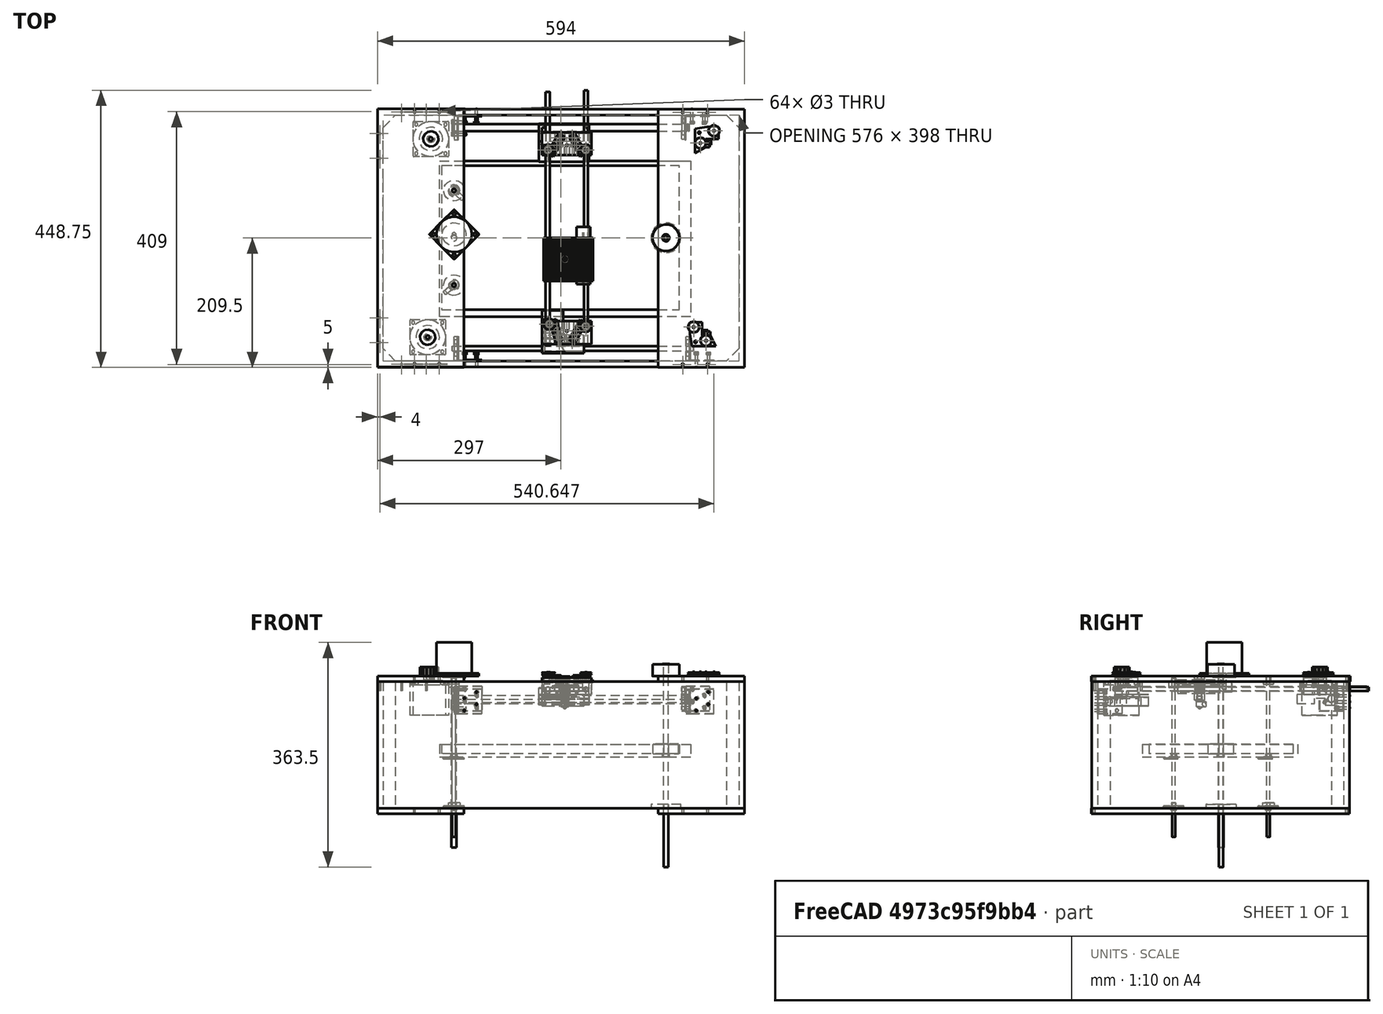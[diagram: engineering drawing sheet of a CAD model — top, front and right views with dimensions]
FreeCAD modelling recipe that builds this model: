
FCSTD DOCUMENT  (FreeCAD 0.18R16110 (Git))
Label: assembly
License: All rights reserved
LicenseURL: http://en.wikipedia.org/wiki/All_rights_reserved
objects: App::FeaturePython×310, Part::FeaturePython×82, Part::Part2DObjectPython×29, App::DocumentObjectGroup×14
note: 111 computed .brp shape members not serialized (recipe doc carries the construction recipe); baked Part::Feature solids carry a one-line shape summary decoded from their .brp

FEATURE [Part::FeaturePython] b_Case_001_  label="Case_001"  # a2plus imported part (geometry in sourceFile) (typed FeaturePython)
  a2p_Version = V0.1
  fixedPosition = true
  sourceFile = ./../Case.FCStd
  subassemblyImport = false
  timeLastImport = 1.56043e+09
  updateColors = true
FEATURE [Part::FeaturePython] b_cylinder1_11_5_001_  label="cylinder1_11.5_001"  # a2plus imported part (geometry in sourceFile) (typed FeaturePython)
  Placement = pos=(-175.853,179,-27.4993) rot=(-0.410574,0.814161,-0.410574;1.77496rad)
  a2p_Version = V0.1
  fixedPosition = false
  sourceFile = ./../Cylinders/cylinder1_11.5_383.FCStd
  subassemblyImport = false
  timeLastImport = 1.56017e+09
  updateColors = true
FEATURE [Part::FeaturePython] b_cylinder2_7_5_001_  label="cylinder2_7.5_001"  # a2plus imported part (geometry in sourceFile) (typed FeaturePython)
  Placement = pos=(-175.853,-179,-31.8006) rot=(0.025254,0.999362,0.025254;1.57143rad)
  a2p_Version = V0.1
  fixedPosition = false
  sourceFile = ./../Cylinders/cylinder2_7.5_390.FCStd
  subassemblyImport = false
  timeLastImport = 1.56017e+09
  updateColors = true
FEATURE [Part::FeaturePython] b_carrier1_11_5_001_  label="carrier1_11.5_001"  # a2plus imported part (geometry in sourceFile) (typed FeaturePython)
  Placement = pos=(45.4279,185.2,-9.99932) rot=(0.57735,-0.57735,-0.57735;2.0944rad)
  a2p_Version = V0.1
  fixedPosition = false
  sourceFile = ./../Carrieges/carrier1_11.5.FCStd
  subassemblyImport = false
  timeLastImport = 1.56017e+09
  updateColors = true
FEATURE [Part::FeaturePython] b_carrier2_7_5_benq_001_  label="carrier2_7.5_benq_001"  # a2plus imported part (geometry in sourceFile) (typed FeaturePython)
  Placement = pos=(-30.5723,-179,-39.1006) rot=(0.009098,0.224299,-0.974478;1e-06rad)
  a2p_Version = V0.1
  fixedPosition = false
  sourceFile = ./../Carrieges/carrier2_7.5_benq.FCStd
  subassemblyImport = false
  timeLastImport = 1.56017e+09
  updateColors = true
FEATURE [Part::FeaturePython] b_carrier4_6_7_lexm_001_  label="carrier4_6.7_lexm_001"  # a2plus imported part (geometry in sourceFile) (typed FeaturePython)
  Placement = pos=(45.1778,-74.8098,-1.75061) rot=(0,0.707107,0.707107;3.14159rad)
  a2p_Version = V0.1
  fixedPosition = false
  sourceFile = ./../Carrieges/carrier4_6.7_lexm.FCStd
  subassemblyImport = false
  timeLastImport = 1.56044e+09
  updateColors = true
FEATURE [Part::FeaturePython] b_cylinder4_6_7_001_  label="cylinder4_6.7_001"  # a2plus imported part (geometry in sourceFile) (typed FeaturePython)
  Placement = pos=(40.1778,-172.746,-11.7506) rot=(-0.290521,0.676608,0.676608;2.57612rad)
  a2p_Version = V0.1
  fixedPosition = false
  sourceFile = ./../Cylinders/cylinder4_6.7_415.FCStd
  subassemblyImport = false
  timeLastImport = 1.56017e+09
  updateColors = true
FEATURE [Part::FeaturePython] b_cylinder3_6_5_001_  label="cylinder3_6.5_001"  # a2plus imported part (geometry in sourceFile) (typed FeaturePython)
  Placement = pos=(-21.322,236.29,-11.7506) rot=(0.994647,-0.073069,0.073069;1.57616rad)
  a2p_Version = V0.1
  fixedPosition = false
  sourceFile = ./../Cylinders/cylinder3_6.5_410.FCStd
  subassemblyImport = false
  timeLastImport = 1.56017e+09
  updateColors = true
FEATURE [Part::FeaturePython] b_carrier3_001_  label="carrier3_001"  # a2plus imported part (geometry in sourceFile) (typed FeaturePython)
  Placement = pos=(5.67784,-1.81521,-4.2506) rot=(0,-0.707107,0.707107;3.14159rad)
  a2p_Version = V0.1
  fixedPosition = false
  sourceFile = ./../Carrieges/carrier3_6.5.FCStd
  subassemblyImport = false
  timeLastImport = 1.56044e+09
  updateColors = true
FEATURE [App::FeaturePython] axisCoincident_006  label="axisCoincident_006__carrier3_001"  # a2plus constraint (typed FeaturePython)
  Object1 = b_cylinder3_6_5_001_
  Object2 = b_carrier3_001_
  ParentTreeObject = -> b_cylinder3_6_5_001_
  SubElement1 = Face1
  SubElement2 = Face9
  Type = axial
  directionConstraint = 1
  lockRotation = false
FEATURE [App::FeaturePython] axisCoincident_006_mirror  label="axisCoincident_006__cylinder3_6.5_001"  # a2plus constraint (typed FeaturePython)
  Object1 = b_cylinder3_6_5_001_
  Object2 = b_carrier3_001_
  ParentTreeObject = -> b_carrier3_001_
  SubElement1 = Face1
  SubElement2 = Face9
  Type = axial
  directionConstraint = 1
  lockRotation = false
FEATURE [App::DocumentObjectGroup] Group001  label="Cylinders"
  Group = -> [b_cylinder1_11_5_001_,b_cylinder2_7_5_001_,b_cylinder4_6_7_001_,b_cylinder3_6_5_001_]
FEATURE [Part::FeaturePython] b_PlywoodPlate_001_  label="PlywoodPlate_001"  # a2plus imported part (geometry in sourceFile) (typed FeaturePython)
  Placement = pos=(-157,-208.5,9) rot=(0,1,0;3.14159rad)
  a2p_Version = V0.1
  fixedPosition = false
  sourceFile = ./../PlywoodPlates/PlywoodPlate.FCStd
  subassemblyImport = false
  timeLastImport = 1.56051e+09
  updateColors = true
FEATURE [App::FeaturePython] planeCoincident_010  label="planeCoincident_010__Case_001"  # a2plus constraint (typed FeaturePython)
  Object1 = b_PlywoodPlate_001_
  Object2 = b_Case_001_
  ParentTreeObject = -> b_PlywoodPlate_001_
  SubElement1 = Face5
  SubElement2 = Face4
  Type = plane
  directionConstraint = 1
  offset = 0
FEATURE [App::FeaturePython] planeCoincident_010_mirror  label="planeCoincident_010__PlywoodPlate_001"  # a2plus constraint (typed FeaturePython)
  Object1 = b_PlywoodPlate_001_
  Object2 = b_Case_001_
  ParentTreeObject = -> b_Case_001_
  SubElement1 = Face5
  SubElement2 = Face4
  Type = plane
  directionConstraint = 1
  offset = 0
FEATURE [App::FeaturePython] planeCoincident_011  label="planeCoincident_011__Case_001"  # a2plus constraint (typed FeaturePython)
  Object1 = b_PlywoodPlate_001_
  Object2 = b_Case_001_
  ParentTreeObject = -> b_PlywoodPlate_001_
  SubElement1 = Face3
  SubElement2 = Face2
  Type = plane
  directionConstraint = 1
  offset = 0
FEATURE [App::FeaturePython] planeCoincident_011_mirror  label="planeCoincident_011__PlywoodPlate_001"  # a2plus constraint (typed FeaturePython)
  Object1 = b_PlywoodPlate_001_
  Object2 = b_Case_001_
  ParentTreeObject = -> b_Case_001_
  SubElement1 = Face3
  SubElement2 = Face2
  Type = plane
  directionConstraint = 1
  offset = 0
FEATURE [App::FeaturePython] planeCoincident_014  label="planeCoincident_014__Case_001"  # a2plus constraint (typed FeaturePython)
  Object1 = b_PlywoodPlate_001_
  Object2 = b_Case_001_
  ParentTreeObject = -> b_PlywoodPlate_001_
  SubElement1 = Face1
  SubElement2 = Face1
  Type = plane
  directionConstraint = 1
  offset = 0
FEATURE [App::FeaturePython] planeCoincident_014_mirror  label="planeCoincident_014__PlywoodPlate_001"  # a2plus constraint (typed FeaturePython)
  Object1 = b_PlywoodPlate_001_
  Object2 = b_Case_001_
  ParentTreeObject = -> b_Case_001_
  SubElement1 = Face1
  SubElement2 = Face1
  Type = plane
  directionConstraint = 1
  offset = 0
FEATURE [Part::FeaturePython] b_PlywoodPlate_001_001  label="PlywoodPlate_002"  # a2plus imported part (geometry in sourceFile) (typed FeaturePython)
  Placement = pos=(157,-209.5,-6.83367e-05) rot=(0,0,1;0rad)
  a2p_Version = V0.1
  fixedPosition = false
  sourceFile = ./../PlywoodPlates/PlywoodPlate.FCStd
  subassemblyImport = false
  timeLastImport = 1.56051e+09
  updateColors = true
FEATURE [App::FeaturePython] planeCoincident_016  label="planeCoincident_016__Case_001"  # a2plus constraint (typed FeaturePython)
  Object1 = b_PlywoodPlate_001_001
  Object2 = b_Case_001_
  ParentTreeObject = -> b_PlywoodPlate_001_001
  SubElement1 = Face4
  SubElement2 = Face4
  Type = plane
  directionConstraint = 0
  offset = 0
FEATURE [App::FeaturePython] planeCoincident_016_mirror  label="planeCoincident_016__PlywoodPlate_002"  # a2plus constraint (typed FeaturePython)
  Object1 = b_PlywoodPlate_001_001
  Object2 = b_Case_001_
  ParentTreeObject = -> b_Case_001_
  SubElement1 = Face4
  SubElement2 = Face4
  Type = plane
  directionConstraint = 0
  offset = 0
FEATURE [App::FeaturePython] planeCoincident_017  label="planeCoincident_017__Case_001"  # a2plus constraint (typed FeaturePython)
  Object1 = b_PlywoodPlate_001_001
  Object2 = b_Case_001_
  ParentTreeObject = -> b_PlywoodPlate_001_001
  SubElement1 = Face6
  SubElement2 = Face6
  Type = plane
  directionConstraint = 1
  offset = 0
FEATURE [App::FeaturePython] planeCoincident_017_mirror  label="planeCoincident_017__PlywoodPlate_002"  # a2plus constraint (typed FeaturePython)
  Object1 = b_PlywoodPlate_001_001
  Object2 = b_Case_001_
  ParentTreeObject = -> b_Case_001_
  SubElement1 = Face6
  SubElement2 = Face6
  Type = plane
  directionConstraint = 1
  offset = 0
FEATURE [App::FeaturePython] planeCoincident_018  label="planeCoincident_018__Case_001"  # a2plus constraint (typed FeaturePython)
  Object1 = b_PlywoodPlate_001_001
  Object2 = b_Case_001_
  ParentTreeObject = -> b_PlywoodPlate_001_001
  SubElement1 = Face3
  SubElement2 = Face3
  Type = plane
  directionConstraint = 1
  offset = 0
FEATURE [App::FeaturePython] planeCoincident_018_mirror  label="planeCoincident_018__PlywoodPlate_002"  # a2plus constraint (typed FeaturePython)
  Object1 = b_PlywoodPlate_001_001
  Object2 = b_Case_001_
  ParentTreeObject = -> b_Case_001_
  SubElement1 = Face3
  SubElement2 = Face3
  Type = plane
  directionConstraint = 1
  offset = 0
FEATURE [Part::FeaturePython] b_nema23_xy_assembl_001_  label="nema23_xy_assembl_001"  # a2plus imported part (geometry in sourceFile) (typed FeaturePython)
  Placement = pos=(-215.734,-160.4,-4.6) rot=(-1,0,0;1.5708rad)
  a2p_Version = V0.1
  fixedPosition = false
  sourceFile = ./nema23_xy_assembl.FCStd
  subassemblyImport = true
  timeLastImport = 1.56017e+09
  updateColors = true
FEATURE [App::FeaturePython] planeCoincident_033  label="planeCoincident_033__PlywoodPlate_001"  # a2plus constraint (typed FeaturePython)
  Object1 = b_nema23_xy_assembl_001_
  Object2 = b_PlywoodPlate_001_
  ParentTreeObject = -> b_nema23_xy_assembl_001_
  SubElement1 = Face6
  SubElement2 = Face5
  Type = plane
  directionConstraint = 0
  offset = 0
FEATURE [App::FeaturePython] planeCoincident_033_mirror  label="planeCoincident_033__nema23_xy_assembl_001"  # a2plus constraint (typed FeaturePython)
  Object1 = b_nema23_xy_assembl_001_
  Object2 = b_PlywoodPlate_001_
  ParentTreeObject = -> b_PlywoodPlate_001_
  SubElement1 = Face6
  SubElement2 = Face5
  Type = plane
  directionConstraint = 0
  offset = 0
FEATURE [Part::FeaturePython] b_nema23_xy_assembl_001_001  label="nema23_xy_assembl_002"  # a2plus imported part (geometry in sourceFile) (typed FeaturePython)
  Placement = pos=(-210.6,160.4,-4.6) rot=(-1,0,0;1.5708rad)
  a2p_Version = V0.1
  fixedPosition = false
  sourceFile = ./nema23_xy_assembl.FCStd
  subassemblyImport = true
  timeLastImport = 1.56017e+09
  updateColors = true
FEATURE [App::FeaturePython] planeCoincident_035  label="planeCoincident_035__PlywoodPlate_001"  # a2plus constraint (typed FeaturePython)
  Object1 = b_nema23_xy_assembl_001_001
  Object2 = b_PlywoodPlate_001_
  ParentTreeObject = -> b_nema23_xy_assembl_001_001
  SubElement1 = Face6
  SubElement2 = Face5
  Type = plane
  directionConstraint = 0
  offset = 0
FEATURE [App::FeaturePython] planeCoincident_035_mirror  label="planeCoincident_035__nema23_xy_assembl_002"  # a2plus constraint (typed FeaturePython)
  Object1 = b_nema23_xy_assembl_001_001
  Object2 = b_PlywoodPlate_001_
  ParentTreeObject = -> b_PlywoodPlate_001_
  SubElement1 = Face6
  SubElement2 = Face5
  Type = plane
  directionConstraint = 0
  offset = 0
FEATURE [App::FeaturePython] axisParallel_010  label="axisParallel_010__Case_001"  # a2plus constraint (typed FeaturePython)
  Object1 = b_nema23_xy_assembl_001_001
  Object2 = b_Case_001_
  ParentTreeObject = -> b_nema23_xy_assembl_001_001
  SubElement1 = Edge3
  SubElement2 = Edge34
  Type = axisParallel
  directionConstraint = 0
FEATURE [App::FeaturePython] axisParallel_010_mirror  label="axisParallel_010__nema23_xy_assembl_002"  # a2plus constraint (typed FeaturePython)
  Object1 = b_nema23_xy_assembl_001_001
  Object2 = b_Case_001_
  ParentTreeObject = -> b_Case_001_
  SubElement1 = Edge3
  SubElement2 = Edge34
  Type = axisParallel
  directionConstraint = 0
FEATURE [App::FeaturePython] axisParallel_011  label="axisParallel_011__Case_001"  # a2plus constraint (typed FeaturePython)
  Object1 = b_nema23_xy_assembl_001_001
  Object2 = b_Case_001_
  ParentTreeObject = -> b_nema23_xy_assembl_001_001
  SubElement1 = Edge29
  SubElement2 = Edge36
  Type = axisParallel
  directionConstraint = 0
FEATURE [App::FeaturePython] axisParallel_011_mirror  label="axisParallel_011__nema23_xy_assembl_002"  # a2plus constraint (typed FeaturePython)
  Object1 = b_nema23_xy_assembl_001_001
  Object2 = b_Case_001_
  ParentTreeObject = -> b_Case_001_
  SubElement1 = Edge29
  SubElement2 = Edge36
  Type = axisParallel
  directionConstraint = 0
FEATURE [App::FeaturePython] axisParallel_012  label="axisParallel_012__Case_001"  # a2plus constraint (typed FeaturePython)
  Object1 = b_nema23_xy_assembl_001_
  Object2 = b_Case_001_
  ParentTreeObject = -> b_nema23_xy_assembl_001_
  SubElement1 = Edge43
  SubElement2 = Edge30
  Type = axisParallel
  directionConstraint = 0
FEATURE [App::FeaturePython] axisParallel_012_mirror  label="axisParallel_012__nema23_xy_assembl_001"  # a2plus constraint (typed FeaturePython)
  Object1 = b_nema23_xy_assembl_001_
  Object2 = b_Case_001_
  ParentTreeObject = -> b_Case_001_
  SubElement1 = Edge43
  SubElement2 = Edge30
  Type = axisParallel
  directionConstraint = 0
FEATURE [App::FeaturePython] axisParallel_013  label="axisParallel_013__Case_001"  # a2plus constraint (typed FeaturePython)
  Object1 = b_nema23_xy_assembl_001_
  Object2 = b_Case_001_
  ParentTreeObject = -> b_nema23_xy_assembl_001_
  SubElement1 = Edge12
  SubElement2 = Edge36
  Type = axisParallel
  directionConstraint = 0
FEATURE [App::FeaturePython] axisParallel_013_mirror  label="axisParallel_013__nema23_xy_assembl_001"  # a2plus constraint (typed FeaturePython)
  Object1 = b_nema23_xy_assembl_001_
  Object2 = b_Case_001_
  ParentTreeObject = -> b_Case_001_
  SubElement1 = Edge12
  SubElement2 = Edge36
  Type = axisParallel
  directionConstraint = 0
FEATURE [App::DocumentObjectGroup] Group004  label="red_cables"
FEATURE [App::DocumentObjectGroup] Group005  label="blue_cables"
FEATURE [Part::FeaturePython] b_UPS_radiator_001_  label="UPS_radiator_001"  # a2plus imported part (geometry in sourceFile) (typed FeaturePython)
  Placement = pos=(9.42777,-134.5,-20.5006) rot=(0.017832,0.328389,-0.944374;1e-06rad)
  a2p_Version = V0.1
  fixedPosition = true
  sourceFile = ./../Carrieges/UPS_radiator.FCStd
  subassemblyImport = false
  timeLastImport = 1.56051e+09
  updateColors = true
FEATURE [Part::FeaturePython] b_UPS_radiator_001_001  label="UPS_radiator_002"  # a2plus imported part (geometry in sourceFile) (typed FeaturePython)
  Placement = pos=(9.42797,134.2,-20.5001) rot=(-1e-06,0,1;3.14159rad)
  a2p_Version = V0.1
  fixedPosition = false
  sourceFile = ./../Carrieges/UPS_radiator.FCStd
  subassemblyImport = false
  timeLastImport = 1.56051e+09
  updateColors = true
FEATURE [App::DocumentObjectGroup] Group006  label="UPS_radiator"
  Group = -> [b_UPS_radiator_001_,b_UPS_radiator_001_001]
FEATURE [Part::FeaturePython] b_corner_steel_8_001_  label="corner_steel_8_001"  # a2plus imported part (geometry in sourceFile) (typed FeaturePython)
  Placement = pos=(207.547,-199,-51.8006) rot=(-1,0,0;1.5708rad)
  a2p_Version = V0.1
  fixedPosition = false
  sourceFile = .\..\fasteners\corner_steel_8.FCStd
  subassemblyImport = false
  timeLastImport = 1.56017e+09
  updateColors = true
FEATURE [Part::FeaturePython] b_corner_steel_8_001_001  label="corner_steel_8_002"  # a2plus imported part (geometry in sourceFile) (typed FeaturePython)
  Placement = pos=(-167.853,-199,-51.8006) rot=(-1,0,0;1.5708rad)
  a2p_Version = V0.1
  fixedPosition = false
  sourceFile = .\..\fasteners\corner_steel_8.FCStd
  subassemblyImport = false
  timeLastImport = 1.56017e+09
  updateColors = true
FEATURE [Part::FeaturePython] b_corner_steel_12_001_  label="corner_steel_12_001"  # a2plus imported part (geometry in sourceFile) (typed FeaturePython)
  Placement = pos=(-167.853,199,-7.49931) rot=(1,0,0;1.5708rad)
  a2p_Version = V0.1
  fixedPosition = true
  sourceFile = .\..\fasteners\corner_steel_12.FCStd
  subassemblyImport = false
  timeLastImport = 1.56017e+09
  updateColors = true
FEATURE [Part::FeaturePython] b_corner_steel_12_001_001  label="corner_steel_12_002"  # a2plus imported part (geometry in sourceFile) (typed FeaturePython)
  Placement = pos=(200.547,199,-7.49932) rot=(1,0,0;1.5708rad)
  a2p_Version = V0.1
  fixedPosition = false
  sourceFile = .\..\fasteners\corner_steel_12.FCStd
  subassemblyImport = false
  timeLastImport = 1.56017e+09
  updateColors = true
FEATURE [App::DocumentObjectGroup] Group  label="MetalCorners"
  Group = -> [b_corner_steel_8_001_,b_corner_steel_8_001_001,b_corner_steel_12_001_,b_corner_steel_12_001_001]
FEATURE [App::FeaturePython] axisCoincident_002  label="axisCoincident_002__cylinder1_11.5_001"  # a2plus constraint (typed FeaturePython)
  Object1 = b_carrier1_11_5_001_
  Object2 = b_cylinder1_11_5_001_
  ParentTreeObject = -> b_carrier1_11_5_001_
  SubElement1 = Face16
  SubElement2 = Face1
  Type = axial
  directionConstraint = 1
  lockRotation = false
FEATURE [App::FeaturePython] axisCoincident_002_mirror  label="axisCoincident_002__carrier1_11.5_001"  # a2plus constraint (typed FeaturePython)
  Object1 = b_carrier1_11_5_001_
  Object2 = b_cylinder1_11_5_001_
  ParentTreeObject = -> b_cylinder1_11_5_001_
  SubElement1 = Face16
  SubElement2 = Face1
  Type = axial
  directionConstraint = 1
  lockRotation = false
FEATURE [App::FeaturePython] circularEdge_002  label="circularEdge_002__cylinder2_7.5_001"  # a2plus constraint (typed FeaturePython)
  Object1 = b_corner_steel_8_001_
  Object2 = b_cylinder2_7_5_001_
  ParentTreeObject = -> b_corner_steel_8_001_
  SubElement1 = Edge30
  SubElement2 = Edge1
  Type = circularEdge
  directionConstraint = 0
  lockRotation = false
  offset = -5
FEATURE [App::FeaturePython] circularEdge_002_mirror  label="circularEdge_002__corner_steel_8_001"  # a2plus constraint (typed FeaturePython)
  Object1 = b_corner_steel_8_001_
  Object2 = b_cylinder2_7_5_001_
  ParentTreeObject = -> b_cylinder2_7_5_001_
  SubElement1 = Edge30
  SubElement2 = Edge1
  Type = circularEdge
  directionConstraint = 0
  lockRotation = false
  offset = -5
FEATURE [App::FeaturePython] planeCoincident_003  label="planeCoincident_003__Case_001"  # a2plus constraint (typed FeaturePython)
  Object1 = b_corner_steel_8_001_
  Object2 = b_Case_001_
  ParentTreeObject = -> b_corner_steel_8_001_
  SubElement1 = Face2
  SubElement2 = Face11
  Type = plane
  directionConstraint = 1
  offset = 0
FEATURE [App::FeaturePython] planeCoincident_003_mirror  label="planeCoincident_003__corner_steel_8_001"  # a2plus constraint (typed FeaturePython)
  Object1 = b_corner_steel_8_001_
  Object2 = b_Case_001_
  ParentTreeObject = -> b_Case_001_
  SubElement1 = Face2
  SubElement2 = Face11
  Type = plane
  directionConstraint = 1
  offset = 0
FEATURE [App::FeaturePython] axisCoincident_008  label="axisCoincident_008__cylinder2_7.5_001"  # a2plus constraint (typed FeaturePython)
  Object1 = b_carrier2_7_5_benq_001_
  Object2 = b_cylinder2_7_5_001_
  ParentTreeObject = -> b_carrier2_7_5_benq_001_
  SubElement1 = Face33
  SubElement2 = Face1
  Type = axial
  directionConstraint = 0
  lockRotation = false
FEATURE [App::FeaturePython] axisCoincident_008_mirror  label="axisCoincident_008__carrier2_7.5_benq_001"  # a2plus constraint (typed FeaturePython)
  Object1 = b_carrier2_7_5_benq_001_
  Object2 = b_cylinder2_7_5_001_
  ParentTreeObject = -> b_cylinder2_7_5_001_
  SubElement1 = Face33
  SubElement2 = Face1
  Type = axial
  directionConstraint = 0
  lockRotation = false
FEATURE [App::FeaturePython] circularEdge_004  label="circularEdge_004__cylinder1_11.5_001"  # a2plus constraint (typed FeaturePython)
  Object1 = b_corner_steel_12_001_001
  Object2 = b_cylinder1_11_5_001_
  ParentTreeObject = -> b_corner_steel_12_001_001
  SubElement1 = Edge30
  SubElement2 = Edge11
  Type = circularEdge
  directionConstraint = 0
  lockRotation = false
  offset = -5
FEATURE [App::FeaturePython] circularEdge_004_mirror  label="circularEdge_004__corner_steel_12_002"  # a2plus constraint (typed FeaturePython)
  Object1 = b_corner_steel_12_001_001
  Object2 = b_cylinder1_11_5_001_
  ParentTreeObject = -> b_cylinder1_11_5_001_
  SubElement1 = Edge30
  SubElement2 = Edge11
  Type = circularEdge
  directionConstraint = 0
  lockRotation = false
  offset = -5
FEATURE [App::FeaturePython] planeCoincident_002  label="planeCoincident_002__Case_001"  # a2plus constraint (typed FeaturePython)
  Object1 = b_corner_steel_12_001_001
  Object2 = b_Case_001_
  ParentTreeObject = -> b_corner_steel_12_001_001
  SubElement1 = Face2
  SubElement2 = Face16
  Type = plane
  directionConstraint = 1
  offset = 0
FEATURE [App::FeaturePython] planeCoincident_002_mirror  label="planeCoincident_002__corner_steel_12_002"  # a2plus constraint (typed FeaturePython)
  Object1 = b_corner_steel_12_001_001
  Object2 = b_Case_001_
  ParentTreeObject = -> b_Case_001_
  SubElement1 = Face2
  SubElement2 = Face16
  Type = plane
  directionConstraint = 1
  offset = 0
FEATURE [Part::FeaturePython] b_rollerAssembly1_001_  label="rollerAssembly1_001"  # a2plus imported part (geometry in sourceFile) (typed FeaturePython)
  Placement = pos=(26.464,140.406,6.5) rot=(0,0,1;2.09441rad)
  a2p_Version = V0.1
  fixedPosition = false
  sourceFile = .\..\rollers\rollerAssembly1.FCStd
  subassemblyImport = true
  timeLastImport = 1.56017e+09
  updateColors = true
FEATURE [Part::FeaturePython] b_rollerAssembly1_001_001  label="rollerAssembly1_002"  # a2plus imported part (geometry in sourceFile) (typed FeaturePython)
  Placement = pos=(-5.03789,-140.771,6.4994) rot=(0,0,-1;1.309rad)
  a2p_Version = V0.1
  fixedPosition = false
  sourceFile = .\..\rollers\rollerAssembly1.FCStd
  subassemblyImport = true
  timeLastImport = 1.56017e+09
  updateColors = true
FEATURE [Part::FeaturePython] b_rollerAssembly2_001_  label="rollerAssembly2_001"  # a2plus imported part (geometry in sourceFile) (typed FeaturePython)
  Placement = pos=(26.4637,-140.706,6.49959) rot=(0,0,1;4.18879rad)
  a2p_Version = V0.1
  fixedPosition = false
  sourceFile = .\..\rollers\rollerAssembly2.FCStd
  subassemblyImport = true
  timeLastImport = 1.56017e+09
  updateColors = true
FEATURE [Part::FeaturePython] b_rollerAssembly2_001_001  label="rollerAssembly2_002"  # a2plus imported part (geometry in sourceFile) (typed FeaturePython)
  Placement = pos=(-7.60776,140.406,6.49981) rot=(-2e-06,-2e-06,1;1.04722rad)
  a2p_Version = V0.1
  fixedPosition = false
  sourceFile = .\..\rollers\rollerAssembly2.FCStd
  subassemblyImport = true
  timeLastImport = 1.56017e+09
  updateColors = true
FEATURE [Part::FeaturePython] b_rollerDoubleAssembly_001_  label="rollerDoubleAssembly_001"  # a2plus imported part (geometry in sourceFile) (typed FeaturePython)
  Placement = pos=(216.647,176.686,9) rot=(0,0,-1;1.5708rad)
  a2p_Version = V0.1
  fixedPosition = true
  sourceFile = .\..\rollers\rollerDoubleAssembly.FCStd
  subassemblyImport = true
  timeLastImport = 1.56052e+09
  updateColors = true
FEATURE [Part::FeaturePython] b_rollerDoubleAssembly_001_001  label="rollerDoubleAssembly_002"  # a2plus imported part (geometry in sourceFile) (typed FeaturePython)
  Placement = pos=(211.726,-175.044,8.99979) rot=(-0.229486,0.973312,0;0rad)
  a2p_Version = V0.1
  fixedPosition = true
  sourceFile = .\..\rollers\rollerDoubleAssembly.FCStd
  subassemblyImport = true
  timeLastImport = 1.56052e+09
  updateColors = true
FEATURE [App::DocumentObjectGroup] ____________  label="Rollers"
  Group = -> [b_rollerAssembly1_001_,b_rollerAssembly1_001_001,b_rollerAssembly2_001_,b_rollerAssembly2_001_001,b_rollerDoubleAssembly_001_,b_rollerDoubleAssembly_001_001]
FEATURE [App::FeaturePython] planesParallel_003  label="planesParallel_003__Case_001"  # a2plus constraint (typed FeaturePython)
  Object1 = b_corner_steel_8_001_
  Object2 = b_Case_001_
  ParentTreeObject = -> b_corner_steel_8_001_
  SubElement1 = Face4
  SubElement2 = Face4
  Type = planesParallel
  directionConstraint = 1
FEATURE [App::FeaturePython] planesParallel_003_mirror  label="planesParallel_003__corner_steel_8_001"  # a2plus constraint (typed FeaturePython)
  Object1 = b_corner_steel_8_001_
  Object2 = b_Case_001_
  ParentTreeObject = -> b_Case_001_
  SubElement1 = Face4
  SubElement2 = Face4
  Type = planesParallel
  directionConstraint = 1
FEATURE [App::FeaturePython] planesParallel_005  label="planesParallel_005__Case_001"  # a2plus constraint (typed FeaturePython)
  Object1 = b_corner_steel_12_001_001
  Object2 = b_Case_001_
  ParentTreeObject = -> b_corner_steel_12_001_001
  SubElement1 = Face3
  SubElement2 = Face4
  Type = planesParallel
  directionConstraint = 0
FEATURE [App::FeaturePython] planesParallel_005_mirror  label="planesParallel_005__corner_steel_12_002"  # a2plus constraint (typed FeaturePython)
  Object1 = b_corner_steel_12_001_001
  Object2 = b_Case_001_
  ParentTreeObject = -> b_Case_001_
  SubElement1 = Face3
  SubElement2 = Face4
  Type = planesParallel
  directionConstraint = 0
FEATURE [Part::FeaturePython] b_PlywoodPlate_001_002  label="PlywoodPlate_003"  # a2plus imported part (geometry in sourceFile) (typed FeaturePython)
  Placement = pos=(-157,-209.5,-205) rot=(0,1,0;3.14159rad)
  a2p_Version = V0.1
  fixedPosition = false
  sourceFile = ./../PlywoodPlates/PlywoodPlate.FCStd
  subassemblyImport = false
  timeLastImport = 1.56051e+09
  updateColors = true
FEATURE [App::FeaturePython] planeCoincident_022  label="planeCoincident_022__Case_001"  # a2plus constraint (typed FeaturePython)
  Object1 = b_PlywoodPlate_001_002
  Object2 = b_Case_001_
  ParentTreeObject = -> b_PlywoodPlate_001_002
  SubElement1 = Face4
  SubElement2 = Face5
  Type = plane
  directionConstraint = 1
  offset = 0
FEATURE [App::FeaturePython] planeCoincident_022_mirror  label="planeCoincident_022__PlywoodPlate_003"  # a2plus constraint (typed FeaturePython)
  Object1 = b_PlywoodPlate_001_002
  Object2 = b_Case_001_
  ParentTreeObject = -> b_Case_001_
  SubElement1 = Face4
  SubElement2 = Face5
  Type = plane
  directionConstraint = 1
  offset = 0
FEATURE [App::FeaturePython] planeCoincident_023  label="planeCoincident_023__Case_001"  # a2plus constraint (typed FeaturePython)
  Object1 = b_PlywoodPlate_001_002
  Object2 = b_Case_001_
  ParentTreeObject = -> b_PlywoodPlate_001_002
  SubElement1 = Face3
  SubElement2 = Face2
  Type = plane
  directionConstraint = 1
  offset = 0
FEATURE [App::FeaturePython] planeCoincident_023_mirror  label="planeCoincident_023__PlywoodPlate_003"  # a2plus constraint (typed FeaturePython)
  Object1 = b_PlywoodPlate_001_002
  Object2 = b_Case_001_
  ParentTreeObject = -> b_Case_001_
  SubElement1 = Face3
  SubElement2 = Face2
  Type = plane
  directionConstraint = 1
  offset = 0
FEATURE [App::FeaturePython] planeCoincident_024  label="planeCoincident_024__Case_001"  # a2plus constraint (typed FeaturePython)
  Object1 = b_PlywoodPlate_001_002
  Object2 = b_Case_001_
  ParentTreeObject = -> b_PlywoodPlate_001_002
  SubElement1 = Face6
  SubElement2 = Face6
  Type = plane
  directionConstraint = 1
  offset = 0
FEATURE [App::FeaturePython] planeCoincident_024_mirror  label="planeCoincident_024__PlywoodPlate_003"  # a2plus constraint (typed FeaturePython)
  Object1 = b_PlywoodPlate_001_002
  Object2 = b_Case_001_
  ParentTreeObject = -> b_Case_001_
  SubElement1 = Face6
  SubElement2 = Face6
  Type = plane
  directionConstraint = 1
  offset = 0
FEATURE [Part::FeaturePython] b_PlywoodPlate_001_003  label="PlywoodPlate_004"  # a2plus imported part (geometry in sourceFile) (typed FeaturePython)
  Placement = pos=(157,-209.5,-214) rot=(0,0,1;0rad)
  a2p_Version = V0.1
  fixedPosition = false
  sourceFile = ./../PlywoodPlates/PlywoodPlate.FCStd
  subassemblyImport = false
  timeLastImport = 1.56051e+09
  updateColors = true
FEATURE [App::FeaturePython] planeCoincident_025  label="planeCoincident_025__Case_001"  # a2plus constraint (typed FeaturePython)
  Object1 = b_PlywoodPlate_001_003
  Object2 = b_Case_001_
  ParentTreeObject = -> b_PlywoodPlate_001_003
  SubElement1 = Face5
  SubElement2 = Face5
  Type = plane
  directionConstraint = 0
  offset = 0
FEATURE [App::FeaturePython] planeCoincident_025_mirror  label="planeCoincident_025__PlywoodPlate_004"  # a2plus constraint (typed FeaturePython)
  Object1 = b_PlywoodPlate_001_003
  Object2 = b_Case_001_
  ParentTreeObject = -> b_Case_001_
  SubElement1 = Face5
  SubElement2 = Face5
  Type = plane
  directionConstraint = 0
  offset = 0
FEATURE [App::FeaturePython] planeCoincident_026  label="planeCoincident_026__Case_001"  # a2plus constraint (typed FeaturePython)
  Object1 = b_PlywoodPlate_001_003
  Object2 = b_Case_001_
  ParentTreeObject = -> b_PlywoodPlate_001_003
  SubElement1 = Face6
  SubElement2 = Face6
  Type = plane
  directionConstraint = 1
  offset = 0
FEATURE [App::FeaturePython] planeCoincident_026_mirror  label="planeCoincident_026__PlywoodPlate_004"  # a2plus constraint (typed FeaturePython)
  Object1 = b_PlywoodPlate_001_003
  Object2 = b_Case_001_
  ParentTreeObject = -> b_Case_001_
  SubElement1 = Face6
  SubElement2 = Face6
  Type = plane
  directionConstraint = 1
  offset = 0
FEATURE [App::FeaturePython] planeCoincident_027  label="planeCoincident_027__Case_001"  # a2plus constraint (typed FeaturePython)
  Object1 = b_PlywoodPlate_001_003
  Object2 = b_Case_001_
  ParentTreeObject = -> b_PlywoodPlate_001_003
  SubElement1 = Face3
  SubElement2 = Face3
  Type = plane
  directionConstraint = 1
  offset = 0
FEATURE [App::FeaturePython] planeCoincident_027_mirror  label="planeCoincident_027__PlywoodPlate_004"  # a2plus constraint (typed FeaturePython)
  Object1 = b_PlywoodPlate_001_003
  Object2 = b_Case_001_
  ParentTreeObject = -> b_Case_001_
  SubElement1 = Face3
  SubElement2 = Face3
  Type = plane
  directionConstraint = 1
  offset = 0
FEATURE [App::DocumentObjectGroup] Group008  label="PlywoodPlates"
  Group = -> [b_PlywoodPlate_001_,b_PlywoodPlate_001_001,b_PlywoodPlate_001_002,b_PlywoodPlate_001_003]
FEATURE [Part::FeaturePython] b_threadedRod_001_  label="threadedRod_001"  # a2plus imported part (geometry in sourceFile) (typed FeaturePython)
  Placement = pos=(-173.218,0.40297,-268.6) rot=(9.8e-05,0,1;0.00013rad)
  a2p_Version = V0.1
  fixedPosition = false
  sourceFile = ./../Cylinders/threadedRod.FCStd
  subassemblyImport = false
  timeLastImport = 1.56017e+09
  updateColors = true
FEATURE [Part::FeaturePython] b_cylinder_001_  label="cylinder_1_5.5"  # a2plus imported part (geometry in sourceFile) (typed FeaturePython)
  Placement = pos=(-173.218,-76.097,-250.991) rot=(0,0,1;0rad)
  a2p_Version = V0.1
  fixedPosition = false
  sourceFile = ./../Cylinders_Z/1_5,5/cylinder_5.5.FCStd
  subassemblyImport = false
  timeLastImport = 1.56017e+09
  updateColors = true
FEATURE [Part::FeaturePython] b_cylinder_001_001  label="cylinder_2_5.5"  # a2plus imported part (geometry in sourceFile) (typed FeaturePython)
  Placement = pos=(-173.218,76.903,-250.991) rot=(0,0,1;0rad)
  a2p_Version = V0.1
  fixedPosition = false
  sourceFile = ./../Cylinders_Z/1_5,5/cylinder_5.5.FCStd
  subassemblyImport = false
  timeLastImport = 1.56017e+09
  updateColors = true
FEATURE [Part::FeaturePython] b_fixator_2_001_  label="fixator_2_001"  # a2plus imported part (geometry in sourceFile) (typed FeaturePython)
  Placement = pos=(-173.218,-76.097,-121.687) rot=(-0.34556,0.938397,0;3.14159rad)
  a2p_Version = V0.1
  fixedPosition = false
  sourceFile = ./../Cylinders_Z/1_5,5/fixator_2_5.5.FCStd
  subassemblyImport = false
  timeLastImport = 1.56041e+09
  updateColors = true
FEATURE [Part::FeaturePython] b_gear1_5_5x33_5_001_  label="gear1_5.5x33.5_001"  # a2plus imported part (geometry in sourceFile) (typed FeaturePython)
  Placement = pos=(-173.218,-76.097,-201.4) rot=(-0.665924,0.746019,0;3.14159rad)
  a2p_Version = V0.1
  fixedPosition = false
  sourceFile = ./../Cylinders_Z/1_5,5/gear1_5.5x33.5.FCStd
  subassemblyImport = false
  timeLastImport = 1.56017e+09
  updateColors = true
FEATURE [Part::FeaturePython] b_gear2_5_5x17_001_  label="gear2_5.5x17_001"  # a2plus imported part (geometry in sourceFile) (typed FeaturePython)
  Placement = pos=(-173.218,-76.097,-9) rot=(0,0,1;0rad)
  a2p_Version = V0.1
  fixedPosition = false
  sourceFile = ./../Cylinders_Z/1_5,5/gear2_5.5x17.FCStd
  subassemblyImport = false
  timeLastImport = 1.56017e+09
  updateColors = true
FEATURE [App::FeaturePython] axisCoincident_009  label="axisCoincident_009__cylinder_1_5.5"  # a2plus constraint (typed FeaturePython)
  Object1 = b_gear1_5_5x33_5_001_
  Object2 = b_cylinder_001_
  ParentTreeObject = -> b_gear1_5_5x33_5_001_
  SubElement1 = Face8
  SubElement2 = Face1
  Type = axial
  directionConstraint = 1
  lockRotation = false
FEATURE [App::FeaturePython] axisCoincident_009_mirror  label="axisCoincident_009__gear1_5.5x33.5_001"  # a2plus constraint (typed FeaturePython)
  Object1 = b_gear1_5_5x33_5_001_
  Object2 = b_cylinder_001_
  ParentTreeObject = -> b_cylinder_001_
  SubElement1 = Face8
  SubElement2 = Face1
  Type = axial
  directionConstraint = 1
  lockRotation = false
FEATURE [App::FeaturePython] axisCoincident_010  label="axisCoincident_010__cylinder_1_5.5"  # a2plus constraint (typed FeaturePython)
  Object1 = b_gear2_5_5x17_001_
  Object2 = b_cylinder_001_
  ParentTreeObject = -> b_gear2_5_5x17_001_
  SubElement1 = Face4
  SubElement2 = Face1
  Type = axial
  directionConstraint = 0
  lockRotation = false
FEATURE [App::FeaturePython] axisCoincident_010_mirror  label="axisCoincident_010__gear2_5.5x17_001"  # a2plus constraint (typed FeaturePython)
  Object1 = b_gear2_5_5x17_001_
  Object2 = b_cylinder_001_
  ParentTreeObject = -> b_cylinder_001_
  SubElement1 = Face4
  SubElement2 = Face1
  Type = axial
  directionConstraint = 0
  lockRotation = false
FEATURE [App::FeaturePython] axisCoincident_011  label="axisCoincident_011__cylinder_1_5.5"  # a2plus constraint (typed FeaturePython)
  Object1 = b_fixator_2_001_
  Object2 = b_cylinder_001_
  ParentTreeObject = -> b_fixator_2_001_
  SubElement1 = Face11
  SubElement2 = Face1
  Type = axial
  directionConstraint = 1
  lockRotation = false
FEATURE [App::FeaturePython] axisCoincident_011_mirror  label="axisCoincident_011__fixator_2_001"  # a2plus constraint (typed FeaturePython)
  Object1 = b_fixator_2_001_
  Object2 = b_cylinder_001_
  ParentTreeObject = -> b_cylinder_001_
  SubElement1 = Face11
  SubElement2 = Face1
  Type = axial
  directionConstraint = 1
  lockRotation = false
FEATURE [App::FeaturePython] planeCoincident_028  label="planeCoincident_028__PlywoodPlate_003"  # a2plus constraint (typed FeaturePython)
  Object1 = b_gear1_5_5x33_5_001_
  Object2 = b_PlywoodPlate_001_002
  ParentTreeObject = -> b_gear1_5_5x33_5_001_
  SubElement1 = Face3
  SubElement2 = Face4
  Type = plane
  directionConstraint = 0
  offset = 0
FEATURE [App::FeaturePython] planeCoincident_028_mirror  label="planeCoincident_028__gear1_5.5x33.5_001"  # a2plus constraint (typed FeaturePython)
  Object1 = b_gear1_5_5x33_5_001_
  Object2 = b_PlywoodPlate_001_002
  ParentTreeObject = -> b_PlywoodPlate_001_002
  SubElement1 = Face3
  SubElement2 = Face4
  Type = plane
  directionConstraint = 0
  offset = 0
FEATURE [App::FeaturePython] planeCoincident_029  label="planeCoincident_029__PlywoodPlate_001"  # a2plus constraint (typed FeaturePython)
  Object1 = b_gear2_5_5x17_001_
  Object2 = b_PlywoodPlate_001_
  ParentTreeObject = -> b_gear2_5_5x17_001_
  SubElement1 = Face3
  SubElement2 = Face5
  Type = plane
  directionConstraint = 1
  offset = 0
FEATURE [App::FeaturePython] planeCoincident_029_mirror  label="planeCoincident_029__gear2_5.5x17_001"  # a2plus constraint (typed FeaturePython)
  Object1 = b_gear2_5_5x17_001_
  Object2 = b_PlywoodPlate_001_
  ParentTreeObject = -> b_PlywoodPlate_001_
  SubElement1 = Face3
  SubElement2 = Face5
  Type = plane
  directionConstraint = 1
  offset = 0
FEATURE [Part::FeaturePython] b_fixator_2_001_001  label="fixator_2_002"  # a2plus imported part (geometry in sourceFile) (typed FeaturePython)
  Placement = pos=(-173.218,76.903,-121.687) rot=(0.928387,-0.371615,0;3.14159rad)
  a2p_Version = V0.1
  fixedPosition = false
  sourceFile = ./../Cylinders_Z/2_5.5/fixator_2_5.5.FCStd
  subassemblyImport = false
  timeLastImport = 1.56041e+09
  updateColors = true
FEATURE [Part::FeaturePython] b_gear1_5_5x33_5_001_001  label="gear1_5.5x33.5_002"  # a2plus imported part (geometry in sourceFile) (typed FeaturePython)
  Placement = pos=(-173.218,76.903,-201.4) rot=(0.956607,0.29138,0;3.14159rad)
  a2p_Version = V0.1
  fixedPosition = false
  sourceFile = ./../Cylinders_Z/2_5.5/gear1_5.5x33.5.FCStd
  subassemblyImport = false
  timeLastImport = 1.56041e+09
  updateColors = true
FEATURE [Part::FeaturePython] b_gear2_5_5x17_001_001  label="gear2_5.5x17_002"  # a2plus imported part (geometry in sourceFile) (typed FeaturePython)
  Placement = pos=(-173.218,76.903,-4.5) rot=(0,0,1;0rad)
  a2p_Version = V0.1
  fixedPosition = false
  sourceFile = ./../Cylinders_Z/2_5.5/gear2_5.5x17.FCStd
  subassemblyImport = false
  timeLastImport = 1.56041e+09
  updateColors = true
FEATURE [App::FeaturePython] axisCoincident_012  label="axisCoincident_012__cylinder_2_5.5"  # a2plus constraint (typed FeaturePython)
  Object1 = b_gear2_5_5x17_001_001
  Object2 = b_cylinder_001_001
  ParentTreeObject = -> b_gear2_5_5x17_001_001
  SubElement1 = Face4
  SubElement2 = Face1
  Type = axial
  directionConstraint = 0
  lockRotation = false
FEATURE [App::FeaturePython] axisCoincident_012_mirror  label="axisCoincident_012__gear2_5.5x17_002"  # a2plus constraint (typed FeaturePython)
  Object1 = b_gear2_5_5x17_001_001
  Object2 = b_cylinder_001_001
  ParentTreeObject = -> b_cylinder_001_001
  SubElement1 = Face4
  SubElement2 = Face1
  Type = axial
  directionConstraint = 0
  lockRotation = false
FEATURE [App::FeaturePython] axisCoincident_013  label="axisCoincident_013__cylinder_2_5.5"  # a2plus constraint (typed FeaturePython)
  Object1 = b_gear1_5_5x33_5_001_001
  Object2 = b_cylinder_001_001
  ParentTreeObject = -> b_gear1_5_5x33_5_001_001
  SubElement1 = Face8
  SubElement2 = Face1
  Type = axial
  directionConstraint = 1
  lockRotation = false
FEATURE [App::FeaturePython] axisCoincident_013_mirror  label="axisCoincident_013__gear1_5.5x33.5_002"  # a2plus constraint (typed FeaturePython)
  Object1 = b_gear1_5_5x33_5_001_001
  Object2 = b_cylinder_001_001
  ParentTreeObject = -> b_cylinder_001_001
  SubElement1 = Face8
  SubElement2 = Face1
  Type = axial
  directionConstraint = 1
  lockRotation = false
FEATURE [App::FeaturePython] axisCoincident_014  label="axisCoincident_014__cylinder_2_5.5"  # a2plus constraint (typed FeaturePython)
  Object1 = b_fixator_2_001_001
  Object2 = b_cylinder_001_001
  ParentTreeObject = -> b_fixator_2_001_001
  SubElement1 = Face11
  SubElement2 = Face1
  Type = axial
  directionConstraint = 1
  lockRotation = false
FEATURE [App::FeaturePython] axisCoincident_014_mirror  label="axisCoincident_014__fixator_2_002"  # a2plus constraint (typed FeaturePython)
  Object1 = b_fixator_2_001_001
  Object2 = b_cylinder_001_001
  ParentTreeObject = -> b_cylinder_001_001
  SubElement1 = Face11
  SubElement2 = Face1
  Type = axial
  directionConstraint = 1
  lockRotation = false
FEATURE [App::FeaturePython] planeCoincident_031  label="planeCoincident_031__PlywoodPlate_003"  # a2plus constraint (typed FeaturePython)
  Object1 = b_gear1_5_5x33_5_001_001
  Object2 = b_PlywoodPlate_001_002
  ParentTreeObject = -> b_gear1_5_5x33_5_001_001
  SubElement1 = Face3
  SubElement2 = Face4
  Type = plane
  directionConstraint = 0
  offset = 0
FEATURE [App::FeaturePython] planeCoincident_031_mirror  label="planeCoincident_031__gear1_5.5x33.5_002"  # a2plus constraint (typed FeaturePython)
  Object1 = b_gear1_5_5x33_5_001_001
  Object2 = b_PlywoodPlate_001_002
  ParentTreeObject = -> b_PlywoodPlate_001_002
  SubElement1 = Face3
  SubElement2 = Face4
  Type = plane
  directionConstraint = 0
  offset = 0
FEATURE [App::FeaturePython] planeCoincident_032  label="planeCoincident_032__PlywoodPlate_001"  # a2plus constraint (typed FeaturePython)
  Object1 = b_gear2_5_5x17_001_001
  Object2 = b_PlywoodPlate_001_
  ParentTreeObject = -> b_gear2_5_5x17_001_001
  SubElement1 = Face3
  SubElement2 = Face5
  Type = plane
  directionConstraint = 1
  offset = 0
FEATURE [App::FeaturePython] planeCoincident_032_mirror  label="planeCoincident_032__gear2_5.5x17_002"  # a2plus constraint (typed FeaturePython)
  Object1 = b_gear2_5_5x17_001_001
  Object2 = b_PlywoodPlate_001_
  ParentTreeObject = -> b_PlywoodPlate_001_
  SubElement1 = Face3
  SubElement2 = Face5
  Type = plane
  directionConstraint = 1
  offset = 0
FEATURE [Part::FeaturePython] b_cylinder_001_002  label="cylinder_001"  # a2plus imported part (geometry in sourceFile) (typed FeaturePython)
  Placement = pos=(169.782,0.40296,-299.9) rot=(0,0,1;0rad)
  a2p_Version = V0.1
  fixedPosition = false
  sourceFile = ./../Cylinders_Z/3_7.5/cylinder_7.5.FCStd
  subassemblyImport = false
  timeLastImport = 1.56017e+09
  updateColors = true
FEATURE [Part::FeaturePython] b_gear_1__7_5_48_5_001_  label="gear_1_ 7.5_48.5_001"  # a2plus imported part (geometry in sourceFile) (typed FeaturePython)
  Placement = pos=(169.782,0.40296,-205) rot=(0,0,1;0rad)
  a2p_Version = V0.1
  fixedPosition = false
  sourceFile = ./../Cylinders_Z/3_7.5/gear_1_ 7.5_48.5.FCStd
  subassemblyImport = false
  timeLastImport = 1.56041e+09
  updateColors = true
FEATURE [App::FeaturePython] planeCoincident_036  label="planeCoincident_036__PlywoodPlate_004"  # a2plus constraint (typed FeaturePython)
  Object1 = b_gear_1__7_5_48_5_001_
  Object2 = b_PlywoodPlate_001_003
  ParentTreeObject = -> b_gear_1__7_5_48_5_001_
  SubElement1 = Face2
  SubElement2 = Face5
  Type = plane
  directionConstraint = 0
  offset = 0
FEATURE [App::FeaturePython] planeCoincident_036_mirror  label="planeCoincident_036__gear_1_ 7.5_48.5_001"  # a2plus constraint (typed FeaturePython)
  Object1 = b_gear_1__7_5_48_5_001_
  Object2 = b_PlywoodPlate_001_003
  ParentTreeObject = -> b_PlywoodPlate_001_003
  SubElement1 = Face2
  SubElement2 = Face5
  Type = plane
  directionConstraint = 0
  offset = 0
FEATURE [Part::FeaturePython] b_gear_2__7_5_41_5_001_  label="gear_2_ 7.5_41.5_001"  # a2plus imported part (geometry in sourceFile) (typed FeaturePython)
  Placement = pos=(169.782,0.402961,-100.687) rot=(0.52082,0.853666,0;3.14159rad)
  a2p_Version = V0.1
  fixedPosition = false
  sourceFile = ./../Cylinders_Z/3_7.5/gear_2_ 7.5_41.5.FCStd
  subassemblyImport = false
  timeLastImport = 1.56017e+09
  updateColors = true
FEATURE [Part::FeaturePython] b_gear_3__7_5_43_5_001_  label="gear_3_ 7.5_43.5_001"  # a2plus imported part (geometry in sourceFile) (typed FeaturePython)
  Placement = pos=(169.782,0.402961,8.99993) rot=(0,0,1;0rad)
  a2p_Version = V0.1
  fixedPosition = false
  sourceFile = ./../Cylinders_Z/3_7.5/gear_3_ 7.5_43.5.FCStd
  subassemblyImport = false
  timeLastImport = 1.56017e+09
  updateColors = true
FEATURE [App::FeaturePython] planeCoincident_038  label="planeCoincident_038__PlywoodPlate_002"  # a2plus constraint (typed FeaturePython)
  Object1 = b_gear_3__7_5_43_5_001_
  Object2 = b_PlywoodPlate_001_001
  ParentTreeObject = -> b_gear_3__7_5_43_5_001_
  SubElement1 = Face2
  SubElement2 = Face5
  Type = plane
  directionConstraint = 0
  offset = 0
FEATURE [App::FeaturePython] planeCoincident_038_mirror  label="planeCoincident_038__gear_3_ 7.5_43.5_001"  # a2plus constraint (typed FeaturePython)
  Object1 = b_gear_3__7_5_43_5_001_
  Object2 = b_PlywoodPlate_001_001
  ParentTreeObject = -> b_PlywoodPlate_001_001
  SubElement1 = Face2
  SubElement2 = Face5
  Type = plane
  directionConstraint = 0
  offset = 0
FEATURE [App::FeaturePython] axisPlaneNormal_001  label="axisPlaneNormal_001__PlywoodPlate_003"  # a2plus constraint (typed FeaturePython)
  Object1 = b_cylinder_001_001
  Object2 = b_PlywoodPlate_001_002
  ParentTreeObject = -> b_cylinder_001_001
  SubElement1 = Face1
  SubElement2 = Face4
  Type = axisPlaneNormal
  directionConstraint = 1
FEATURE [App::FeaturePython] axisPlaneNormal_001_mirror  label="axisPlaneNormal_001__cylinder_2_5.5"  # a2plus constraint (typed FeaturePython)
  Object1 = b_cylinder_001_001
  Object2 = b_PlywoodPlate_001_002
  ParentTreeObject = -> b_PlywoodPlate_001_002
  SubElement1 = Face1
  SubElement2 = Face4
  Type = axisPlaneNormal
  directionConstraint = 1
FEATURE [App::FeaturePython] axisPlaneNormal_002  label="axisPlaneNormal_002__PlywoodPlate_003"  # a2plus constraint (typed FeaturePython)
  Object1 = b_cylinder_001_
  Object2 = b_PlywoodPlate_001_002
  ParentTreeObject = -> b_cylinder_001_
  SubElement1 = Face1
  SubElement2 = Face4
  Type = axisPlaneNormal
  directionConstraint = 1
FEATURE [App::FeaturePython] axisPlaneNormal_002_mirror  label="axisPlaneNormal_002__cylinder_1_5.5"  # a2plus constraint (typed FeaturePython)
  Object1 = b_cylinder_001_
  Object2 = b_PlywoodPlate_001_002
  ParentTreeObject = -> b_PlywoodPlate_001_002
  SubElement1 = Face1
  SubElement2 = Face4
  Type = axisPlaneNormal
  directionConstraint = 1
FEATURE [App::FeaturePython] axisPlaneNormal_003  label="axisPlaneNormal_003__PlywoodPlate_004"  # a2plus constraint (typed FeaturePython)
  Object1 = b_cylinder_001_002
  Object2 = b_PlywoodPlate_001_003
  ParentTreeObject = -> b_cylinder_001_002
  SubElement1 = Face1
  SubElement2 = Face5
  Type = axisPlaneNormal
  directionConstraint = 0
FEATURE [App::FeaturePython] axisPlaneNormal_003_mirror  label="axisPlaneNormal_003__cylinder_001"  # a2plus constraint (typed FeaturePython)
  Object1 = b_cylinder_001_002
  Object2 = b_PlywoodPlate_001_003
  ParentTreeObject = -> b_PlywoodPlate_001_003
  SubElement1 = Face1
  SubElement2 = Face5
  Type = axisPlaneNormal
  directionConstraint = 0
FEATURE [App::FeaturePython] axisCoincident_015  label="axisCoincident_015__cylinder_001"  # a2plus constraint (typed FeaturePython)
  Object1 = b_gear_1__7_5_48_5_001_
  Object2 = b_cylinder_001_002
  ParentTreeObject = -> b_gear_1__7_5_48_5_001_
  SubElement1 = Face5
  SubElement2 = Face1
  Type = axial
  directionConstraint = 1
  lockRotation = false
FEATURE [App::FeaturePython] axisCoincident_015_mirror  label="axisCoincident_015__gear_1_ 7.5_48.5_001"  # a2plus constraint (typed FeaturePython)
  Object1 = b_gear_1__7_5_48_5_001_
  Object2 = b_cylinder_001_002
  ParentTreeObject = -> b_cylinder_001_002
  SubElement1 = Face5
  SubElement2 = Face1
  Type = axial
  directionConstraint = 1
  lockRotation = false
FEATURE [App::FeaturePython] planeCoincident_030  label="planeCoincident_030__PlywoodPlate_004"  # a2plus constraint (typed FeaturePython)
  Object1 = b_gear_1__7_5_48_5_001_
  Object2 = b_PlywoodPlate_001_003
  ParentTreeObject = -> b_gear_1__7_5_48_5_001_
  SubElement1 = Face2
  SubElement2 = Face5
  Type = plane
  directionConstraint = 0
  offset = 0
FEATURE [App::FeaturePython] planeCoincident_030_mirror  label="planeCoincident_030__gear_1_ 7.5_48.5_001"  # a2plus constraint (typed FeaturePython)
  Object1 = b_gear_1__7_5_48_5_001_
  Object2 = b_PlywoodPlate_001_003
  ParentTreeObject = -> b_PlywoodPlate_001_003
  SubElement1 = Face2
  SubElement2 = Face5
  Type = plane
  directionConstraint = 0
  offset = 0
FEATURE [App::FeaturePython] axisCoincident_016  label="axisCoincident_016__cylinder_001"  # a2plus constraint (typed FeaturePython)
  Object1 = b_gear_3__7_5_43_5_001_
  Object2 = b_cylinder_001_002
  ParentTreeObject = -> b_gear_3__7_5_43_5_001_
  SubElement1 = Face4
  SubElement2 = Face1
  Type = axial
  directionConstraint = 0
  lockRotation = false
FEATURE [App::FeaturePython] axisCoincident_016_mirror  label="axisCoincident_016__gear_3_ 7.5_43.5_001"  # a2plus constraint (typed FeaturePython)
  Object1 = b_gear_3__7_5_43_5_001_
  Object2 = b_cylinder_001_002
  ParentTreeObject = -> b_cylinder_001_002
  SubElement1 = Face4
  SubElement2 = Face1
  Type = axial
  directionConstraint = 0
  lockRotation = false
FEATURE [App::FeaturePython] planeCoincident_034  label="planeCoincident_034__PlywoodPlate_002"  # a2plus constraint (typed FeaturePython)
  Object1 = b_gear_3__7_5_43_5_001_
  Object2 = b_PlywoodPlate_001_001
  ParentTreeObject = -> b_gear_3__7_5_43_5_001_
  SubElement1 = Face2
  SubElement2 = Face5
  Type = plane
  directionConstraint = 0
  offset = 0
FEATURE [App::FeaturePython] planeCoincident_034_mirror  label="planeCoincident_034__gear_3_ 7.5_43.5_001"  # a2plus constraint (typed FeaturePython)
  Object1 = b_gear_3__7_5_43_5_001_
  Object2 = b_PlywoodPlate_001_001
  ParentTreeObject = -> b_PlywoodPlate_001_001
  SubElement1 = Face2
  SubElement2 = Face5
  Type = plane
  directionConstraint = 0
  offset = 0
FEATURE [App::FeaturePython] axisCoincident_017  label="axisCoincident_017__cylinder_001"  # a2plus constraint (typed FeaturePython)
  Object1 = b_gear_2__7_5_41_5_001_
  Object2 = b_cylinder_001_002
  ParentTreeObject = -> b_gear_2__7_5_41_5_001_
  SubElement1 = Face4
  SubElement2 = Face1
  Type = axial
  directionConstraint = 1
  lockRotation = false
FEATURE [App::FeaturePython] axisCoincident_017_mirror  label="axisCoincident_017__gear_2_ 7.5_41.5_001"  # a2plus constraint (typed FeaturePython)
  Object1 = b_gear_2__7_5_41_5_001_
  Object2 = b_cylinder_001_002
  ParentTreeObject = -> b_cylinder_001_002
  SubElement1 = Face4
  SubElement2 = Face1
  Type = axial
  directionConstraint = 1
  lockRotation = false
FEATURE [Part::FeaturePython] b_bed_001_  label="bed_001"  # a2plus imported part (geometry in sourceFile) (typed FeaturePython)
  Placement = pos=(-196.218,124.903,-101.687) rot=(1,0,0;3.14159rad)
  a2p_Version = V0.1
  fixedPosition = false
  sourceFile = ./../Cylinders_Z/bed.FCStd
  subassemblyImport = false
  timeLastImport = 1.56087e+09
  updateColors = true
FEATURE [App::FeaturePython] axisCoincident_018  label="axisCoincident_018__threadedRod_001"  # a2plus constraint (typed FeaturePython)
  Object1 = b_bed_001_
  Object2 = b_threadedRod_001_
  ParentTreeObject = -> b_bed_001_
  SubElement1 = Face13
  SubElement2 = Face1
  Type = axial
  directionConstraint = 0
  lockRotation = false
FEATURE [App::FeaturePython] axisCoincident_018_mirror  label="axisCoincident_018__bed_001"  # a2plus constraint (typed FeaturePython)
  Object1 = b_bed_001_
  Object2 = b_threadedRod_001_
  ParentTreeObject = -> b_threadedRod_001_
  SubElement1 = Face13
  SubElement2 = Face1
  Type = axial
  directionConstraint = 0
  lockRotation = false
FEATURE [App::FeaturePython] axisCoincident_019  label="axisCoincident_019__bed_001"  # a2plus constraint (typed FeaturePython)
  Object1 = b_cylinder_001_001
  Object2 = b_bed_001_
  ParentTreeObject = -> b_cylinder_001_001
  SubElement1 = Face1
  SubElement2 = Face14
  Type = axial
  directionConstraint = 0
  lockRotation = false
FEATURE [App::FeaturePython] axisCoincident_019_mirror  label="axisCoincident_019__cylinder_2_5.5"  # a2plus constraint (typed FeaturePython)
  Object1 = b_cylinder_001_001
  Object2 = b_bed_001_
  ParentTreeObject = -> b_bed_001_
  SubElement1 = Face1
  SubElement2 = Face14
  Type = axial
  directionConstraint = 0
  lockRotation = false
FEATURE [App::FeaturePython] axisCoincident_020  label="axisCoincident_020__bed_001"  # a2plus constraint (typed FeaturePython)
  Object1 = b_cylinder_001_
  Object2 = b_bed_001_
  ParentTreeObject = -> b_cylinder_001_
  SubElement1 = Face1
  SubElement2 = Face12
  Type = axial
  directionConstraint = 0
  lockRotation = false
FEATURE [App::FeaturePython] axisCoincident_020_mirror  label="axisCoincident_020__cylinder_1_5.5"  # a2plus constraint (typed FeaturePython)
  Object1 = b_cylinder_001_
  Object2 = b_bed_001_
  ParentTreeObject = -> b_bed_001_
  SubElement1 = Face1
  SubElement2 = Face12
  Type = axial
  directionConstraint = 0
  lockRotation = false
FEATURE [App::FeaturePython] planeCoincident_037  label="planeCoincident_037__bed_001"  # a2plus constraint (typed FeaturePython)
  Object1 = b_fixator_2_001_
  Object2 = b_bed_001_
  ParentTreeObject = -> b_fixator_2_001_
  SubElement1 = Face2
  SubElement2 = Face5
  Type = plane
  directionConstraint = 0
  offset = 0
FEATURE [App::FeaturePython] planeCoincident_037_mirror  label="planeCoincident_037__fixator_2_001"  # a2plus constraint (typed FeaturePython)
  Object1 = b_fixator_2_001_
  Object2 = b_bed_001_
  ParentTreeObject = -> b_bed_001_
  SubElement1 = Face2
  SubElement2 = Face5
  Type = plane
  directionConstraint = 0
  offset = 0
FEATURE [App::FeaturePython] planeCoincident_039  label="planeCoincident_039__bed_001"  # a2plus constraint (typed FeaturePython)
  Object1 = b_fixator_2_001_001
  Object2 = b_bed_001_
  ParentTreeObject = -> b_fixator_2_001_001
  SubElement1 = Face2
  SubElement2 = Face5
  Type = plane
  directionConstraint = 0
  offset = 0
FEATURE [App::FeaturePython] planeCoincident_039_mirror  label="planeCoincident_039__fixator_2_002"  # a2plus constraint (typed FeaturePython)
  Object1 = b_fixator_2_001_001
  Object2 = b_bed_001_
  ParentTreeObject = -> b_bed_001_
  SubElement1 = Face2
  SubElement2 = Face5
  Type = plane
  directionConstraint = 0
  offset = 0
FEATURE [App::FeaturePython] axisCoincident_021  label="axisCoincident_021__bed_001"  # a2plus constraint (typed FeaturePython)
  Object1 = b_cylinder_001_002
  Object2 = b_bed_001_
  ParentTreeObject = -> b_cylinder_001_002
  SubElement1 = Face1
  SubElement2 = Face11
  Type = axial
  directionConstraint = 0
  lockRotation = false
FEATURE [App::FeaturePython] axisCoincident_021_mirror  label="axisCoincident_021__cylinder_001"  # a2plus constraint (typed FeaturePython)
  Object1 = b_cylinder_001_002
  Object2 = b_bed_001_
  ParentTreeObject = -> b_bed_001_
  SubElement1 = Face1
  SubElement2 = Face11
  Type = axial
  directionConstraint = 0
  lockRotation = false
FEATURE [App::FeaturePython] planeCoincident_040  label="planeCoincident_040__bed_001"  # a2plus constraint (typed FeaturePython)
  Object1 = b_gear_2__7_5_41_5_001_
  Object2 = b_bed_001_
  ParentTreeObject = -> b_gear_2__7_5_41_5_001_
  SubElement1 = Face3
  SubElement2 = Face15
  Type = plane
  directionConstraint = 1
  offset = 0
FEATURE [App::FeaturePython] planeCoincident_040_mirror  label="planeCoincident_040__gear_2_ 7.5_41.5_001"  # a2plus constraint (typed FeaturePython)
  Object1 = b_gear_2__7_5_41_5_001_
  Object2 = b_bed_001_
  ParentTreeObject = -> b_bed_001_
  SubElement1 = Face3
  SubElement2 = Face15
  Type = plane
  directionConstraint = 1
  offset = 0
FEATURE [Part::FeaturePython] b_NEMA_23_Stepper_Motor_001_  label="NEMA-23_Stepper_Motor_001"  # a2plus imported part (geometry in sourceFile) (typed FeaturePython)
  Placement = pos=(-172.882,5.83227,13.6) rot=(0.862856,-0.357407,-0.357407;1.71777rad)
  a2p_Version = V0.1
  fixedPosition = false
  sourceFile = .\..\Motors\NEMA-23_Stepper_Motor.fcstd
  subassemblyImport = false
  timeLastImport = 1.56017e+09
  updateColors = true
FEATURE [App::DocumentObjectGroup] Group007  label="Z-axis"
  Group = -> [b_threadedRod_001_,b_cylinder_001_,b_cylinder_001_001,b_fixator_2_001_,b_gear1_5_5x33_5_001_,b_gear2_5_5x17_001_,b_fixator_2_001_001,b_gear1_5_5x33_5_001_001,b_gear2_5_5x17_001_001,b_cylinder_001_002,b_gear_1__7_5_48_5_001_,b_gear_2__7_5_41_5_001_,b_gear_3__7_5_43_5_001_,b_bed_001_,b_NEMA_23_Stepper_Motor_001_]
FEATURE [App::FeaturePython] planeCoincident_041  label="planeCoincident_041__PlywoodPlate_001"  # a2plus constraint (typed FeaturePython)
  Object1 = b_NEMA_23_Stepper_Motor_001_
  Object2 = b_PlywoodPlate_001_
  ParentTreeObject = -> b_NEMA_23_Stepper_Motor_001_
  SubElement1 = Face6
  SubElement2 = Face4
  Type = plane
  directionConstraint = 1
  offset = 0
FEATURE [App::FeaturePython] planeCoincident_041_mirror  label="planeCoincident_041__NEMA-23_Stepper_Motor_001"  # a2plus constraint (typed FeaturePython)
  Object1 = b_NEMA_23_Stepper_Motor_001_
  Object2 = b_PlywoodPlate_001_
  ParentTreeObject = -> b_PlywoodPlate_001_
  SubElement1 = Face6
  SubElement2 = Face4
  Type = plane
  directionConstraint = 1
  offset = 0
FEATURE [App::FeaturePython] planesParallel_007  label="planesParallel_007__Case_001"  # a2plus constraint (typed FeaturePython)
  Object1 = b_carrier1_11_5_001_
  Object2 = b_Case_001_
  ParentTreeObject = -> b_carrier1_11_5_001_
  SubElement1 = Face15
  SubElement2 = Face4
  Type = planesParallel
  directionConstraint = 0
FEATURE [App::FeaturePython] planesParallel_007_mirror  label="planesParallel_007__carrier1_11.5_001"  # a2plus constraint (typed FeaturePython)
  Object1 = b_carrier1_11_5_001_
  Object2 = b_Case_001_
  ParentTreeObject = -> b_Case_001_
  SubElement1 = Face15
  SubElement2 = Face4
  Type = planesParallel
  directionConstraint = 0
FEATURE [App::FeaturePython] planesParallel_008  label="planesParallel_008__Case_001"  # a2plus constraint (typed FeaturePython)
  Object1 = b_carrier2_7_5_benq_001_
  Object2 = b_Case_001_
  ParentTreeObject = -> b_carrier2_7_5_benq_001_
  SubElement1 = Face11
  SubElement2 = Face4
  Type = planesParallel
  directionConstraint = 0
FEATURE [App::FeaturePython] planesParallel_008_mirror  label="planesParallel_008__carrier2_7.5_benq_001"  # a2plus constraint (typed FeaturePython)
  Object1 = b_carrier2_7_5_benq_001_
  Object2 = b_Case_001_
  ParentTreeObject = -> b_Case_001_
  SubElement1 = Face11
  SubElement2 = Face4
  Type = planesParallel
  directionConstraint = 0
FEATURE [App::FeaturePython] planesParallel_001  label="planesParallel_001__Case_001"  # a2plus constraint (typed FeaturePython)
  Object1 = b_carrier4_6_7_lexm_001_
  Object2 = b_Case_001_
  ParentTreeObject = -> b_carrier4_6_7_lexm_001_
  SubElement1 = Face7
  SubElement2 = Face4
  Type = planesParallel
  directionConstraint = 1
FEATURE [App::FeaturePython] planesParallel_001_mirror  label="planesParallel_001__carrier4_6.7_lexm_001"  # a2plus constraint (typed FeaturePython)
  Object1 = b_carrier4_6_7_lexm_001_
  Object2 = b_Case_001_
  ParentTreeObject = -> b_Case_001_
  SubElement1 = Face7
  SubElement2 = Face4
  Type = planesParallel
  directionConstraint = 1
FEATURE [App::FeaturePython] planesParallel_002  label="planesParallel_002__carrier3_001"  # a2plus constraint (typed FeaturePython)
  Object1 = b_carrier4_6_7_lexm_001_
  Object2 = b_carrier3_001_
  ParentTreeObject = -> b_carrier4_6_7_lexm_001_
  SubElement1 = Face7
  SubElement2 = Face4
  Type = planesParallel
  directionConstraint = 0
FEATURE [App::FeaturePython] planesParallel_002_mirror  label="planesParallel_002__carrier4_6.7_lexm_001"  # a2plus constraint (typed FeaturePython)
  Object1 = b_carrier4_6_7_lexm_001_
  Object2 = b_carrier3_001_
  ParentTreeObject = -> b_carrier3_001_
  SubElement1 = Face7
  SubElement2 = Face4
  Type = planesParallel
  directionConstraint = 0
FEATURE [App::FeaturePython] axisCoincident_003  label="axisCoincident_003__cylinder4_6.7_001"  # a2plus constraint (typed FeaturePython)
  Object1 = b_carrier4_6_7_lexm_001_
  Object2 = b_cylinder4_6_7_001_
  ParentTreeObject = -> b_carrier4_6_7_lexm_001_
  SubElement1 = Face11
  SubElement2 = Face1
  Type = axial
  directionConstraint = 1
  lockRotation = false
FEATURE [App::FeaturePython] axisCoincident_003_mirror  label="axisCoincident_003__carrier4_6.7_lexm_001"  # a2plus constraint (typed FeaturePython)
  Object1 = b_carrier4_6_7_lexm_001_
  Object2 = b_cylinder4_6_7_001_
  ParentTreeObject = -> b_cylinder4_6_7_001_
  SubElement1 = Face11
  SubElement2 = Face1
  Type = axial
  directionConstraint = 1
  lockRotation = false
FEATURE [Part::FeaturePython] b_videocard_Radiator_001_  label="videocard_Radiator_001"  # a2plus imported part (geometry in sourceFile) (typed FeaturePython)
  Placement = pos=(-28.3222,-69.8152,-0.750607) rot=(-0.039256,-1e-06,-0.999229;0rad)
  a2p_Version = V0.1
  fixedPosition = false
  sourceFile = ./../Carrieges/videocard_Radiator.FCStd
  subassemblyImport = false
  timeLastImport = 1.56044e+09
  updateColors = true
FEATURE [App::DocumentObjectGroup] Group002  label="Carriers"
  Group = -> [b_carrier1_11_5_001_,b_carrier2_7_5_benq_001_,b_carrier4_6_7_lexm_001_,b_carrier3_001_,b_videocard_Radiator_001_]
FEATURE [App::FeaturePython] planeCoincident_021  label="planeCoincident_021__carrier4_6.7_lexm_001"  # a2plus constraint (typed FeaturePython)
  Object1 = b_videocard_Radiator_001_
  Object2 = b_carrier4_6_7_lexm_001_
  ParentTreeObject = -> b_videocard_Radiator_001_
  SubElement1 = Face167
  SubElement2 = Face7
  Type = plane
  directionConstraint = 1
  offset = 0
FEATURE [App::FeaturePython] planeCoincident_021_mirror  label="planeCoincident_021__videocard_Radiator_001"  # a2plus constraint (typed FeaturePython)
  Object1 = b_videocard_Radiator_001_
  Object2 = b_carrier4_6_7_lexm_001_
  ParentTreeObject = -> b_carrier4_6_7_lexm_001_
  SubElement1 = Face167
  SubElement2 = Face7
  Type = plane
  directionConstraint = 1
  offset = 0
FEATURE [App::FeaturePython] planeCoincident_044  label="planeCoincident_044__carrier3_001"  # a2plus constraint (typed FeaturePython)
  Object1 = b_videocard_Radiator_001_
  Object2 = b_carrier3_001_
  ParentTreeObject = -> b_videocard_Radiator_001_
  SubElement1 = Face3
  SubElement2 = Face5
  Type = plane
  directionConstraint = 0
  offset = 0
FEATURE [App::FeaturePython] planeCoincident_044_mirror  label="planeCoincident_044__videocard_Radiator_001"  # a2plus constraint (typed FeaturePython)
  Object1 = b_videocard_Radiator_001_
  Object2 = b_carrier3_001_
  ParentTreeObject = -> b_carrier3_001_
  SubElement1 = Face3
  SubElement2 = Face5
  Type = plane
  directionConstraint = 0
  offset = 0
FEATURE [App::FeaturePython] planeCoincident_045  label="planeCoincident_045__carrier3_001"  # a2plus constraint (typed FeaturePython)
  Object1 = b_videocard_Radiator_001_
  Object2 = b_carrier3_001_
  ParentTreeObject = -> b_videocard_Radiator_001_
  SubElement1 = Face163
  SubElement2 = Face11
  Type = plane
  directionConstraint = 1
  offset = 0
FEATURE [App::FeaturePython] planeCoincident_045_mirror  label="planeCoincident_045__videocard_Radiator_001"  # a2plus constraint (typed FeaturePython)
  Object1 = b_videocard_Radiator_001_
  Object2 = b_carrier3_001_
  ParentTreeObject = -> b_carrier3_001_
  SubElement1 = Face163
  SubElement2 = Face11
  Type = plane
  directionConstraint = 1
  offset = 0
FEATURE [Part::FeaturePython] b_j_head_001_  label="j-head_001"  # a2plus imported part (geometry in sourceFile) (typed FeaturePython)
  Placement = pos=(6.29892,-34.1987,-31.3506) rot=(0,0,1;0rad)
  a2p_Version = V0.1
  fixedPosition = false
  sourceFile = ./../Hotend/j-head.FCStd
  subassemblyImport = false
  timeLastImport = 1558947838
  updateColors = true
FEATURE [App::FeaturePython] planeCoincident_046  label="planeCoincident_046__videocard_Radiator_001"  # a2plus constraint (typed FeaturePython)
  Object1 = b_j_head_001_
  Object2 = b_videocard_Radiator_001_
  ParentTreeObject = -> b_j_head_001_
  SubElement1 = Face20
  SubElement2 = Face167
  Type = plane
  directionConstraint = 0
  offset = 0
FEATURE [App::FeaturePython] planeCoincident_046_mirror  label="planeCoincident_046__j-head_001"  # a2plus constraint (typed FeaturePython)
  Object1 = b_j_head_001_
  Object2 = b_videocard_Radiator_001_
  ParentTreeObject = -> b_videocard_Radiator_001_
  SubElement1 = Face20
  SubElement2 = Face167
  Type = plane
  directionConstraint = 0
  offset = 0
FEATURE [App::FeaturePython] axisCoincident_001  label="axisCoincident_001__UPS_radiator_001"  # a2plus constraint (typed FeaturePython)
  Object1 = b_cylinder4_6_7_001_
  Object2 = b_UPS_radiator_001_
  ParentTreeObject = -> b_cylinder4_6_7_001_
  SubElement1 = Face1
  SubElement2 = Face39
  Type = axial
  directionConstraint = 1
  lockRotation = false
FEATURE [App::FeaturePython] axisCoincident_001_mirror  label="axisCoincident_001__cylinder4_6.7_001"  # a2plus constraint (typed FeaturePython)
  Object1 = b_cylinder4_6_7_001_
  Object2 = b_UPS_radiator_001_
  ParentTreeObject = -> b_UPS_radiator_001_
  SubElement1 = Face1
  SubElement2 = Face39
  Type = axial
  directionConstraint = 1
  lockRotation = false
FEATURE [App::FeaturePython] axisCoincident_004  label="axisCoincident_004__UPS_radiator_001"  # a2plus constraint (typed FeaturePython)
  Object1 = b_cylinder3_6_5_001_
  Object2 = b_UPS_radiator_001_
  ParentTreeObject = -> b_cylinder3_6_5_001_
  SubElement1 = Face1
  SubElement2 = Face30
  Type = axial
  directionConstraint = 0
  lockRotation = false
FEATURE [App::FeaturePython] axisCoincident_004_mirror  label="axisCoincident_004__cylinder3_6.5_001"  # a2plus constraint (typed FeaturePython)
  Object1 = b_cylinder3_6_5_001_
  Object2 = b_UPS_radiator_001_
  ParentTreeObject = -> b_UPS_radiator_001_
  SubElement1 = Face1
  SubElement2 = Face30
  Type = axial
  directionConstraint = 0
  lockRotation = false
FEATURE [App::FeaturePython] circularEdge_006_mirror001  label="circularEdge_006__rollerAssembly1_002"  # a2plus constraint (typed FeaturePython)
  Object1 = b_rollerAssembly1_001_001
  Object2 = b_UPS_radiator_001_
  ParentTreeObject = -> b_UPS_radiator_001_
  SubElement1 = Edge7
  SubElement2 = Edge84
  Type = circularEdge
  directionConstraint = 0
  lockRotation = false
  offset = 0
FEATURE [App::FeaturePython] planeCoincident_004  label="planeCoincident_004__carrier2_7.5_benq_001"  # a2plus constraint (typed FeaturePython)
  Object1 = b_UPS_radiator_001_
  Object2 = b_carrier2_7_5_benq_001_
  ParentTreeObject = -> b_UPS_radiator_001_
  SubElement1 = Face1
  SubElement2 = Face11
  Type = plane
  directionConstraint = 0
  offset = 0
FEATURE [App::FeaturePython] planeCoincident_004_mirror  label="planeCoincident_004__UPS_radiator_001"  # a2plus constraint (typed FeaturePython)
  Object1 = b_UPS_radiator_001_
  Object2 = b_carrier2_7_5_benq_001_
  ParentTreeObject = -> b_carrier2_7_5_benq_001_
  SubElement1 = Face1
  SubElement2 = Face11
  Type = plane
  directionConstraint = 0
  offset = 0
FEATURE [App::FeaturePython] planeCoincident_005  label="planeCoincident_005__carrier2_7.5_benq_001"  # a2plus constraint (typed FeaturePython)
  Object1 = b_UPS_radiator_001_
  Object2 = b_carrier2_7_5_benq_001_
  ParentTreeObject = -> b_UPS_radiator_001_
  SubElement1 = Face2
  SubElement2 = Face2
  Type = plane
  directionConstraint = 0
  offset = 0
FEATURE [App::FeaturePython] planeCoincident_005_mirror  label="planeCoincident_005__UPS_radiator_001"  # a2plus constraint (typed FeaturePython)
  Object1 = b_UPS_radiator_001_
  Object2 = b_carrier2_7_5_benq_001_
  ParentTreeObject = -> b_carrier2_7_5_benq_001_
  SubElement1 = Face2
  SubElement2 = Face2
  Type = plane
  directionConstraint = 0
  offset = 0
FEATURE [App::FeaturePython] planeCoincident_006  label="planeCoincident_006__carrier2_7.5_benq_001"  # a2plus constraint (typed FeaturePython)
  Object1 = b_UPS_radiator_001_
  Object2 = b_carrier2_7_5_benq_001_
  ParentTreeObject = -> b_UPS_radiator_001_
  SubElement1 = Face4
  SubElement2 = Face10
  Type = plane
  directionConstraint = 0
  offset = 0
FEATURE [App::FeaturePython] planeCoincident_006_mirror  label="planeCoincident_006__UPS_radiator_001"  # a2plus constraint (typed FeaturePython)
  Object1 = b_UPS_radiator_001_
  Object2 = b_carrier2_7_5_benq_001_
  ParentTreeObject = -> b_carrier2_7_5_benq_001_
  SubElement1 = Face4
  SubElement2 = Face10
  Type = plane
  directionConstraint = 0
  offset = 0
FEATURE [App::FeaturePython] axisCoincident_005  label="axisCoincident_005__UPS_radiator_002"  # a2plus constraint (typed FeaturePython)
  Object1 = b_cylinder3_6_5_001_
  Object2 = b_UPS_radiator_001_001
  ParentTreeObject = -> b_cylinder3_6_5_001_
  SubElement1 = Face1
  SubElement2 = Face39
  Type = axial
  directionConstraint = 1
  lockRotation = false
FEATURE [App::FeaturePython] axisCoincident_005_mirror  label="axisCoincident_005__cylinder3_6.5_001"  # a2plus constraint (typed FeaturePython)
  Object1 = b_cylinder3_6_5_001_
  Object2 = b_UPS_radiator_001_001
  ParentTreeObject = -> b_UPS_radiator_001_001
  SubElement1 = Face1
  SubElement2 = Face39
  Type = axial
  directionConstraint = 1
  lockRotation = false
FEATURE [App::FeaturePython] axisCoincident_007  label="axisCoincident_007__UPS_radiator_002"  # a2plus constraint (typed FeaturePython)
  Object1 = b_cylinder4_6_7_001_
  Object2 = b_UPS_radiator_001_001
  ParentTreeObject = -> b_cylinder4_6_7_001_
  SubElement1 = Face1
  SubElement2 = Face30
  Type = axial
  directionConstraint = 0
  lockRotation = false
FEATURE [App::FeaturePython] axisCoincident_007_mirror  label="axisCoincident_007__cylinder4_6.7_001"  # a2plus constraint (typed FeaturePython)
  Object1 = b_cylinder4_6_7_001_
  Object2 = b_UPS_radiator_001_001
  ParentTreeObject = -> b_UPS_radiator_001_001
  SubElement1 = Face1
  SubElement2 = Face30
  Type = axial
  directionConstraint = 0
  lockRotation = false
FEATURE [App::FeaturePython] planeCoincident_007  label="planeCoincident_007__carrier1_11.5_001"  # a2plus constraint (typed FeaturePython)
  Object1 = b_UPS_radiator_001_001
  Object2 = b_carrier1_11_5_001_
  ParentTreeObject = -> b_UPS_radiator_001_001
  SubElement1 = Face1
  SubElement2 = Face15
  Type = plane
  directionConstraint = 0
  offset = 0
FEATURE [App::FeaturePython] planeCoincident_007_mirror  label="planeCoincident_007__UPS_radiator_002"  # a2plus constraint (typed FeaturePython)
  Object1 = b_UPS_radiator_001_001
  Object2 = b_carrier1_11_5_001_
  ParentTreeObject = -> b_carrier1_11_5_001_
  SubElement1 = Face1
  SubElement2 = Face15
  Type = plane
  directionConstraint = 0
  offset = 0
FEATURE [App::FeaturePython] planeCoincident_008  label="planeCoincident_008__UPS_radiator_002"  # a2plus constraint (typed FeaturePython)
  Object1 = b_carrier1_11_5_001_
  Object2 = b_UPS_radiator_001_001
  ParentTreeObject = -> b_carrier1_11_5_001_
  SubElement1 = Face24
  SubElement2 = Face4
  Type = plane
  directionConstraint = 0
  offset = 0
FEATURE [App::FeaturePython] planeCoincident_008_mirror  label="planeCoincident_008__carrier1_11.5_001"  # a2plus constraint (typed FeaturePython)
  Object1 = b_carrier1_11_5_001_
  Object2 = b_UPS_radiator_001_001
  ParentTreeObject = -> b_UPS_radiator_001_001
  SubElement1 = Face24
  SubElement2 = Face4
  Type = plane
  directionConstraint = 0
  offset = 0
FEATURE [App::FeaturePython] planeCoincident_012  label="planeCoincident_012__carrier1_11.5_001"  # a2plus constraint (typed FeaturePython)
  Object1 = b_UPS_radiator_001_001
  Object2 = b_carrier1_11_5_001_
  ParentTreeObject = -> b_UPS_radiator_001_001
  SubElement1 = Face5
  SubElement2 = Face25
  Type = plane
  directionConstraint = 0
  offset = 0
FEATURE [App::FeaturePython] planeCoincident_012_mirror  label="planeCoincident_012__UPS_radiator_002"  # a2plus constraint (typed FeaturePython)
  Object1 = b_UPS_radiator_001_001
  Object2 = b_carrier1_11_5_001_
  ParentTreeObject = -> b_carrier1_11_5_001_
  SubElement1 = Face5
  SubElement2 = Face25
  Type = plane
  directionConstraint = 0
  offset = 0
FEATURE [Part::FeaturePython] b_sqware_pad__8_001_  label="sqware_pad__8_001"  # a2plus imported part (geometry in sourceFile) (typed FeaturePython)
  Placement = pos=(202.547,-198,-51.8006) rot=(0.57735,0.57735,0.57735;2.0944rad)
  a2p_Version = V0.1
  fixedPosition = false
  sourceFile = ./../fasteners/sqware_pad__8.FCStd
  subassemblyImport = false
  timeLastImport = 1.56052e+09
  updateColors = true
FEATURE [Part::FeaturePython] b_sqware_pad__8_001_001  label="sqware_pad__8_002"  # a2plus imported part (geometry in sourceFile) (typed FeaturePython)
  Placement = pos=(-172.853,-198,-51.8006) rot=(0.57735,0.57735,0.57735;2.0944rad)
  a2p_Version = V0.1
  fixedPosition = false
  sourceFile = ./../fasteners/sqware_pad__8.FCStd
  subassemblyImport = false
  timeLastImport = 1.56052e+09
  updateColors = true
FEATURE [Part::FeaturePython] b_sqware_pad_001_  label="sqware_pad_001"  # a2plus imported part (geometry in sourceFile) (typed FeaturePython)
  Placement = pos=(-172.853,198,-7.49931) rot=(-0.57735,0.57735,-0.57735;2.0944rad)
  a2p_Version = V0.1
  fixedPosition = false
  sourceFile = ./../fasteners/sqware_pad__12.FCStd
  subassemblyImport = false
  timeLastImport = 1.56052e+09
  updateColors = true
FEATURE [Part::FeaturePython] b_sqware_pad_001_001  label="sqware_pad_002"  # a2plus imported part (geometry in sourceFile) (typed FeaturePython)
  Placement = pos=(195.547,160,-47.4993) rot=(0.57735,0.57735,0.57735;2.0944rad)
  a2p_Version = V0.1
  fixedPosition = false
  sourceFile = ./../fasteners/sqware_pad__12.FCStd
  subassemblyImport = false
  timeLastImport = 1.56052e+09
  updateColors = true
FEATURE [App::FeaturePython] planeCoincident_015  label="planeCoincident_015__PlywoodPlate_002"  # a2plus constraint (typed FeaturePython)
  Object1 = b_rollerDoubleAssembly_001_
  Object2 = b_PlywoodPlate_001_001
  ParentTreeObject = -> b_rollerDoubleAssembly_001_
  SubElement1 = Face4
  SubElement2 = Face5
  Type = plane
  directionConstraint = 0
  offset = 0
FEATURE [App::FeaturePython] planeCoincident_015_mirror  label="planeCoincident_015__rollerDoubleAssembly_001"  # a2plus constraint (typed FeaturePython)
  Object1 = b_rollerDoubleAssembly_001_
  Object2 = b_PlywoodPlate_001_001
  ParentTreeObject = -> b_PlywoodPlate_001_001
  SubElement1 = Face4
  SubElement2 = Face5
  Type = plane
  directionConstraint = 0
  offset = 0
FEATURE [App::FeaturePython] planeCoincident_019  label="planeCoincident_019__PlywoodPlate_002"  # a2plus constraint (typed FeaturePython)
  Object1 = b_rollerDoubleAssembly_001_001
  Object2 = b_PlywoodPlate_001_001
  ParentTreeObject = -> b_rollerDoubleAssembly_001_001
  SubElement1 = Face4
  SubElement2 = Face5
  Type = plane
  directionConstraint = 0
  offset = 0
FEATURE [App::FeaturePython] planeCoincident_019_mirror  label="planeCoincident_019__rollerDoubleAssembly_002"  # a2plus constraint (typed FeaturePython)
  Object1 = b_rollerDoubleAssembly_001_001
  Object2 = b_PlywoodPlate_001_001
  ParentTreeObject = -> b_PlywoodPlate_001_001
  SubElement1 = Face4
  SubElement2 = Face5
  Type = plane
  directionConstraint = 0
  offset = 0
FEATURE [App::FeaturePython] axisParallel_005  label="axisParallel_005__PlywoodPlate_002"  # a2plus constraint (typed FeaturePython)
  Object1 = b_rollerDoubleAssembly_001_
  Object2 = b_PlywoodPlate_001_001
  ParentTreeObject = -> b_rollerDoubleAssembly_001_
  SubElement1 = Edge10
  SubElement2 = Edge7
  Type = axisParallel
  directionConstraint = 0
FEATURE [App::FeaturePython] axisParallel_005_mirror  label="axisParallel_005__rollerDoubleAssembly_001"  # a2plus constraint (typed FeaturePython)
  Object1 = b_rollerDoubleAssembly_001_
  Object2 = b_PlywoodPlate_001_001
  ParentTreeObject = -> b_PlywoodPlate_001_001
  SubElement1 = Edge10
  SubElement2 = Edge7
  Type = axisParallel
  directionConstraint = 0
FEATURE [App::FeaturePython] axisParallel_006  label="axisParallel_006__PlywoodPlate_002"  # a2plus constraint (typed FeaturePython)
  Object1 = b_rollerDoubleAssembly_001_001
  Object2 = b_PlywoodPlate_001_001
  ParentTreeObject = -> b_rollerDoubleAssembly_001_001
  SubElement1 = Edge10
  SubElement2 = Edge4
  Type = axisParallel
  directionConstraint = 0
FEATURE [App::FeaturePython] axisParallel_006_mirror  label="axisParallel_006__rollerDoubleAssembly_002"  # a2plus constraint (typed FeaturePython)
  Object1 = b_rollerDoubleAssembly_001_001
  Object2 = b_PlywoodPlate_001_001
  ParentTreeObject = -> b_PlywoodPlate_001_001
  SubElement1 = Edge10
  SubElement2 = Edge4
  Type = axisParallel
  directionConstraint = 0
FEATURE [App::FeaturePython] planeCoincident_020  label="planeCoincident_020__rollerAssembly2_001"  # a2plus constraint (typed FeaturePython)
  Object1 = b_rollerDoubleAssembly_001_001
  Object2 = b_rollerAssembly2_001_
  ParentTreeObject = -> b_rollerDoubleAssembly_001_001
  SubElement1 = Face38
  SubElement2 = Face23
  Type = plane
  directionConstraint = 0
  offset = 0
FEATURE [App::FeaturePython] planeCoincident_020_mirror  label="planeCoincident_020__rollerDoubleAssembly_002"  # a2plus constraint (typed FeaturePython)
  Object1 = b_rollerDoubleAssembly_001_001
  Object2 = b_rollerAssembly2_001_
  ParentTreeObject = -> b_rollerAssembly2_001_
  SubElement1 = Face38
  SubElement2 = Face23
  Type = plane
  directionConstraint = 0
  offset = 0
FEATURE [App::FeaturePython] planeCoincident_042  label="planeCoincident_042__rollerAssembly1_001"  # a2plus constraint (typed FeaturePython)
  Object1 = b_rollerDoubleAssembly_001_
  Object2 = b_rollerAssembly1_001_
  ParentTreeObject = -> b_rollerDoubleAssembly_001_
  SubElement1 = Face38
  SubElement2 = Face23
  Type = plane
  directionConstraint = 0
  offset = 0
FEATURE [App::FeaturePython] planeCoincident_042_mirror  label="planeCoincident_042__rollerDoubleAssembly_001"  # a2plus constraint (typed FeaturePython)
  Object1 = b_rollerDoubleAssembly_001_
  Object2 = b_rollerAssembly1_001_
  ParentTreeObject = -> b_rollerAssembly1_001_
  SubElement1 = Face38
  SubElement2 = Face23
  Type = plane
  directionConstraint = 0
  offset = 0
FEATURE [App::DocumentObjectGroup] Group009  label="SqwearPads"
  Group = -> [b_sqware_pad__8_001_,b_sqware_pad__8_001_001,b_sqware_pad_001_,b_sqware_pad_001_001]
FEATURE [Part::FeaturePython] b_ISO4762_Hex_Socket_Head_Cap_Screw_M3x16_001_  label="ISO4762_Hex_Socket_Head_Cap_Screw_M3x16_001"  # a2plus imported part (geometry in sourceFile) (typed FeaturePython)
  Placement = pos=(-3.07227,156.262,7.49982) rot=(-0.072562,-0.997364,-2e-05;3e-06rad)
  a2p_Version = V0.1
  fixedPosition = false
  sourceFile = ./../../../Documents/FreeCadProjects/FreeCAD-library/Mechanical Parts/Fasteners/Bolts & Screws/Metric/ISO4762_Hex_Socket_Head_Cap_Screw_M3x16.fcstd
  subassemblyImport = false
  timeLastImport = 1557779266
  updateColors = true
FEATURE [Part::FeaturePython] b_ISO4762_Hex_Socket_Head_Cap_Screw_M3x16_001_001  label="ISO4762_Hex_Socket_Head_Cap_Screw_M3x16_002"  # a2plus imported part (geometry in sourceFile) (typed FeaturePython)
  Placement = pos=(25.428,150.2,7.5) rot=(-0.236847,0.971471,-0.012177;0rad)
  a2p_Version = V0.1
  fixedPosition = false
  sourceFile = ./../../../Documents/FreeCadProjects/FreeCAD-library/Mechanical Parts/Fasteners/Bolts & Screws/Metric/ISO4762_Hex_Socket_Head_Cap_Screw_M3x16.fcstd
  subassemblyImport = false
  timeLastImport = 1557779266
  updateColors = true
FEATURE [Part::FeaturePython] b_ISO4762_Hex_Socket_Head_Cap_Screw_M3x16_001_002  label="ISO4762_Hex_Socket_Head_Cap_Screw_M3x16_003"  # a2plus imported part (geometry in sourceFile) (typed FeaturePython)
  Placement = pos=(21.9279,156.262,7.5) rot=(-0.222046,0.974973,-0.011062;0rad)
  a2p_Version = V0.1
  fixedPosition = false
  sourceFile = ./../../../Documents/FreeCadProjects/FreeCAD-library/Mechanical Parts/Fasteners/Bolts & Screws/Metric/ISO4762_Hex_Socket_Head_Cap_Screw_M3x16.fcstd
  subassemblyImport = false
  timeLastImport = 1557779266
  updateColors = true
FEATURE [Part::FeaturePython] b_ISO4762_Hex_Socket_Head_Cap_Screw_M3x16_001_003  label="ISO4762_Hex_Socket_Head_Cap_Screw_M3x16_004"  # a2plus imported part (geometry in sourceFile) (typed FeaturePython)
  Placement = pos=(-6.57211,150.2,7.49981) rot=(-0.072628,-0.997359,-2e-05;3e-06rad)
  a2p_Version = V0.1
  fixedPosition = false
  sourceFile = ./../../../Documents/FreeCadProjects/FreeCAD-library/Mechanical Parts/Fasteners/Bolts & Screws/Metric/ISO4762_Hex_Socket_Head_Cap_Screw_M3x16.fcstd
  subassemblyImport = false
  timeLastImport = 1557779266
  updateColors = true
FEATURE [Part::FeaturePython] b_ISO4762_Hex_Socket_Head_Cap_Screw_M3x16_001_004  label="ISO4762_Hex_Socket_Head_Cap_Screw_M3x16_005"  # a2plus imported part (geometry in sourceFile) (typed FeaturePython)
  Placement = pos=(-6.57223,-150.5,7.4994) rot=(0,0,1;3.80504rad)
  a2p_Version = V0.1
  fixedPosition = false
  sourceFile = ./../../../Documents/FreeCadProjects/FreeCAD-library/Mechanical Parts/Fasteners/Bolts & Screws/Metric/ISO4762_Hex_Socket_Head_Cap_Screw_M3x16.fcstd
  subassemblyImport = false
  timeLastImport = 1557779266
  updateColors = true
FEATURE [Part::FeaturePython] b_ISO4762_Hex_Socket_Head_Cap_Screw_M3x16_001_005  label="ISO4762_Hex_Socket_Head_Cap_Screw_M3x16_006"  # a2plus imported part (geometry in sourceFile) (typed FeaturePython)
  Placement = pos=(-2.94877,-164.023,7.4994) rot=(0.054906,0.998492,0;0rad)
  a2p_Version = V0.1
  fixedPosition = false
  sourceFile = ./../../../Documents/FreeCadProjects/FreeCAD-library/Mechanical Parts/Fasteners/Bolts & Screws/Metric/ISO4762_Hex_Socket_Head_Cap_Screw_M3x16.fcstd
  subassemblyImport = false
  timeLastImport = 1557779266
  updateColors = true
FEATURE [App::FeaturePython] circularEdge_014  label="circularEdge_014__rollerAssembly1_002"  # a2plus constraint (typed FeaturePython)
  Object1 = b_ISO4762_Hex_Socket_Head_Cap_Screw_M3x16_001_005
  Object2 = b_rollerAssembly1_001_001
  ParentTreeObject = -> b_ISO4762_Hex_Socket_Head_Cap_Screw_M3x16_001_005
  SubElement1 = Edge2
  SubElement2 = Edge24
  Type = circularEdge
  directionConstraint = 1
  lockRotation = false
  offset = 0
FEATURE [App::FeaturePython] circularEdge_014_mirror  label="circularEdge_014__ISO4762_Hex_Socket_Head_Cap_Screw_M3x16_006"  # a2plus constraint (typed FeaturePython)
  Object1 = b_ISO4762_Hex_Socket_Head_Cap_Screw_M3x16_001_005
  Object2 = b_rollerAssembly1_001_001
  ParentTreeObject = -> b_rollerAssembly1_001_001
  SubElement1 = Edge2
  SubElement2 = Edge24
  Type = circularEdge
  directionConstraint = 1
  lockRotation = false
  offset = 0
FEATURE [Part::FeaturePython] b_ISO4762_Hex_Socket_Head_Cap_Screw_M3x16_001_006  label="ISO4762_Hex_Socket_Head_Cap_Screw_M3x16_007"  # a2plus imported part (geometry in sourceFile) (typed FeaturePython)
  Placement = pos=(21.9278,-156.562,6.49959) rot=(0.075184,0.99717,0;0rad)
  a2p_Version = V0.1
  fixedPosition = false
  sourceFile = ./../../../Documents/FreeCadProjects/FreeCAD-library/Mechanical Parts/Fasteners/Bolts & Screws/Metric/ISO4762_Hex_Socket_Head_Cap_Screw_M3x16.fcstd
  subassemblyImport = false
  timeLastImport = 1557779266
  updateColors = true
FEATURE [App::FeaturePython] circularEdge_015  label="circularEdge_015__rollerAssembly2_001"  # a2plus constraint (typed FeaturePython)
  Object1 = b_ISO4762_Hex_Socket_Head_Cap_Screw_M3x16_001_006
  Object2 = b_rollerAssembly2_001_
  ParentTreeObject = -> b_ISO4762_Hex_Socket_Head_Cap_Screw_M3x16_001_006
  SubElement1 = Edge2
  SubElement2 = Edge7
  Type = circularEdge
  directionConstraint = 0
  lockRotation = false
  offset = 0
FEATURE [App::FeaturePython] circularEdge_015_mirror  label="circularEdge_015__ISO4762_Hex_Socket_Head_Cap_Screw_M3x16_007"  # a2plus constraint (typed FeaturePython)
  Object1 = b_ISO4762_Hex_Socket_Head_Cap_Screw_M3x16_001_006
  Object2 = b_rollerAssembly2_001_
  ParentTreeObject = -> b_rollerAssembly2_001_
  SubElement1 = Edge2
  SubElement2 = Edge7
  Type = circularEdge
  directionConstraint = 0
  lockRotation = false
  offset = 0
FEATURE [Part::FeaturePython] b_ISO4762_Hex_Socket_Head_Cap_Screw_M3x16_001_007  label="ISO4762_Hex_Socket_Head_Cap_Screw_M3x16_008"  # a2plus imported part (geometry in sourceFile) (typed FeaturePython)
  Placement = pos=(25.4278,-150.5,7.49959) rot=(0.083358,0.99652,0;0rad)
  a2p_Version = V0.1
  fixedPosition = false
  sourceFile = ./../../../Documents/FreeCadProjects/FreeCAD-library/Mechanical Parts/Fasteners/Bolts & Screws/Metric/ISO4762_Hex_Socket_Head_Cap_Screw_M3x16.fcstd
  subassemblyImport = false
  timeLastImport = 1557779266
  updateColors = true
FEATURE [App::FeaturePython] circularEdge_016  label="circularEdge_016__rollerAssembly2_001"  # a2plus constraint (typed FeaturePython)
  Object1 = b_ISO4762_Hex_Socket_Head_Cap_Screw_M3x16_001_007
  Object2 = b_rollerAssembly2_001_
  ParentTreeObject = -> b_ISO4762_Hex_Socket_Head_Cap_Screw_M3x16_001_007
  SubElement1 = Edge2
  SubElement2 = Edge28
  Type = circularEdge
  directionConstraint = 0
  lockRotation = false
  offset = 0
FEATURE [App::FeaturePython] circularEdge_016_mirror  label="circularEdge_016__ISO4762_Hex_Socket_Head_Cap_Screw_M3x16_008"  # a2plus constraint (typed FeaturePython)
  Object1 = b_ISO4762_Hex_Socket_Head_Cap_Screw_M3x16_001_007
  Object2 = b_rollerAssembly2_001_
  ParentTreeObject = -> b_rollerAssembly2_001_
  SubElement1 = Edge2
  SubElement2 = Edge28
  Type = circularEdge
  directionConstraint = 0
  lockRotation = false
  offset = 0
FEATURE [Part::FeaturePython] b_ISO4032_Hex_Nut_M3_001_  label="ISO4032_Hex_Nut_M3_001"  # a2plus imported part (geometry in sourceFile) (typed FeaturePython)
  Placement = pos=(18.4284,150.2,-5.7) rot=(-0.049309,0.998784,0;3.14159rad)
  a2p_Version = V0.1
  fixedPosition = false
  sourceFile = ./../../../Documents/FreeCadProjects/FreeCAD-library/Mechanical Parts/Fasteners/Nuts/Metric/ISO4032_Hex_Nut_M3.fcstd
  subassemblyImport = false
  timeLastImport = 1557779266
  updateColors = true
FEATURE [Part::FeaturePython] b_ISO4032_Hex_Nut_M3_001_001  label="ISO4032_Hex_Nut_M3_002"  # a2plus imported part (geometry in sourceFile) (typed FeaturePython)
  Placement = pos=(-6.57159,150.2,-5.70064) rot=(0.796448,-0.604707,1e-06;3.14159rad)
  a2p_Version = V0.1
  fixedPosition = false
  sourceFile = ./../../../Documents/FreeCadProjects/FreeCAD-library/Mechanical Parts/Fasteners/Nuts/Metric/ISO4032_Hex_Nut_M3.fcstd
  subassemblyImport = false
  timeLastImport = 1557779266
  updateColors = true
FEATURE [Part::FeaturePython] b_ISO4032_Hex_Nut_M3_001_002  label="ISO4032_Hex_Nut_M3_003"  # a2plus imported part (geometry in sourceFile) (typed FeaturePython)
  Placement = pos=(0.428412,150.2,-5.70063) rot=(-0.645151,0.764055,-1e-06;3.14159rad)
  a2p_Version = V0.1
  fixedPosition = false
  sourceFile = ./../../../Documents/FreeCadProjects/FreeCAD-library/Mechanical Parts/Fasteners/Nuts/Metric/ISO4032_Hex_Nut_M3.fcstd
  subassemblyImport = false
  timeLastImport = 1557779266
  updateColors = true
FEATURE [Part::FeaturePython] b_ISO4032_Hex_Nut_M3_001_003  label="ISO4032_Hex_Nut_M3_004"  # a2plus imported part (geometry in sourceFile) (typed FeaturePython)
  Placement = pos=(-6.57223,-150.5,-5.7006) rot=(0.99614,0.087773,0;3.14159rad)
  a2p_Version = V0.1
  fixedPosition = false
  sourceFile = ./../../../Documents/FreeCadProjects/FreeCAD-library/Mechanical Parts/Fasteners/Nuts/Metric/ISO4032_Hex_Nut_M3.fcstd
  subassemblyImport = false
  timeLastImport = 1557779266
  updateColors = true
FEATURE [Part::FeaturePython] b_ISO4032_Hex_Nut_M3_001_004  label="ISO4032_Hex_Nut_M3_005"  # a2plus imported part (geometry in sourceFile) (typed FeaturePython)
  Placement = pos=(25.4284,150.2,-5.7) rot=(0.857699,0.514152,0;3.14159rad)
  a2p_Version = V0.1
  fixedPosition = false
  sourceFile = ./../../../Documents/FreeCadProjects/FreeCAD-library/Mechanical Parts/Fasteners/Nuts/Metric/ISO4032_Hex_Nut_M3.fcstd
  subassemblyImport = false
  timeLastImport = 1557779266
  updateColors = true
FEATURE [Part::FeaturePython] b_ISO4032_Hex_Nut_M3_001_005  label="ISO4032_Hex_Nut_M3_006"  # a2plus imported part (geometry in sourceFile) (typed FeaturePython)
  Placement = pos=(25.4278,-150.5,-5.70041) rot=(0.972849,0.231441,0;3.14159rad)
  a2p_Version = V0.1
  fixedPosition = false
  sourceFile = ./../../../Documents/FreeCadProjects/FreeCAD-library/Mechanical Parts/Fasteners/Nuts/Metric/ISO4032_Hex_Nut_M3.fcstd
  subassemblyImport = false
  timeLastImport = 1557779266
  updateColors = true
FEATURE [Part::FeaturePython] b_ISO4032_Hex_Nut_M3_001_006  label="ISO4032_Hex_Nut_M3_007"  # a2plus imported part (geometry in sourceFile) (typed FeaturePython)
  Placement = pos=(-2.94877,-164.023,-5.7006) rot=(-0.400603,0.916252,0;3.14159rad)
  a2p_Version = V0.1
  fixedPosition = false
  sourceFile = ./../../../Documents/FreeCadProjects/FreeCAD-library/Mechanical Parts/Fasteners/Nuts/Metric/ISO4032_Hex_Nut_M3.fcstd
  subassemblyImport = false
  timeLastImport = 1557779266
  updateColors = true
FEATURE [Part::FeaturePython] b_ISO4032_Hex_Nut_M3_001_007  label="ISO4032_Hex_Nut_M3_008"  # a2plus imported part (geometry in sourceFile) (typed FeaturePython)
  Placement = pos=(21.9278,-156.562,-6.70041) rot=(0.997343,-0.072847,0;3.14159rad)
  a2p_Version = V0.1
  fixedPosition = false
  sourceFile = ./../../../Documents/FreeCadProjects/FreeCAD-library/Mechanical Parts/Fasteners/Nuts/Metric/ISO4032_Hex_Nut_M3.fcstd
  subassemblyImport = false
  timeLastImport = 1557779266
  updateColors = true
FEATURE [App::FeaturePython] circularEdge_021  label="circularEdge_021__ISO4762_Hex_Socket_Head_Cap_Screw_M3x16_007"  # a2plus constraint (typed FeaturePython)
  Object1 = b_ISO4032_Hex_Nut_M3_001_007
  Object2 = b_ISO4762_Hex_Socket_Head_Cap_Screw_M3x16_001_006
  ParentTreeObject = -> b_ISO4032_Hex_Nut_M3_001_007
  SubElement1 = Edge128
  SubElement2 = Edge6
  Type = circularEdge
  directionConstraint = 0
  lockRotation = false
  offset = 0
FEATURE [App::FeaturePython] circularEdge_021_mirror  label="circularEdge_021__ISO4032_Hex_Nut_M3_008"  # a2plus constraint (typed FeaturePython)
  Object1 = b_ISO4032_Hex_Nut_M3_001_007
  Object2 = b_ISO4762_Hex_Socket_Head_Cap_Screw_M3x16_001_006
  ParentTreeObject = -> b_ISO4762_Hex_Socket_Head_Cap_Screw_M3x16_001_006
  SubElement1 = Edge128
  SubElement2 = Edge6
  Type = circularEdge
  directionConstraint = 0
  lockRotation = false
  offset = 0
FEATURE [App::FeaturePython] circularEdge_022  label="circularEdge_022__ISO4762_Hex_Socket_Head_Cap_Screw_M3x16_008"  # a2plus constraint (typed FeaturePython)
  Object1 = b_ISO4032_Hex_Nut_M3_001_005
  Object2 = b_ISO4762_Hex_Socket_Head_Cap_Screw_M3x16_001_007
  ParentTreeObject = -> b_ISO4032_Hex_Nut_M3_001_005
  SubElement1 = Edge128
  SubElement2 = Edge6
  Type = circularEdge
  directionConstraint = 0
  lockRotation = false
  offset = 0
FEATURE [App::FeaturePython] circularEdge_022_mirror  label="circularEdge_022__ISO4032_Hex_Nut_M3_006"  # a2plus constraint (typed FeaturePython)
  Object1 = b_ISO4032_Hex_Nut_M3_001_005
  Object2 = b_ISO4762_Hex_Socket_Head_Cap_Screw_M3x16_001_007
  ParentTreeObject = -> b_ISO4762_Hex_Socket_Head_Cap_Screw_M3x16_001_007
  SubElement1 = Edge128
  SubElement2 = Edge6
  Type = circularEdge
  directionConstraint = 0
  lockRotation = false
  offset = 0
FEATURE [App::FeaturePython] circularEdge_023  label="circularEdge_023__ISO4762_Hex_Socket_Head_Cap_Screw_M3x16_006"  # a2plus constraint (typed FeaturePython)
  Object1 = b_ISO4032_Hex_Nut_M3_001_006
  Object2 = b_ISO4762_Hex_Socket_Head_Cap_Screw_M3x16_001_005
  ParentTreeObject = -> b_ISO4032_Hex_Nut_M3_001_006
  SubElement1 = Edge128
  SubElement2 = Edge6
  Type = circularEdge
  directionConstraint = 0
  lockRotation = false
  offset = 0
FEATURE [App::FeaturePython] circularEdge_023_mirror  label="circularEdge_023__ISO4032_Hex_Nut_M3_007"  # a2plus constraint (typed FeaturePython)
  Object1 = b_ISO4032_Hex_Nut_M3_001_006
  Object2 = b_ISO4762_Hex_Socket_Head_Cap_Screw_M3x16_001_005
  ParentTreeObject = -> b_ISO4762_Hex_Socket_Head_Cap_Screw_M3x16_001_005
  SubElement1 = Edge128
  SubElement2 = Edge6
  Type = circularEdge
  directionConstraint = 0
  lockRotation = false
  offset = 0
FEATURE [App::FeaturePython] circularEdge_024  label="circularEdge_024__ISO4762_Hex_Socket_Head_Cap_Screw_M3x16_005"  # a2plus constraint (typed FeaturePython)
  Object1 = b_ISO4032_Hex_Nut_M3_001_003
  Object2 = b_ISO4762_Hex_Socket_Head_Cap_Screw_M3x16_001_004
  ParentTreeObject = -> b_ISO4032_Hex_Nut_M3_001_003
  SubElement1 = Edge128
  SubElement2 = Edge6
  Type = circularEdge
  directionConstraint = 0
  lockRotation = false
  offset = 0
FEATURE [App::FeaturePython] circularEdge_024_mirror  label="circularEdge_024__ISO4032_Hex_Nut_M3_004"  # a2plus constraint (typed FeaturePython)
  Object1 = b_ISO4032_Hex_Nut_M3_001_003
  Object2 = b_ISO4762_Hex_Socket_Head_Cap_Screw_M3x16_001_004
  ParentTreeObject = -> b_ISO4762_Hex_Socket_Head_Cap_Screw_M3x16_001_004
  SubElement1 = Edge128
  SubElement2 = Edge6
  Type = circularEdge
  directionConstraint = 0
  lockRotation = false
  offset = 0
FEATURE [App::DocumentObjectGroup] Group011  label="wood_plate_to _ups_radiator"
  Group = -> [b_ISO4762_Hex_Socket_Head_Cap_Screw_M3x16_001_,b_ISO4762_Hex_Socket_Head_Cap_Screw_M3x16_001_001,b_ISO4762_Hex_Socket_Head_Cap_Screw_M3x16_001_002,b_ISO4762_Hex_Socket_Head_Cap_Screw_M3x16_001_003,b_ISO4762_Hex_Socket_Head_Cap_Screw_M3x16_001_004,b_ISO4762_Hex_Socket_Head_Cap_Screw_M3x16_001_005,b_ISO4762_Hex_Socket_Head_Cap_Screw_M3x16_001_006,b_ISO4762_Hex_Socket_Head_Cap_Screw_M3x16_001_007,+8 more]
FEATURE [App::DocumentObjectGroup] Group010  label="Fasteners"
  Group = -> [Group011]
FEATURE [Part::FeaturePython] b_Screw_M4x20_ISO4762_8_8_A2K_001_  label="Screw M4x20 ISO4762 8,8 A2K_001"  # a2plus imported part (geometry in sourceFile) (typed FeaturePython)
  Placement = pos=(-173.053,188,-42.4993) rot=(-0.577349,-0.577352,0.577349;2.09439rad)
  a2p_Version = V0.1
  fixedPosition = false
  sourceFile = ./../../../Documents/FreeCadProjects/FreeCAD-library/Mechanical Parts/Fasteners/Bolts & Screws/Metric/ISO4762 Hexagon socket head cap screws/Screw M4x20 ISO4762 8,8 A2K.FCStd
  subassemblyImport = false
  timeLastImport = 1557779266
  updateColors = true
FEATURE [App::FeaturePython] planeCoincident_043  label="planeCoincident_043__Case_001"  # a2plus constraint (typed FeaturePython)
  Object1 = b_nema23_xy_assembl_001_001
  Object2 = b_Case_001_
  ParentTreeObject = -> b_nema23_xy_assembl_001_001
  SubElement1 = Face1
  SubElement2 = Face16
  Type = plane
  directionConstraint = 1
  offset = -10
FEATURE [App::FeaturePython] planeCoincident_043_mirror  label="planeCoincident_043__nema23_xy_assembl_002"  # a2plus constraint (typed FeaturePython)
  Object1 = b_nema23_xy_assembl_001_001
  Object2 = b_Case_001_
  ParentTreeObject = -> b_Case_001_
  SubElement1 = Face1
  SubElement2 = Face16
  Type = plane
  directionConstraint = 1
  offset = -10
FEATURE [App::FeaturePython] planeCoincident_058  label="planeCoincident_058__PlywoodPlate_001"  # a2plus constraint (typed FeaturePython)
  Object1 = b_nema23_xy_assembl_001_001
  Object2 = b_PlywoodPlate_001_
  ParentTreeObject = -> b_nema23_xy_assembl_001_001
  SubElement1 = Face8
  SubElement2 = Face2
  Type = plane
  directionConstraint = 1
  offset = -25
FEATURE [App::FeaturePython] planeCoincident_058_mirror  label="planeCoincident_058__nema23_xy_assembl_002"  # a2plus constraint (typed FeaturePython)
  Object1 = b_nema23_xy_assembl_001_001
  Object2 = b_PlywoodPlate_001_
  ParentTreeObject = -> b_PlywoodPlate_001_
  SubElement1 = Face8
  SubElement2 = Face2
  Type = plane
  directionConstraint = 1
  offset = -25
FEATURE [Part::FeaturePython] b_Screw_M4x20_ISO4762_8_8_A2K_001_001  label="Screw M4x20 ISO4762 8,8 A2K_002"  # a2plus imported part (geometry in sourceFile) (typed FeaturePython)
  Placement = pos=(-173.053,168,-12.4993) rot=(-0.562976,-0.605075,0.562976;2.05331rad)
  a2p_Version = V0.1
  fixedPosition = false
  sourceFile = ./../../../Documents/FreeCadProjects/FreeCAD-library/Mechanical Parts/Fasteners/Bolts & Screws/Metric/ISO4762 Hexagon socket head cap screws/Screw M4x20 ISO4762 8,8 A2K.FCStd
  subassemblyImport = false
  timeLastImport = 1557779266
  updateColors = true
FEATURE [App::FeaturePython] planeCoincident_059  label="planeCoincident_059__Case_001"  # a2plus constraint (typed FeaturePython)
  Object1 = b_nema23_xy_assembl_001_
  Object2 = b_Case_001_
  ParentTreeObject = -> b_nema23_xy_assembl_001_
  SubElement1 = Face14
  SubElement2 = Face11
  Type = plane
  directionConstraint = 1
  offset = -10
FEATURE [App::FeaturePython] planeCoincident_059_mirror  label="planeCoincident_059__nema23_xy_assembl_001"  # a2plus constraint (typed FeaturePython)
  Object1 = b_nema23_xy_assembl_001_
  Object2 = b_Case_001_
  ParentTreeObject = -> b_Case_001_
  SubElement1 = Face14
  SubElement2 = Face11
  Type = plane
  directionConstraint = 1
  offset = -10
FEATURE [App::FeaturePython] planeCoincident_060  label="planeCoincident_060__PlywoodPlate_001"  # a2plus constraint (typed FeaturePython)
  Object1 = b_cylinder_001_001
  Object2 = b_PlywoodPlate_001_
  ParentTreeObject = -> b_cylinder_001_001
  SubElement1 = Face2
  SubElement2 = Face4
  Type = plane
  directionConstraint = 1
  offset = 0.01
FEATURE [App::FeaturePython] planeCoincident_060_mirror  label="planeCoincident_060__cylinder_2_5.5"  # a2plus constraint (typed FeaturePython)
  Object1 = b_cylinder_001_001
  Object2 = b_PlywoodPlate_001_
  ParentTreeObject = -> b_PlywoodPlate_001_
  SubElement1 = Face2
  SubElement2 = Face4
  Type = plane
  directionConstraint = 1
  offset = 0.01
FEATURE [App::FeaturePython] planeCoincident_061  label="planeCoincident_061__PlywoodPlate_001"  # a2plus constraint (typed FeaturePython)
  Object1 = b_cylinder_001_
  Object2 = b_PlywoodPlate_001_
  ParentTreeObject = -> b_cylinder_001_
  SubElement1 = Face2
  SubElement2 = Face4
  Type = plane
  directionConstraint = 1
  offset = 0.01
FEATURE [App::FeaturePython] planeCoincident_061_mirror  label="planeCoincident_061__cylinder_1_5.5"  # a2plus constraint (typed FeaturePython)
  Object1 = b_cylinder_001_
  Object2 = b_PlywoodPlate_001_
  ParentTreeObject = -> b_PlywoodPlate_001_
  SubElement1 = Face2
  SubElement2 = Face4
  Type = plane
  directionConstraint = 1
  offset = 0.01
FEATURE [App::FeaturePython] axisParallel_007  label="axisParallel_007__Case_001"  # a2plus constraint (typed FeaturePython)
  Object1 = b_bed_001_
  Object2 = b_Case_001_
  ParentTreeObject = -> b_bed_001_
  SubElement1 = Edge11
  SubElement2 = Edge16
  Type = axisParallel
  directionConstraint = 0
FEATURE [App::FeaturePython] axisParallel_007_mirror  label="axisParallel_007__bed_001"  # a2plus constraint (typed FeaturePython)
  Object1 = b_bed_001_
  Object2 = b_Case_001_
  ParentTreeObject = -> b_Case_001_
  SubElement1 = Edge11
  SubElement2 = Edge16
  Type = axisParallel
  directionConstraint = 0
FEATURE [Part::Part2DObjectPython] Line  # Draft 2D object (typed FeaturePython)
  ChamferSize = 0
  Closed = false
  End = (-173.217,209.5,8.99993)
  FilletRadius = 0
  Length = 207.682
  MakeFace = true
  Placement = pos=(-173.217,1.83214,11.4) rot=(0,0,1;0rad)
  Points = (2) [(0,0,0),(3.72865e-06,207.668,-2.40007)]
  Start = (-173.217,1.83214,11.4)
  Subdivisions = 0
FEATURE [Part::Part2DObjectPython] Line001  # Draft 2D object (typed FeaturePython)
  ChamferSize = 0
  Closed = false
  End = (-173.217,-208.5,8.99992)
  FilletRadius = 0
  Length = 210.346
  MakeFace = true
  Placement = pos=(-173.217,1.83214,11.4) rot=(0,0,1;0rad)
  Points = (2) [(0,0,0),(-3.77649e-06,-210.332,-2.40007)]
  Start = (-173.217,1.83214,11.4)
  Subdivisions = 0
FEATURE [App::FeaturePython] Dimension001  # Draft dimension (typed FeaturePython)
  Diameter = false
  Dimline = (-333.5,0.430013,8.99998)
  Direction = (0,0,0)
  Distance = 208.892
  End = (-270.286,0.832095,9.51795)
  Normal = (2.09e-14,-7.23251e-09,1)
  Start = (-270.276,209.723,8.99998)
FEATURE [App::FeaturePython] Dimension002  # Draft dimension (typed FeaturePython)
  Diameter = false
  Dimline = (-157.943,-220.309,8.99998)
  Direction = (0,0,0)
  Distance = 16.1324
  End = (-157,-187.887,8.99998)
  Normal = (2.09e-14,-7.23251e-09,1)
  Start = (-173.132,-187.887,8.99998)
FEATURE [App::FeaturePython] planeCoincident_062  label="planeCoincident_062__PlywoodPlate_002"  # a2plus constraint (typed FeaturePython)
  Object1 = b_cylinder_001_002
  Object2 = b_PlywoodPlate_001_001
  ParentTreeObject = -> b_cylinder_001_002
  SubElement1 = Face2
  SubElement2 = Face5
  Type = plane
  directionConstraint = 0
  offset = 0.1
FEATURE [App::FeaturePython] planeCoincident_062_mirror  label="planeCoincident_062__cylinder_001"  # a2plus constraint (typed FeaturePython)
  Object1 = b_cylinder_001_002
  Object2 = b_PlywoodPlate_001_001
  ParentTreeObject = -> b_PlywoodPlate_001_001
  SubElement1 = Face2
  SubElement2 = Face5
  Type = plane
  directionConstraint = 0
  offset = 0.1
FEATURE [Part::Part2DObjectPython] Line003  # Draft 2D object (typed FeaturePython)
  ChamferSize = 0
  Closed = false
  End = (169.783,208.5,9)
  FilletRadius = 0
  Length = 207.68
  MakeFace = true
  Placement = pos=(169.783,0.819679,9.09914) rot=(0,0,1;0rad)
  Points = (2) [(0,0,0),(-1.15952e-09,207.68,-0.0991452)]
  Start = (169.783,0.819679,9.09914)
  Subdivisions = 0
FEATURE [Part::Part2DObjectPython] Line004  # Draft 2D object (typed FeaturePython)
  ChamferSize = 0
  Closed = false
  End = (297,0.819679,9)
  FilletRadius = 0
  Length = 127.217
  MakeFace = true
  Placement = pos=(169.783,0.819679,9.09914) rot=(0,0,1;0rad)
  Points = (2) [(0,0,0),(127.217,-1.20193e-09,-0.0991442)]
  Start = (169.783,0.819679,9.09914)
  Subdivisions = 0
FEATURE [App::FeaturePython] Dimension003  # Draft dimension (typed FeaturePython)
  Diameter = false
  Dimline = (167.814,228.889,8.99998)
  Direction = (0,0,0)
  Distance = 13.1407
  End = (157,174.322,9)
  Normal = (2.09e-14,-7.23251e-09,1)
  Start = (170.141,174.322,8.99998)
FEATURE [App::FeaturePython] Dimension004  # Draft dimension (typed FeaturePython)
  Diameter = false
  Dimline = (337.35,200.846,8.99998)
  Direction = (0,0,0)
  Distance = 206.046
  End = (280.528,208.5,9)
  Normal = (2.09e-14,-7.23251e-09,1)
  Start = (280.528,2.45401,8.99998)
FEATURE [App::FeaturePython] Dimension005  # Draft dimension (typed FeaturePython)
  Diameter = false
  Dimline = (337.164,-182.266,8.99998)
  Direction = (0,0,0)
  Distance = 211.047
  End = (277.562,-209.5,9)
  Normal = (2.09e-14,-7.23251e-09,1)
  Start = (277.562,1.54684,8.99998)
FEATURE [Part::Part2DObjectPython] Line005  # Draft 2D object (typed FeaturePython)
  ChamferSize = 0
  Closed = false
  End = (-297,0.409182,9)
  FilletRadius = 0
  Length = 123.806
  MakeFace = true
  Placement = pos=(-173.217,0.40918,11.4) rot=(0,0,1;0rad)
  Points = (2) [(0,0,0),(-123.783,2.20936e-06,-2.4)]
  Start = (-173.217,0.40918,11.4)
  Subdivisions = 0
FEATURE [App::FeaturePython] Dimension  # Draft dimension (typed FeaturePython)
  Diameter = false
  Dimline = (-333.419,-1.14461,8.99998)
  Direction = (0,0,0)
  Distance = 209.253
  End = (-276.72,0.409182,9.39321)
  Normal = (2.09e-14,-7.23251e-09,1)
  Start = (-276.712,-208.844,8.99998)
FEATURE [App::FeaturePython] circularEdge_006  label="circularEdge_006__UPS_radiator_002"  # a2plus constraint (typed FeaturePython)
  Object1 = b_rollerAssembly2_001_001
  Object2 = b_UPS_radiator_001_001
  ParentTreeObject = -> b_rollerAssembly2_001_001
  SubElement1 = Edge8
  SubElement2 = Edge82
  Type = circularEdge
  directionConstraint = 1
  lockRotation = false
  offset = 0
FEATURE [App::FeaturePython] circularEdge_006_mirror  label="circularEdge_006__rollerAssembly2_002"  # a2plus constraint (typed FeaturePython)
  Object1 = b_rollerAssembly2_001_001
  Object2 = b_UPS_radiator_001_001
  ParentTreeObject = -> b_UPS_radiator_001_001
  SubElement1 = Edge8
  SubElement2 = Edge82
  Type = circularEdge
  directionConstraint = 1
  lockRotation = false
  offset = 0
FEATURE [App::FeaturePython] circularEdge_007  label="circularEdge_007__UPS_radiator_002"  # a2plus constraint (typed FeaturePython)
  Object1 = b_rollerAssembly1_001_
  Object2 = b_UPS_radiator_001_001
  ParentTreeObject = -> b_rollerAssembly1_001_
  SubElement1 = Edge8
  SubElement2 = Edge84
  Type = circularEdge
  directionConstraint = 0
  lockRotation = false
  offset = 0
FEATURE [App::FeaturePython] circularEdge_007_mirror  label="circularEdge_007__rollerAssembly1_001"  # a2plus constraint (typed FeaturePython)
  Object1 = b_rollerAssembly1_001_
  Object2 = b_UPS_radiator_001_001
  ParentTreeObject = -> b_UPS_radiator_001_001
  SubElement1 = Edge8
  SubElement2 = Edge84
  Type = circularEdge
  directionConstraint = 0
  lockRotation = false
  offset = 0
FEATURE [App::FeaturePython] circularEdge_008  label="circularEdge_008__rollerAssembly1_001"  # a2plus constraint (typed FeaturePython)
  Object1 = b_ISO4762_Hex_Socket_Head_Cap_Screw_M3x16_001_001
  Object2 = b_rollerAssembly1_001_
  ParentTreeObject = -> b_ISO4762_Hex_Socket_Head_Cap_Screw_M3x16_001_001
  SubElement1 = Edge2
  SubElement2 = Edge28
  Type = circularEdge
  directionConstraint = 1
  lockRotation = false
  offset = 0
FEATURE [App::FeaturePython] circularEdge_008_mirror  label="circularEdge_008__ISO4762_Hex_Socket_Head_Cap_Screw_M3x16_002"  # a2plus constraint (typed FeaturePython)
  Object1 = b_ISO4762_Hex_Socket_Head_Cap_Screw_M3x16_001_001
  Object2 = b_rollerAssembly1_001_
  ParentTreeObject = -> b_rollerAssembly1_001_
  SubElement1 = Edge2
  SubElement2 = Edge28
  Type = circularEdge
  directionConstraint = 1
  lockRotation = false
  offset = 0
FEATURE [App::FeaturePython] circularEdge_009  label="circularEdge_009__rollerAssembly1_001"  # a2plus constraint (typed FeaturePython)
  Object1 = b_ISO4762_Hex_Socket_Head_Cap_Screw_M3x16_001_002
  Object2 = b_rollerAssembly1_001_
  ParentTreeObject = -> b_ISO4762_Hex_Socket_Head_Cap_Screw_M3x16_001_002
  SubElement1 = Edge2
  SubElement2 = Edge26
  Type = circularEdge
  directionConstraint = 1
  lockRotation = false
  offset = 0
FEATURE [App::FeaturePython] circularEdge_009_mirror  label="circularEdge_009__ISO4762_Hex_Socket_Head_Cap_Screw_M3x16_003"  # a2plus constraint (typed FeaturePython)
  Object1 = b_ISO4762_Hex_Socket_Head_Cap_Screw_M3x16_001_002
  Object2 = b_rollerAssembly1_001_
  ParentTreeObject = -> b_rollerAssembly1_001_
  SubElement1 = Edge2
  SubElement2 = Edge26
  Type = circularEdge
  directionConstraint = 1
  lockRotation = false
  offset = 0
FEATURE [App::FeaturePython] circularEdge_010  label="circularEdge_010__rollerAssembly2_002"  # a2plus constraint (typed FeaturePython)
  Object1 = b_ISO4762_Hex_Socket_Head_Cap_Screw_M3x16_001_003
  Object2 = b_rollerAssembly2_001_001
  ParentTreeObject = -> b_ISO4762_Hex_Socket_Head_Cap_Screw_M3x16_001_003
  SubElement1 = Edge2
  SubElement2 = Edge28
  Type = circularEdge
  directionConstraint = 0
  lockRotation = false
  offset = 0
FEATURE [App::FeaturePython] circularEdge_010_mirror  label="circularEdge_010__ISO4762_Hex_Socket_Head_Cap_Screw_M3x16_004"  # a2plus constraint (typed FeaturePython)
  Object1 = b_ISO4762_Hex_Socket_Head_Cap_Screw_M3x16_001_003
  Object2 = b_rollerAssembly2_001_001
  ParentTreeObject = -> b_rollerAssembly2_001_001
  SubElement1 = Edge2
  SubElement2 = Edge28
  Type = circularEdge
  directionConstraint = 0
  lockRotation = false
  offset = 0
FEATURE [App::FeaturePython] circularEdge_011  label="circularEdge_011__rollerAssembly2_002"  # a2plus constraint (typed FeaturePython)
  Object1 = b_ISO4762_Hex_Socket_Head_Cap_Screw_M3x16_001_
  Object2 = b_rollerAssembly2_001_001
  ParentTreeObject = -> b_ISO4762_Hex_Socket_Head_Cap_Screw_M3x16_001_
  SubElement1 = Edge2
  SubElement2 = Edge26
  Type = circularEdge
  directionConstraint = 0
  lockRotation = false
  offset = 0
FEATURE [App::FeaturePython] circularEdge_011_mirror  label="circularEdge_011__ISO4762_Hex_Socket_Head_Cap_Screw_M3x16_001"  # a2plus constraint (typed FeaturePython)
  Object1 = b_ISO4762_Hex_Socket_Head_Cap_Screw_M3x16_001_
  Object2 = b_rollerAssembly2_001_001
  ParentTreeObject = -> b_rollerAssembly2_001_001
  SubElement1 = Edge2
  SubElement2 = Edge26
  Type = circularEdge
  directionConstraint = 0
  lockRotation = false
  offset = 0
FEATURE [App::FeaturePython] circularEdge_012  label="circularEdge_012__UPS_radiator_001"  # a2plus constraint (typed FeaturePython)
  Object1 = b_rollerAssembly1_001_001
  Object2 = b_UPS_radiator_001_
  ParentTreeObject = -> b_rollerAssembly1_001_001
  SubElement1 = Edge8
  SubElement2 = Edge84
  Type = circularEdge
  directionConstraint = 0
  lockRotation = false
  offset = 0
FEATURE [App::FeaturePython] circularEdge_012_mirror  label="circularEdge_012__rollerAssembly1_002"  # a2plus constraint (typed FeaturePython)
  Object1 = b_rollerAssembly1_001_001
  Object2 = b_UPS_radiator_001_
  ParentTreeObject = -> b_UPS_radiator_001_
  SubElement1 = Edge8
  SubElement2 = Edge84
  Type = circularEdge
  directionConstraint = 0
  lockRotation = false
  offset = 0
FEATURE [App::FeaturePython] circularEdge_013  label="circularEdge_013__rollerAssembly1_002"  # a2plus constraint (typed FeaturePython)
  Object1 = b_ISO4762_Hex_Socket_Head_Cap_Screw_M3x16_001_004
  Object2 = b_rollerAssembly1_001_001
  ParentTreeObject = -> b_ISO4762_Hex_Socket_Head_Cap_Screw_M3x16_001_004
  SubElement1 = Edge2
  SubElement2 = Edge28
  Type = circularEdge
  directionConstraint = 1
  lockRotation = false
  offset = 0
FEATURE [App::FeaturePython] circularEdge_013_mirror  label="circularEdge_013__ISO4762_Hex_Socket_Head_Cap_Screw_M3x16_005"  # a2plus constraint (typed FeaturePython)
  Object1 = b_ISO4762_Hex_Socket_Head_Cap_Screw_M3x16_001_004
  Object2 = b_rollerAssembly1_001_001
  ParentTreeObject = -> b_rollerAssembly1_001_001
  SubElement1 = Edge2
  SubElement2 = Edge28
  Type = circularEdge
  directionConstraint = 1
  lockRotation = false
  offset = 0
FEATURE [App::FeaturePython] circularEdge_005  label="circularEdge_005__UPS_radiator_001"  # a2plus constraint (typed FeaturePython)
  Object1 = b_rollerAssembly2_001_
  Object2 = b_UPS_radiator_001_
  ParentTreeObject = -> b_rollerAssembly2_001_
  SubElement1 = Edge8
  SubElement2 = Edge82
  Type = circularEdge
  directionConstraint = 1
  lockRotation = false
  offset = 0
FEATURE [App::FeaturePython] circularEdge_005_mirror  label="circularEdge_005__rollerAssembly2_001"  # a2plus constraint (typed FeaturePython)
  Object1 = b_rollerAssembly2_001_
  Object2 = b_UPS_radiator_001_
  ParentTreeObject = -> b_UPS_radiator_001_
  SubElement1 = Edge8
  SubElement2 = Edge82
  Type = circularEdge
  directionConstraint = 1
  lockRotation = false
  offset = 0
FEATURE [Part::Part2DObjectPython] Line006  # Draft 2D object (typed FeaturePython)
  ChamferSize = 0
  Closed = false
  End = (-9.88902,-139.306,14.9994)
  FilletRadius = 0
  Length = 281.893
  MakeFace = true
  Placement = pos=(-12.3666,142.575,14.9992) rot=(0.462789,-0.731091,-0.501332;0.303465rad)
  Points = (2) [(0,0,0),(48.9758,-275.553,33.6946)]
  Start = (-12.3666,142.575,14.9992)
  Subdivisions = 0
FEATURE [Part::Part2DObjectPython] Line007  # Draft 2D object (typed FeaturePython)
  ChamferSize = 0
  Closed = false
  End = (31.2221,-142.876,14.9996)
  FilletRadius = 0
  Length = 285.452
  MakeFace = true
  Placement = pos=(31.2216,142.576,15) rot=(0.462789,-0.731091,-0.501332;0.303465rad)
  Points = (2) [(0,0,0),(47.1777,-279.38,34.6953)]
  Start = (31.2216,142.576,15)
  Subdivisions = 0
FEATURE [App::FeaturePython] planeCoincident_001  label="planeCoincident_001__Case_001"  # a2plus constraint (typed FeaturePython)
  Object1 = b_corner_steel_8_001_001
  Object2 = b_Case_001_
  ParentTreeObject = -> b_corner_steel_8_001_001
  SubElement1 = Face2
  SubElement2 = Face11
  Type = plane
  directionConstraint = 1
  offset = 0
FEATURE [App::FeaturePython] planeCoincident_001_mirror  label="planeCoincident_001__corner_steel_8_002"  # a2plus constraint (typed FeaturePython)
  Object1 = b_corner_steel_8_001_001
  Object2 = b_Case_001_
  ParentTreeObject = -> b_Case_001_
  SubElement1 = Face2
  SubElement2 = Face11
  Type = plane
  directionConstraint = 1
  offset = 0
FEATURE [App::FeaturePython] circularEdge_001  label="circularEdge_001__cylinder2_7.5_001"  # a2plus constraint (typed FeaturePython)
  Object1 = b_corner_steel_8_001_001
  Object2 = b_cylinder2_7_5_001_
  ParentTreeObject = -> b_corner_steel_8_001_001
  SubElement1 = Edge7
  SubElement2 = Edge3
  Type = circularEdge
  directionConstraint = 0
  lockRotation = false
  offset = 8
FEATURE [App::FeaturePython] circularEdge_001_mirror  label="circularEdge_001__corner_steel_8_002"  # a2plus constraint (typed FeaturePython)
  Object1 = b_corner_steel_8_001_001
  Object2 = b_cylinder2_7_5_001_
  ParentTreeObject = -> b_cylinder2_7_5_001_
  SubElement1 = Edge7
  SubElement2 = Edge3
  Type = circularEdge
  directionConstraint = 0
  lockRotation = false
  offset = 8
FEATURE [App::FeaturePython] axisParallel_001  label="axisParallel_001__Case_001"  # a2plus constraint (typed FeaturePython)
  Object1 = b_corner_steel_8_001_001
  Object2 = b_Case_001_
  ParentTreeObject = -> b_corner_steel_8_001_001
  SubElement1 = Edge23
  SubElement2 = Edge16
  Type = axisParallel
  directionConstraint = 1
FEATURE [App::FeaturePython] axisParallel_001_mirror  label="axisParallel_001__corner_steel_8_002"  # a2plus constraint (typed FeaturePython)
  Object1 = b_corner_steel_8_001_001
  Object2 = b_Case_001_
  ParentTreeObject = -> b_Case_001_
  SubElement1 = Edge23
  SubElement2 = Edge16
  Type = axisParallel
  directionConstraint = 1
FEATURE [App::FeaturePython] planeCoincident_013  label="planeCoincident_013__corner_steel_8_002"  # a2plus constraint (typed FeaturePython)
  Object1 = b_sqware_pad__8_001_001
  Object2 = b_corner_steel_8_001_001
  ParentTreeObject = -> b_sqware_pad__8_001_001
  SubElement1 = Face5
  SubElement2 = Face1
  Type = plane
  directionConstraint = 1
  offset = 0
FEATURE [App::FeaturePython] planeCoincident_013_mirror  label="planeCoincident_013__sqware_pad__8_002"  # a2plus constraint (typed FeaturePython)
  Object1 = b_sqware_pad__8_001_001
  Object2 = b_corner_steel_8_001_001
  ParentTreeObject = -> b_corner_steel_8_001_001
  SubElement1 = Face5
  SubElement2 = Face1
  Type = plane
  directionConstraint = 1
  offset = 0
FEATURE [App::FeaturePython] planesParallel_006  label="planesParallel_006__corner_steel_8_002"  # a2plus constraint (typed FeaturePython)
  Object1 = b_sqware_pad__8_001_001
  Object2 = b_corner_steel_8_001_001
  ParentTreeObject = -> b_sqware_pad__8_001_001
  SubElement1 = Face1
  SubElement2 = Face4
  Type = planesParallel
  directionConstraint = 1
FEATURE [App::FeaturePython] planesParallel_006_mirror  label="planesParallel_006__sqware_pad__8_002"  # a2plus constraint (typed FeaturePython)
  Object1 = b_sqware_pad__8_001_001
  Object2 = b_corner_steel_8_001_001
  ParentTreeObject = -> b_corner_steel_8_001_001
  SubElement1 = Face1
  SubElement2 = Face4
  Type = planesParallel
  directionConstraint = 1
FEATURE [App::FeaturePython] axisCoincident_022  label="axisCoincident_022__cylinder2_7.5_001"  # a2plus constraint (typed FeaturePython)
  Object1 = b_sqware_pad__8_001_001
  Object2 = b_cylinder2_7_5_001_
  ParentTreeObject = -> b_sqware_pad__8_001_001
  SubElement1 = Face11
  SubElement2 = Face1
  Type = axial
  directionConstraint = 0
  lockRotation = false
FEATURE [App::FeaturePython] axisCoincident_022_mirror  label="axisCoincident_022__sqware_pad__8_002"  # a2plus constraint (typed FeaturePython)
  Object1 = b_sqware_pad__8_001_001
  Object2 = b_cylinder2_7_5_001_
  ParentTreeObject = -> b_cylinder2_7_5_001_
  SubElement1 = Face11
  SubElement2 = Face1
  Type = axial
  directionConstraint = 0
  lockRotation = false
FEATURE [App::DocumentObjectGroup] Group012  label="Dimensions&Lines"
  Group = -> [Line,Line001,Dimension001,Dimension002,Line003,Line004,Dimension003,Dimension004,Dimension005,Line005,Dimension,Line006,Line007]
FEATURE [App::FeaturePython] planeCoincident_009  label="planeCoincident_009__Case_001"  # a2plus constraint (typed FeaturePython)
  Object1 = b_corner_steel_12_001_
  Object2 = b_Case_001_
  ParentTreeObject = -> b_corner_steel_12_001_
  SubElement1 = Face2
  SubElement2 = Face16
  Type = plane
  directionConstraint = 1
  offset = 0
FEATURE [App::FeaturePython] planeCoincident_009_mirror  label="planeCoincident_009__corner_steel_12_001"  # a2plus constraint (typed FeaturePython)
  Object1 = b_corner_steel_12_001_
  Object2 = b_Case_001_
  ParentTreeObject = -> b_Case_001_
  SubElement1 = Face2
  SubElement2 = Face16
  Type = plane
  directionConstraint = 1
  offset = 0
FEATURE [App::FeaturePython] circularEdge_003  label="circularEdge_003__cylinder1_11.5_001"  # a2plus constraint (typed FeaturePython)
  Object1 = b_corner_steel_12_001_
  Object2 = b_cylinder1_11_5_001_
  ParentTreeObject = -> b_corner_steel_12_001_
  SubElement1 = Edge7
  SubElement2 = Edge9
  Type = circularEdge
  directionConstraint = 0
  lockRotation = false
  offset = 8
FEATURE [App::FeaturePython] circularEdge_003_mirror  label="circularEdge_003__corner_steel_12_001"  # a2plus constraint (typed FeaturePython)
  Object1 = b_corner_steel_12_001_
  Object2 = b_cylinder1_11_5_001_
  ParentTreeObject = -> b_cylinder1_11_5_001_
  SubElement1 = Edge7
  SubElement2 = Edge9
  Type = circularEdge
  directionConstraint = 0
  lockRotation = false
  offset = 8
FEATURE [App::FeaturePython] planesParallel_004  label="planesParallel_004__Case_001"  # a2plus constraint (typed FeaturePython)
  Object1 = b_corner_steel_12_001_
  Object2 = b_Case_001_
  ParentTreeObject = -> b_corner_steel_12_001_
  SubElement1 = Face3
  SubElement2 = Face4
  Type = planesParallel
  directionConstraint = 0
FEATURE [App::FeaturePython] planesParallel_004_mirror  label="planesParallel_004__corner_steel_12_001"  # a2plus constraint (typed FeaturePython)
  Object1 = b_corner_steel_12_001_
  Object2 = b_Case_001_
  ParentTreeObject = -> b_Case_001_
  SubElement1 = Face3
  SubElement2 = Face4
  Type = planesParallel
  directionConstraint = 0
FEATURE [App::FeaturePython] planeCoincident_049  label="planeCoincident_049__corner_steel_12_001"  # a2plus constraint (typed FeaturePython)
  Object1 = b_sqware_pad_001_
  Object2 = b_corner_steel_12_001_
  ParentTreeObject = -> b_sqware_pad_001_
  SubElement1 = Face5
  SubElement2 = Face1
  Type = plane
  directionConstraint = 1
  offset = 0
FEATURE [App::FeaturePython] planeCoincident_049_mirror  label="planeCoincident_049__sqware_pad_001"  # a2plus constraint (typed FeaturePython)
  Object1 = b_sqware_pad_001_
  Object2 = b_corner_steel_12_001_
  ParentTreeObject = -> b_corner_steel_12_001_
  SubElement1 = Face5
  SubElement2 = Face1
  Type = plane
  directionConstraint = 1
  offset = 0
FEATURE [App::FeaturePython] axisCoincident_023  label="axisCoincident_023__cylinder1_11.5_001"  # a2plus constraint (typed FeaturePython)
  Object1 = b_sqware_pad_001_
  Object2 = b_cylinder1_11_5_001_
  ParentTreeObject = -> b_sqware_pad_001_
  SubElement1 = Face11
  SubElement2 = Face1
  Type = axial
  directionConstraint = 0
  lockRotation = false
FEATURE [App::FeaturePython] axisCoincident_023_mirror  label="axisCoincident_023__sqware_pad_001"  # a2plus constraint (typed FeaturePython)
  Object1 = b_sqware_pad_001_
  Object2 = b_cylinder1_11_5_001_
  ParentTreeObject = -> b_cylinder1_11_5_001_
  SubElement1 = Face11
  SubElement2 = Face1
  Type = axial
  directionConstraint = 0
  lockRotation = false
FEATURE [App::FeaturePython] planesParallel_009  label="planesParallel_009__corner_steel_12_001"  # a2plus constraint (typed FeaturePython)
  Object1 = b_sqware_pad_001_
  Object2 = b_corner_steel_12_001_
  ParentTreeObject = -> b_sqware_pad_001_
  SubElement1 = Face1
  SubElement2 = Face3
  Type = planesParallel
  directionConstraint = 1
FEATURE [App::FeaturePython] planesParallel_009_mirror  label="planesParallel_009__sqware_pad_001"  # a2plus constraint (typed FeaturePython)
  Object1 = b_sqware_pad_001_
  Object2 = b_corner_steel_12_001_
  ParentTreeObject = -> b_corner_steel_12_001_
  SubElement1 = Face1
  SubElement2 = Face3
  Type = planesParallel
  directionConstraint = 1
FEATURE [App::FeaturePython] circularEdge_017  label="circularEdge_017__sqware_pad_001"  # a2plus constraint (typed FeaturePython)
  Object1 = b_Screw_M4x20_ISO4762_8_8_A2K_001_001
  Object2 = b_sqware_pad_001_
  ParentTreeObject = -> b_Screw_M4x20_ISO4762_8_8_A2K_001_001
  SubElement1 = Edge2
  SubElement2 = Edge13
  Type = circularEdge
  directionConstraint = 1
  lockRotation = false
  offset = 0
FEATURE [App::FeaturePython] circularEdge_017_mirror  label="circularEdge_017__Screw M4x20 ISO4762 8,8 A2K_002"  # a2plus constraint (typed FeaturePython)
  Object1 = b_Screw_M4x20_ISO4762_8_8_A2K_001_001
  Object2 = b_sqware_pad_001_
  ParentTreeObject = -> b_sqware_pad_001_
  SubElement1 = Edge2
  SubElement2 = Edge13
  Type = circularEdge
  directionConstraint = 1
  lockRotation = false
  offset = 0
FEATURE [App::FeaturePython] circularEdge_018  label="circularEdge_018__sqware_pad_001"  # a2plus constraint (typed FeaturePython)
  Object1 = b_Screw_M4x20_ISO4762_8_8_A2K_001_
  Object2 = b_sqware_pad_001_
  ParentTreeObject = -> b_Screw_M4x20_ISO4762_8_8_A2K_001_
  SubElement1 = Edge32
  SubElement2 = Edge14
  Type = circularEdge
  directionConstraint = 1
  lockRotation = false
  offset = 0
FEATURE [App::FeaturePython] circularEdge_018_mirror  label="circularEdge_018__Screw M4x20 ISO4762 8,8 A2K_001"  # a2plus constraint (typed FeaturePython)
  Object1 = b_Screw_M4x20_ISO4762_8_8_A2K_001_
  Object2 = b_sqware_pad_001_
  ParentTreeObject = -> b_sqware_pad_001_
  SubElement1 = Edge32
  SubElement2 = Edge14
  Type = circularEdge
  directionConstraint = 1
  lockRotation = false
  offset = 0
FEATURE [App::FeaturePython] planeCoincident_050  label="planeCoincident_050__corner_steel_12_001"  # a2plus constraint (typed FeaturePython)
  Object1 = b_corner_steel_8_001_001
  Object2 = b_corner_steel_12_001_
  ParentTreeObject = -> b_corner_steel_8_001_001
  SubElement1 = Face16
  SubElement2 = Face16
  Type = plane
  directionConstraint = 0
  offset = 0
FEATURE [App::FeaturePython] planeCoincident_050_mirror  label="planeCoincident_050__corner_steel_8_002"  # a2plus constraint (typed FeaturePython)
  Object1 = b_corner_steel_8_001_001
  Object2 = b_corner_steel_12_001_
  ParentTreeObject = -> b_corner_steel_12_001_
  SubElement1 = Face16
  SubElement2 = Face16
  Type = plane
  directionConstraint = 0
  offset = 0
FEATURE [App::FeaturePython] planesParallel_010  label="planesParallel_010__corner_steel_12_002"  # a2plus constraint (typed FeaturePython)
  Object1 = b_sqware_pad_001_001
  Object2 = b_corner_steel_12_001_001
  ParentTreeObject = -> b_sqware_pad_001_001
  SubElement1 = Face6
  SubElement2 = Face3
  Type = planesParallel
  directionConstraint = 1
FEATURE [App::FeaturePython] planesParallel_010_mirror  label="planesParallel_010__sqware_pad_002"  # a2plus constraint (typed FeaturePython)
  Object1 = b_sqware_pad_001_001
  Object2 = b_corner_steel_12_001_001
  ParentTreeObject = -> b_corner_steel_12_001_001
  SubElement1 = Face6
  SubElement2 = Face3
  Type = planesParallel
  directionConstraint = 1
FEATURE [App::FeaturePython] planeCoincident_051  label="planeCoincident_051__corner_steel_12_002"  # a2plus constraint (typed FeaturePython)
  Object1 = b_sqware_pad_001_001
  Object2 = b_corner_steel_12_001_001
  ParentTreeObject = -> b_sqware_pad_001_001
  SubElement1 = Face5
  SubElement2 = Face1
  Type = plane
  directionConstraint = 1
  offset = 0
FEATURE [App::FeaturePython] planeCoincident_051_mirror  label="planeCoincident_051__sqware_pad_002"  # a2plus constraint (typed FeaturePython)
  Object1 = b_sqware_pad_001_001
  Object2 = b_corner_steel_12_001_001
  ParentTreeObject = -> b_corner_steel_12_001_001
  SubElement1 = Face5
  SubElement2 = Face1
  Type = plane
  directionConstraint = 1
  offset = 0
FEATURE [App::FeaturePython] axisCoincident_024  label="axisCoincident_024__cylinder1_11.5_001"  # a2plus constraint (typed FeaturePython)
  Object1 = b_sqware_pad_001_001
  Object2 = b_cylinder1_11_5_001_
  ParentTreeObject = -> b_sqware_pad_001_001
  SubElement1 = Face11
  SubElement2 = Face1
  Type = axial
  directionConstraint = 0
  lockRotation = false
FEATURE [App::FeaturePython] axisCoincident_024_mirror  label="axisCoincident_024__sqware_pad_002"  # a2plus constraint (typed FeaturePython)
  Object1 = b_sqware_pad_001_001
  Object2 = b_cylinder1_11_5_001_
  ParentTreeObject = -> b_cylinder1_11_5_001_
  SubElement1 = Face11
  SubElement2 = Face1
  Type = axial
  directionConstraint = 0
  lockRotation = false
FEATURE [App::FeaturePython] planesParallel_011  label="planesParallel_011__corner_steel_8_001"  # a2plus constraint (typed FeaturePython)
  Object1 = b_sqware_pad__8_001_
  Object2 = b_corner_steel_8_001_
  ParentTreeObject = -> b_sqware_pad__8_001_
  SubElement1 = Face6
  SubElement2 = Face4
  Type = planesParallel
  directionConstraint = 0
FEATURE [App::FeaturePython] planesParallel_011_mirror  label="planesParallel_011__sqware_pad__8_001"  # a2plus constraint (typed FeaturePython)
  Object1 = b_sqware_pad__8_001_
  Object2 = b_corner_steel_8_001_
  ParentTreeObject = -> b_corner_steel_8_001_
  SubElement1 = Face6
  SubElement2 = Face4
  Type = planesParallel
  directionConstraint = 0
FEATURE [App::FeaturePython] planeCoincident_047  label="planeCoincident_047__corner_steel_8_001"  # a2plus constraint (typed FeaturePython)
  Object1 = b_sqware_pad__8_001_
  Object2 = b_corner_steel_8_001_
  ParentTreeObject = -> b_sqware_pad__8_001_
  SubElement1 = Face5
  SubElement2 = Face1
  Type = plane
  directionConstraint = 1
  offset = 0
FEATURE [App::FeaturePython] planeCoincident_047_mirror  label="planeCoincident_047__sqware_pad__8_001"  # a2plus constraint (typed FeaturePython)
  Object1 = b_sqware_pad__8_001_
  Object2 = b_corner_steel_8_001_
  ParentTreeObject = -> b_corner_steel_8_001_
  SubElement1 = Face5
  SubElement2 = Face1
  Type = plane
  directionConstraint = 1
  offset = 0
FEATURE [App::FeaturePython] axisCoincident_025  label="axisCoincident_025__sqware_pad__8_001"  # a2plus constraint (typed FeaturePython)
  Object1 = b_cylinder2_7_5_001_
  Object2 = b_sqware_pad__8_001_
  ParentTreeObject = -> b_cylinder2_7_5_001_
  SubElement1 = Face1
  SubElement2 = Face11
  Type = axial
  directionConstraint = 0
  lockRotation = false
FEATURE [App::FeaturePython] axisCoincident_025_mirror  label="axisCoincident_025__cylinder2_7.5_001"  # a2plus constraint (typed FeaturePython)
  Object1 = b_cylinder2_7_5_001_
  Object2 = b_sqware_pad__8_001_
  ParentTreeObject = -> b_sqware_pad__8_001_
  SubElement1 = Face1
  SubElement2 = Face11
  Type = axial
  directionConstraint = 0
  lockRotation = false
FEATURE [Part::FeaturePython] b_Screw_M4x20_ISO4762_8_8_A2K_001_003  label="Screw M4x20 ISO4762 8,8 A2K_004"  # a2plus imported part (geometry in sourceFile) (typed FeaturePython)
  Placement = pos=(-156.353,188.9,-12.4993) rot=(-0.025477,0.706877,-0.706877;3.19254rad)
  a2p_Version = V0.1
  fixedPosition = false
  sourceFile = ./../../../Documents/FreeCadProjects/FreeCAD-library/Mechanical Parts/Fasteners/Bolts & Screws/Metric/ISO4762 Hexagon socket head cap screws/Screw M4x20 ISO4762 8,8 A2K.FCStd
  subassemblyImport = false
  timeLastImport = 1557779266
  updateColors = true
FEATURE [App::FeaturePython] circularEdge_019  label="circularEdge_019__corner_steel_12_001"  # a2plus constraint (typed FeaturePython)
  Object1 = b_Screw_M4x20_ISO4762_8_8_A2K_001_003
  Object2 = b_corner_steel_12_001_
  ParentTreeObject = -> b_Screw_M4x20_ISO4762_8_8_A2K_001_003
  SubElement1 = Edge1
  SubElement2 = Edge39
  Type = circularEdge
  directionConstraint = 0
  lockRotation = false
  offset = 8.5
FEATURE [App::FeaturePython] circularEdge_019_mirror  label="circularEdge_019__Screw M4x20 ISO4762 8,8 A2K_004"  # a2plus constraint (typed FeaturePython)
  Object1 = b_Screw_M4x20_ISO4762_8_8_A2K_001_003
  Object2 = b_corner_steel_12_001_
  ParentTreeObject = -> b_corner_steel_12_001_
  SubElement1 = Edge1
  SubElement2 = Edge39
  Type = circularEdge
  directionConstraint = 0
  lockRotation = false
  offset = 8.5
FEATURE [Part::FeaturePython] b_Screw_M4x20_ISO4762_8_8_A2K_001_004  label="Screw M4x20 ISO4762 8,8 A2K_005"  # a2plus imported part (geometry in sourceFile) (typed FeaturePython)
  Placement = pos=(-136.853,188.9,-42.4993) rot=(-0.025477,0.706877,-0.706877;3.19254rad)
  a2p_Version = V0.1
  fixedPosition = false
  sourceFile = ./../../../Documents/FreeCadProjects/FreeCAD-library/Mechanical Parts/Fasteners/Bolts & Screws/Metric/ISO4762 Hexagon socket head cap screws/Screw M4x20 ISO4762 8,8 A2K.FCStd
  subassemblyImport = false
  timeLastImport = 1557779266
  updateColors = true
FEATURE [App::FeaturePython] circularEdge_020  label="circularEdge_020__corner_steel_12_001"  # a2plus constraint (typed FeaturePython)
  Object1 = b_Screw_M4x20_ISO4762_8_8_A2K_001_004
  Object2 = b_corner_steel_12_001_
  ParentTreeObject = -> b_Screw_M4x20_ISO4762_8_8_A2K_001_004
  SubElement1 = Edge31
  SubElement2 = Edge43
  Type = circularEdge
  directionConstraint = 0
  lockRotation = false
  offset = 8.5
FEATURE [App::FeaturePython] circularEdge_020_mirror  label="circularEdge_020__Screw M4x20 ISO4762 8,8 A2K_005"  # a2plus constraint (typed FeaturePython)
  Object1 = b_Screw_M4x20_ISO4762_8_8_A2K_001_004
  Object2 = b_corner_steel_12_001_
  ParentTreeObject = -> b_corner_steel_12_001_
  SubElement1 = Edge31
  SubElement2 = Edge43
  Type = circularEdge
  directionConstraint = 0
  lockRotation = false
  offset = 8.5
FEATURE [Part::FeaturePython] b_Screw_M4x20_ISO4762_8_8_A2K_001_005  label="Screw M4x20 ISO4762 8,8 A2K_006"  # a2plus imported part (geometry in sourceFile) (typed FeaturePython)
  Placement = pos=(-136.853,188.9,-22.4993) rot=(-0.025477,0.706877,-0.706877;3.19254rad)
  a2p_Version = V0.1
  fixedPosition = false
  sourceFile = ./../../../Documents/FreeCadProjects/FreeCAD-library/Mechanical Parts/Fasteners/Bolts & Screws/Metric/ISO4762 Hexagon socket head cap screws/Screw M4x20 ISO4762 8,8 A2K.FCStd
  subassemblyImport = false
  timeLastImport = 1557779266
  updateColors = true
FEATURE [App::FeaturePython] circularEdge_025  label="circularEdge_025__corner_steel_12_001"  # a2plus constraint (typed FeaturePython)
  Object1 = b_Screw_M4x20_ISO4762_8_8_A2K_001_005
  Object2 = b_corner_steel_12_001_
  ParentTreeObject = -> b_Screw_M4x20_ISO4762_8_8_A2K_001_005
  SubElement1 = Edge1
  SubElement2 = Edge37
  Type = circularEdge
  directionConstraint = 0
  lockRotation = false
  offset = 8.5
FEATURE [App::FeaturePython] circularEdge_025_mirror  label="circularEdge_025__Screw M4x20 ISO4762 8,8 A2K_006"  # a2plus constraint (typed FeaturePython)
  Object1 = b_Screw_M4x20_ISO4762_8_8_A2K_001_005
  Object2 = b_corner_steel_12_001_
  ParentTreeObject = -> b_corner_steel_12_001_
  SubElement1 = Edge1
  SubElement2 = Edge37
  Type = circularEdge
  directionConstraint = 0
  lockRotation = false
  offset = 8.5
FEATURE [Part::FeaturePython] b_Screw_M4x20_ISO4762_8_8_A2K_001_006  label="Screw M4x20 ISO4762 8,8 A2K_007"  # a2plus imported part (geometry in sourceFile) (typed FeaturePython)
  Placement = pos=(-156.353,188.9,-32.4993) rot=(-0.025477,0.706877,-0.706877;3.19254rad)
  a2p_Version = V0.1
  fixedPosition = false
  sourceFile = ./../../../Documents/FreeCadProjects/FreeCAD-library/Mechanical Parts/Fasteners/Bolts & Screws/Metric/ISO4762 Hexagon socket head cap screws/Screw M4x20 ISO4762 8,8 A2K.FCStd
  subassemblyImport = false
  timeLastImport = 1557779266
  updateColors = true
FEATURE [App::FeaturePython] circularEdge_026  label="circularEdge_026__corner_steel_12_001"  # a2plus constraint (typed FeaturePython)
  Object1 = b_Screw_M4x20_ISO4762_8_8_A2K_001_006
  Object2 = b_corner_steel_12_001_
  ParentTreeObject = -> b_Screw_M4x20_ISO4762_8_8_A2K_001_006
  SubElement1 = Edge1
  SubElement2 = Edge41
  Type = circularEdge
  directionConstraint = 0
  lockRotation = false
  offset = 8.5
FEATURE [App::FeaturePython] circularEdge_026_mirror  label="circularEdge_026__Screw M4x20 ISO4762 8,8 A2K_007"  # a2plus constraint (typed FeaturePython)
  Object1 = b_Screw_M4x20_ISO4762_8_8_A2K_001_006
  Object2 = b_corner_steel_12_001_
  ParentTreeObject = -> b_corner_steel_12_001_
  SubElement1 = Edge1
  SubElement2 = Edge41
  Type = circularEdge
  directionConstraint = 0
  lockRotation = false
  offset = 8.5
FEATURE [Part::FeaturePython] b_Screw_M4x20_ISO4762_8_8_A2K_001_007  label="Screw M4x20 ISO4762 8,8 A2K_008"  # a2plus imported part (geometry in sourceFile) (typed FeaturePython)
  Placement = pos=(231.547,188.5,-22.4993) rot=(-0.025477,0.706877,-0.706877;3.19254rad)
  a2p_Version = V0.1
  fixedPosition = false
  sourceFile = ./../../../Documents/FreeCadProjects/FreeCAD-library/Mechanical Parts/Fasteners/Bolts & Screws/Metric/ISO4762 Hexagon socket head cap screws/Screw M4x20 ISO4762 8,8 A2K.FCStd
  subassemblyImport = false
  timeLastImport = 1557779266
  updateColors = true
FEATURE [App::FeaturePython] circularEdge_027  label="circularEdge_027__corner_steel_12_002"  # a2plus constraint (typed FeaturePython)
  Object1 = b_Screw_M4x20_ISO4762_8_8_A2K_001_007
  Object2 = b_corner_steel_12_001_001
  ParentTreeObject = -> b_Screw_M4x20_ISO4762_8_8_A2K_001_007
  SubElement1 = Edge31
  SubElement2 = Edge37
  Type = circularEdge
  directionConstraint = 0
  lockRotation = false
  offset = 8.9
FEATURE [App::FeaturePython] circularEdge_027_mirror  label="circularEdge_027__Screw M4x20 ISO4762 8,8 A2K_008"  # a2plus constraint (typed FeaturePython)
  Object1 = b_Screw_M4x20_ISO4762_8_8_A2K_001_007
  Object2 = b_corner_steel_12_001_001
  ParentTreeObject = -> b_corner_steel_12_001_001
  SubElement1 = Edge31
  SubElement2 = Edge37
  Type = circularEdge
  directionConstraint = 0
  lockRotation = false
  offset = 8.9
FEATURE [Part::FeaturePython] b_Screw_M4x20_ISO4762_8_8_A2K_001_008  label="Screw M4x20 ISO4762 8,8 A2K_009"  # a2plus imported part (geometry in sourceFile) (typed FeaturePython)
  Placement = pos=(212.047,188.9,-12.4993) rot=(-0.025477,0.706877,-0.706877;3.19254rad)
  a2p_Version = V0.1
  fixedPosition = false
  sourceFile = ./../../../Documents/FreeCadProjects/FreeCAD-library/Mechanical Parts/Fasteners/Bolts & Screws/Metric/ISO4762 Hexagon socket head cap screws/Screw M4x20 ISO4762 8,8 A2K.FCStd
  subassemblyImport = false
  timeLastImport = 1557779266
  updateColors = true
FEATURE [App::FeaturePython] circularEdge_028  label="circularEdge_028__corner_steel_12_002"  # a2plus constraint (typed FeaturePython)
  Object1 = b_Screw_M4x20_ISO4762_8_8_A2K_001_008
  Object2 = b_corner_steel_12_001_001
  ParentTreeObject = -> b_Screw_M4x20_ISO4762_8_8_A2K_001_008
  SubElement1 = Edge1
  SubElement2 = Edge39
  Type = circularEdge
  directionConstraint = 0
  lockRotation = false
  offset = 8.5
FEATURE [App::FeaturePython] circularEdge_028_mirror  label="circularEdge_028__Screw M4x20 ISO4762 8,8 A2K_009"  # a2plus constraint (typed FeaturePython)
  Object1 = b_Screw_M4x20_ISO4762_8_8_A2K_001_008
  Object2 = b_corner_steel_12_001_001
  ParentTreeObject = -> b_corner_steel_12_001_001
  SubElement1 = Edge1
  SubElement2 = Edge39
  Type = circularEdge
  directionConstraint = 0
  lockRotation = false
  offset = 8.5
FEATURE [Part::FeaturePython] b_Screw_M4x20_ISO4762_8_8_A2K_001_009  label="Screw M4x20 ISO4762 8,8 A2K_010"  # a2plus imported part (geometry in sourceFile) (typed FeaturePython)
  Placement = pos=(212.047,188.9,-32.4993) rot=(-0.025477,0.706877,-0.706877;3.19254rad)
  a2p_Version = V0.1
  fixedPosition = false
  sourceFile = ./../../../Documents/FreeCadProjects/FreeCAD-library/Mechanical Parts/Fasteners/Bolts & Screws/Metric/ISO4762 Hexagon socket head cap screws/Screw M4x20 ISO4762 8,8 A2K.FCStd
  subassemblyImport = false
  timeLastImport = 1557779266
  updateColors = true
FEATURE [App::FeaturePython] circularEdge_029  label="circularEdge_029__corner_steel_12_002"  # a2plus constraint (typed FeaturePython)
  Object1 = b_Screw_M4x20_ISO4762_8_8_A2K_001_009
  Object2 = b_corner_steel_12_001_001
  ParentTreeObject = -> b_Screw_M4x20_ISO4762_8_8_A2K_001_009
  SubElement1 = Edge1
  SubElement2 = Edge41
  Type = circularEdge
  directionConstraint = 0
  lockRotation = false
  offset = 8.5
FEATURE [App::FeaturePython] circularEdge_029_mirror  label="circularEdge_029__Screw M4x20 ISO4762 8,8 A2K_010"  # a2plus constraint (typed FeaturePython)
  Object1 = b_Screw_M4x20_ISO4762_8_8_A2K_001_009
  Object2 = b_corner_steel_12_001_001
  ParentTreeObject = -> b_corner_steel_12_001_001
  SubElement1 = Edge1
  SubElement2 = Edge41
  Type = circularEdge
  directionConstraint = 0
  lockRotation = false
  offset = 8.5
FEATURE [Part::FeaturePython] b_Screw_M4x20_ISO4762_8_8_A2K_001_010  label="Screw M4x20 ISO4762 8,8 A2K_011"  # a2plus imported part (geometry in sourceFile) (typed FeaturePython)
  Placement = pos=(231.547,188.7,-42.4993) rot=(-0.025477,0.706877,-0.706877;3.19254rad)
  a2p_Version = V0.1
  fixedPosition = false
  sourceFile = ./../../../Documents/FreeCadProjects/FreeCAD-library/Mechanical Parts/Fasteners/Bolts & Screws/Metric/ISO4762 Hexagon socket head cap screws/Screw M4x20 ISO4762 8,8 A2K.FCStd
  subassemblyImport = false
  timeLastImport = 1557779266
  updateColors = true
FEATURE [App::FeaturePython] circularEdge_030  label="circularEdge_030__corner_steel_12_002"  # a2plus constraint (typed FeaturePython)
  Object1 = b_Screw_M4x20_ISO4762_8_8_A2K_001_010
  Object2 = b_corner_steel_12_001_001
  ParentTreeObject = -> b_Screw_M4x20_ISO4762_8_8_A2K_001_010
  SubElement1 = Edge2
  SubElement2 = Edge43
  Type = circularEdge
  directionConstraint = 0
  lockRotation = false
  offset = 8.5
FEATURE [App::FeaturePython] circularEdge_030_mirror  label="circularEdge_030__Screw M4x20 ISO4762 8,8 A2K_011"  # a2plus constraint (typed FeaturePython)
  Object1 = b_Screw_M4x20_ISO4762_8_8_A2K_001_010
  Object2 = b_corner_steel_12_001_001
  ParentTreeObject = -> b_corner_steel_12_001_001
  SubElement1 = Edge2
  SubElement2 = Edge43
  Type = circularEdge
  directionConstraint = 0
  lockRotation = false
  offset = 8.5
FEATURE [Part::FeaturePython] b_Screw_M4x20_ISO4762_8_8_A2K_001_011  label="Screw M4x20 ISO4762 8,8 A2K_012"  # a2plus imported part (geometry in sourceFile) (typed FeaturePython)
  Placement = pos=(238.547,-188.9,-16.8006) rot=(-0.67889,0.519186,0.519186;1.94876rad)
  a2p_Version = V0.1
  fixedPosition = false
  sourceFile = ./../../../Documents/FreeCadProjects/FreeCAD-library/Mechanical Parts/Fasteners/Bolts & Screws/Metric/ISO4762 Hexagon socket head cap screws/Screw M4x20 ISO4762 8,8 A2K.FCStd
  subassemblyImport = false
  timeLastImport = 1557779266
  updateColors = true
FEATURE [App::FeaturePython] circularEdge_031  label="circularEdge_031__corner_steel_8_001"  # a2plus constraint (typed FeaturePython)
  Object1 = b_Screw_M4x20_ISO4762_8_8_A2K_001_011
  Object2 = b_corner_steel_8_001_
  ParentTreeObject = -> b_Screw_M4x20_ISO4762_8_8_A2K_001_011
  SubElement1 = Edge1
  SubElement2 = Edge43
  Type = circularEdge
  directionConstraint = 0
  lockRotation = false
  offset = 8.5
FEATURE [App::FeaturePython] circularEdge_031_mirror  label="circularEdge_031__Screw M4x20 ISO4762 8,8 A2K_012"  # a2plus constraint (typed FeaturePython)
  Object1 = b_Screw_M4x20_ISO4762_8_8_A2K_001_011
  Object2 = b_corner_steel_8_001_
  ParentTreeObject = -> b_corner_steel_8_001_
  SubElement1 = Edge1
  SubElement2 = Edge43
  Type = circularEdge
  directionConstraint = 0
  lockRotation = false
  offset = 8.5
FEATURE [Part::FeaturePython] b_Screw_M4x20_ISO4762_8_8_A2K_001_012  label="Screw M4x20 ISO4762 8,8 A2K_013"  # a2plus imported part (geometry in sourceFile) (typed FeaturePython)
  Placement = pos=(238.547,-188.9,-36.8006) rot=(-0.958697,-0.201122,-0.201123;1.61296rad)
  a2p_Version = V0.1
  fixedPosition = false
  sourceFile = ./../../../Documents/FreeCadProjects/FreeCAD-library/Mechanical Parts/Fasteners/Bolts & Screws/Metric/ISO4762 Hexagon socket head cap screws/Screw M4x20 ISO4762 8,8 A2K.FCStd
  subassemblyImport = false
  timeLastImport = 1557779266
  updateColors = true
FEATURE [App::FeaturePython] circularEdge_032  label="circularEdge_032__corner_steel_8_001"  # a2plus constraint (typed FeaturePython)
  Object1 = b_Screw_M4x20_ISO4762_8_8_A2K_001_012
  Object2 = b_corner_steel_8_001_
  ParentTreeObject = -> b_Screw_M4x20_ISO4762_8_8_A2K_001_012
  SubElement1 = Edge1
  SubElement2 = Edge37
  Type = circularEdge
  directionConstraint = 0
  lockRotation = false
  offset = 8.5
FEATURE [App::FeaturePython] circularEdge_032_mirror  label="circularEdge_032__Screw M4x20 ISO4762 8,8 A2K_013"  # a2plus constraint (typed FeaturePython)
  Object1 = b_Screw_M4x20_ISO4762_8_8_A2K_001_012
  Object2 = b_corner_steel_8_001_
  ParentTreeObject = -> b_corner_steel_8_001_
  SubElement1 = Edge1
  SubElement2 = Edge37
  Type = circularEdge
  directionConstraint = 0
  lockRotation = false
  offset = 8.5
FEATURE [Part::FeaturePython] b_Screw_M4x20_ISO4762_8_8_A2K_001_013  label="Screw M4x20 ISO4762 8,8 A2K_014"  # a2plus imported part (geometry in sourceFile) (typed FeaturePython)
  Placement = pos=(219.047,-188.7,-26.8006) rot=(0.147789,0.699342,0.699342;3.43505rad)
  a2p_Version = V0.1
  fixedPosition = false
  sourceFile = ./../../../Documents/FreeCadProjects/FreeCAD-library/Mechanical Parts/Fasteners/Bolts & Screws/Metric/ISO4762 Hexagon socket head cap screws/Screw M4x20 ISO4762 8,8 A2K.FCStd
  subassemblyImport = false
  timeLastImport = 1557779266
  updateColors = true
FEATURE [App::FeaturePython] circularEdge_033  label="circularEdge_033__corner_steel_8_001"  # a2plus constraint (typed FeaturePython)
  Object1 = b_Screw_M4x20_ISO4762_8_8_A2K_001_013
  Object2 = b_corner_steel_8_001_
  ParentTreeObject = -> b_Screw_M4x20_ISO4762_8_8_A2K_001_013
  SubElement1 = Edge32
  SubElement2 = Edge41
  Type = circularEdge
  directionConstraint = 0
  lockRotation = false
  offset = 8.5
FEATURE [App::FeaturePython] circularEdge_033_mirror  label="circularEdge_033__Screw M4x20 ISO4762 8,8 A2K_014"  # a2plus constraint (typed FeaturePython)
  Object1 = b_Screw_M4x20_ISO4762_8_8_A2K_001_013
  Object2 = b_corner_steel_8_001_
  ParentTreeObject = -> b_corner_steel_8_001_
  SubElement1 = Edge32
  SubElement2 = Edge41
  Type = circularEdge
  directionConstraint = 0
  lockRotation = false
  offset = 8.5
FEATURE [Part::FeaturePython] b_Screw_M4x20_ISO4762_8_8_A2K_001_014  label="Screw M4x20 ISO4762 8,8 A2K_015"  # a2plus imported part (geometry in sourceFile) (typed FeaturePython)
  Placement = pos=(219.047,-188.9,-46.8006) rot=(-0.662019,-0.529967,-0.529967;1.97204rad)
  a2p_Version = V0.1
  fixedPosition = false
  sourceFile = ./../../../Documents/FreeCadProjects/FreeCAD-library/Mechanical Parts/Fasteners/Bolts & Screws/Metric/ISO4762 Hexagon socket head cap screws/Screw M4x20 ISO4762 8,8 A2K.FCStd
  subassemblyImport = false
  timeLastImport = 1557779266
  updateColors = true
FEATURE [App::FeaturePython] circularEdge_034  label="circularEdge_034__corner_steel_8_001"  # a2plus constraint (typed FeaturePython)
  Object1 = b_Screw_M4x20_ISO4762_8_8_A2K_001_014
  Object2 = b_corner_steel_8_001_
  ParentTreeObject = -> b_Screw_M4x20_ISO4762_8_8_A2K_001_014
  SubElement1 = Edge1
  SubElement2 = Edge39
  Type = circularEdge
  directionConstraint = 0
  lockRotation = false
  offset = 8.5
FEATURE [App::FeaturePython] circularEdge_034_mirror  label="circularEdge_034__Screw M4x20 ISO4762 8,8 A2K_015"  # a2plus constraint (typed FeaturePython)
  Object1 = b_Screw_M4x20_ISO4762_8_8_A2K_001_014
  Object2 = b_corner_steel_8_001_
  ParentTreeObject = -> b_corner_steel_8_001_
  SubElement1 = Edge1
  SubElement2 = Edge39
  Type = circularEdge
  directionConstraint = 0
  lockRotation = false
  offset = 8.5
FEATURE [Part::FeaturePython] b_Screw_M4x20_ISO4762_8_8_A2K_001_015  label="Screw M4x20 ISO4762 8,8 A2K_016"  # a2plus imported part (geometry in sourceFile) (typed FeaturePython)
  Placement = pos=(-136.853,-188.7,-16.8006) rot=(0.034674,0.706682,0.706682;3.21091rad)
  a2p_Version = V0.1
  fixedPosition = false
  sourceFile = ./../../../Documents/FreeCadProjects/FreeCAD-library/Mechanical Parts/Fasteners/Bolts & Screws/Metric/ISO4762 Hexagon socket head cap screws/Screw M4x20 ISO4762 8,8 A2K.FCStd
  subassemblyImport = false
  timeLastImport = 1557779266
  updateColors = true
FEATURE [App::FeaturePython] circularEdge_035  label="circularEdge_035__corner_steel_8_002"  # a2plus constraint (typed FeaturePython)
  Object1 = b_Screw_M4x20_ISO4762_8_8_A2K_001_015
  Object2 = b_corner_steel_8_001_001
  ParentTreeObject = -> b_Screw_M4x20_ISO4762_8_8_A2K_001_015
  SubElement1 = Edge32
  SubElement2 = Edge43
  Type = circularEdge
  directionConstraint = 0
  lockRotation = false
  offset = 8.5
FEATURE [App::FeaturePython] circularEdge_035_mirror  label="circularEdge_035__Screw M4x20 ISO4762 8,8 A2K_016"  # a2plus constraint (typed FeaturePython)
  Object1 = b_Screw_M4x20_ISO4762_8_8_A2K_001_015
  Object2 = b_corner_steel_8_001_001
  ParentTreeObject = -> b_corner_steel_8_001_001
  SubElement1 = Edge32
  SubElement2 = Edge43
  Type = circularEdge
  directionConstraint = 0
  lockRotation = false
  offset = 8.5
FEATURE [Part::FeaturePython] b_Screw_M4x20_ISO4762_8_8_A2K_001_016  label="Screw M4x20 ISO4762 8,8 A2K_017"  # a2plus imported part (geometry in sourceFile) (typed FeaturePython)
  Placement = pos=(-156.353,-188.7,-26.8006) rot=(-0.398548,0.648521,0.648521;2.38308rad)
  a2p_Version = V0.1
  fixedPosition = false
  sourceFile = ./../../../Documents/FreeCadProjects/FreeCAD-library/Mechanical Parts/Fasteners/Bolts & Screws/Metric/ISO4762 Hexagon socket head cap screws/Screw M4x20 ISO4762 8,8 A2K.FCStd
  subassemblyImport = false
  timeLastImport = 1557779266
  updateColors = true
FEATURE [App::FeaturePython] circularEdge_036  label="circularEdge_036__corner_steel_8_002"  # a2plus constraint (typed FeaturePython)
  Object1 = b_Screw_M4x20_ISO4762_8_8_A2K_001_016
  Object2 = b_corner_steel_8_001_001
  ParentTreeObject = -> b_Screw_M4x20_ISO4762_8_8_A2K_001_016
  SubElement1 = Edge32
  SubElement2 = Edge41
  Type = circularEdge
  directionConstraint = 0
  lockRotation = false
  offset = 8.5
FEATURE [App::FeaturePython] circularEdge_036_mirror  label="circularEdge_036__Screw M4x20 ISO4762 8,8 A2K_017"  # a2plus constraint (typed FeaturePython)
  Object1 = b_Screw_M4x20_ISO4762_8_8_A2K_001_016
  Object2 = b_corner_steel_8_001_001
  ParentTreeObject = -> b_corner_steel_8_001_001
  SubElement1 = Edge32
  SubElement2 = Edge41
  Type = circularEdge
  directionConstraint = 0
  lockRotation = false
  offset = 8.5
FEATURE [Part::FeaturePython] b_Screw_M4x20_ISO4762_8_8_A2K_001_017  label="Screw M4x20 ISO4762 8,8 A2K_018"  # a2plus imported part (geometry in sourceFile) (typed FeaturePython)
  Placement = pos=(-136.853,-188.7,-36.8006) rot=(-0.687565,-0.513447,-0.513447;1.93693rad)
  a2p_Version = V0.1
  fixedPosition = false
  sourceFile = ./../../../Documents/FreeCadProjects/FreeCAD-library/Mechanical Parts/Fasteners/Bolts & Screws/Metric/ISO4762 Hexagon socket head cap screws/Screw M4x20 ISO4762 8,8 A2K.FCStd
  subassemblyImport = false
  timeLastImport = 1557779266
  updateColors = true
FEATURE [App::FeaturePython] circularEdge_037  label="circularEdge_037__corner_steel_8_002"  # a2plus constraint (typed FeaturePython)
  Object1 = b_Screw_M4x20_ISO4762_8_8_A2K_001_017
  Object2 = b_corner_steel_8_001_001
  ParentTreeObject = -> b_Screw_M4x20_ISO4762_8_8_A2K_001_017
  SubElement1 = Edge2
  SubElement2 = Edge37
  Type = circularEdge
  directionConstraint = 0
  lockRotation = false
  offset = 8.5
FEATURE [App::FeaturePython] circularEdge_037_mirror  label="circularEdge_037__Screw M4x20 ISO4762 8,8 A2K_018"  # a2plus constraint (typed FeaturePython)
  Object1 = b_Screw_M4x20_ISO4762_8_8_A2K_001_017
  Object2 = b_corner_steel_8_001_001
  ParentTreeObject = -> b_corner_steel_8_001_001
  SubElement1 = Edge2
  SubElement2 = Edge37
  Type = circularEdge
  directionConstraint = 0
  lockRotation = false
  offset = 8.5
FEATURE [Part::FeaturePython] b_Screw_M4x20_ISO4762_8_8_A2K_001_018  label="Screw M4x20 ISO4762 8,8 A2K_019"  # a2plus imported part (geometry in sourceFile) (typed FeaturePython)
  Placement = pos=(-156.353,-188.7,-46.8006) rot=(-0.973089,-0.162937,-0.162937;1.59807rad)
  a2p_Version = V0.1
  fixedPosition = false
  sourceFile = ./../../../Documents/FreeCadProjects/FreeCAD-library/Mechanical Parts/Fasteners/Bolts & Screws/Metric/ISO4762 Hexagon socket head cap screws/Screw M4x20 ISO4762 8,8 A2K.FCStd
  subassemblyImport = false
  timeLastImport = 1557779266
  updateColors = true
FEATURE [App::DocumentObjectGroup] Group013  label="Screw_steel corners"
  Group = -> [b_Screw_M4x20_ISO4762_8_8_A2K_001_003,b_Screw_M4x20_ISO4762_8_8_A2K_001_004,b_Screw_M4x20_ISO4762_8_8_A2K_001_005,b_Screw_M4x20_ISO4762_8_8_A2K_001_006,b_Screw_M4x20_ISO4762_8_8_A2K_001_007,b_Screw_M4x20_ISO4762_8_8_A2K_001_008,b_Screw_M4x20_ISO4762_8_8_A2K_001_009,b_Screw_M4x20_ISO4762_8_8_A2K_001_010,b_Screw_M4x20_ISO4762_8_8_A2K_001_011,b_Screw_M4x20_ISO4762_8_8_A2K_001_012,+6 more]
FEATURE [App::FeaturePython] circularEdge_038  label="circularEdge_038__corner_steel_8_002"  # a2plus constraint (typed FeaturePython)
  Object1 = b_Screw_M4x20_ISO4762_8_8_A2K_001_018
  Object2 = b_corner_steel_8_001_001
  ParentTreeObject = -> b_Screw_M4x20_ISO4762_8_8_A2K_001_018
  SubElement1 = Edge32
  SubElement2 = Edge39
  Type = circularEdge
  directionConstraint = 0
  lockRotation = false
  offset = 8.5
FEATURE [App::FeaturePython] circularEdge_038_mirror  label="circularEdge_038__Screw M4x20 ISO4762 8,8 A2K_019"  # a2plus constraint (typed FeaturePython)
  Object1 = b_Screw_M4x20_ISO4762_8_8_A2K_001_018
  Object2 = b_corner_steel_8_001_001
  ParentTreeObject = -> b_corner_steel_8_001_001
  SubElement1 = Edge32
  SubElement2 = Edge39
  Type = circularEdge
  directionConstraint = 0
  lockRotation = false
  offset = 8.5
FEATURE [Part::Part2DObjectPython] Line008  # Draft 2D object (typed FeaturePython)
  ChamferSize = 0
  Closed = false
  End = (297,208.5,-22.4993)
  FilletRadius = 0
  Length = 65.4533
  MakeFace = false
  Placement = pos=(231.547,208.5,-22.4993) rot=(0,0.707107,0.707107;3.14159rad)
  Points = (2) [(0,0,0),(-65.4533,0,0.000394049)]
  Start = (231.547,208.5,-22.4993)
  Subdivisions = 0
  Support = -> [b_Case_001_]
FEATURE [App::FeaturePython] Dimension006  # Draft dimension (typed FeaturePython)
  Diameter = false
  Dimline = (325.42,208.5,-5.19066)
  Direction = (0,0,0)
  Distance = 22.4993
  End = (297,208.5,0)
  Normal = (0,1,0)
  Start = (297,208.5,-22.4993)
FEATURE [Part::Part2DObjectPython] Line009  # Draft 2D object (typed FeaturePython)
  ChamferSize = 0
  Closed = false
  End = (297,208.5,-12.4993)
  FilletRadius = 0
  Length = 84.9542
  MakeFace = false
  Placement = pos=(212.047,208.9,-12.4993) rot=(0,0.707107,0.707107;3.14159rad)
  Points = (2) [(0,0,0),(-84.9533,0,-0.399999)]
  Start = (212.047,208.9,-12.4993)
  Subdivisions = 0
FEATURE [App::FeaturePython] Dimension007  # Draft dimension (typed FeaturePython)
  Diameter = false
  Dimline = (309.523,208.5,-5.8456)
  Direction = (0,0,0)
  Distance = 12.4993
  End = (297,208.5,0)
  Normal = (0,1,0)
  Start = (297,208.5,-12.4993)
FEATURE [Part::Part2DObjectPython] Line010  # Draft 2D object (typed FeaturePython)
  ChamferSize = 0
  Closed = false
  End = (297,208.5,-32.4993)
  FilletRadius = 0
  Length = 84.9542
  MakeFace = false
  Placement = pos=(212.047,208.9,-32.4993) rot=(0,0.707107,0.707107;3.14159rad)
  Points = (2) [(0,0,0),(-84.9533,0,-0.399999)]
  Start = (212.047,208.9,-32.4993)
  Subdivisions = 0
FEATURE [Part::Part2DObjectPython] Line011  # Draft 2D object (typed FeaturePython)
  ChamferSize = 0
  Closed = false
  End = (297,208.5,-42.4993)
  FilletRadius = 0
  Length = 65.4536
  MakeFace = false
  Placement = pos=(231.547,208.7,-42.4993) rot=(0,0.707107,0.707107;3.14159rad)
  Points = (2) [(0,0,0),(-65.4533,0,-0.199999)]
  Start = (231.547,208.7,-42.4993)
  Subdivisions = 0
FEATURE [App::FeaturePython] Dimension009  # Draft dimension (typed FeaturePython)
  Diameter = false
  Dimline = (408.524,208.5,-12.0115)
  Direction = (0,0,0)
  Distance = 42.4993
  End = (297,208.5,0)
  Normal = (0,1,0)
  Start = (297,208.5,-42.4993)
FEATURE [App::FeaturePython] Dimension010  # Draft dimension (typed FeaturePython)
  Diameter = false
  Dimline = (356.228,208.5,-7.84259)
  Direction = (0,0,0)
  Distance = 32.4993
  End = (297,208.5,0)
  Normal = (0,1,0)
  Start = (297,208.5,-32.4993)
FEATURE [Part::Part2DObjectPython] Line012  # Draft 2D object (typed FeaturePython)
  ChamferSize = 0
  Closed = false
  End = (212.047,208.5,2.84e-14)
  FilletRadius = 0
  Length = 32.5018
  MakeFace = false
  Placement = pos=(212.047,208.9,-32.4993) rot=(-1,0,0;1.5708rad)
  Points = (2) [(0,0,0),(1.06744e-08,-32.4993,-0.399999)]
  Start = (212.047,208.9,-32.4993)
  Subdivisions = 0
FEATURE [Part::Part2DObjectPython] Line013  # Draft 2D object (typed FeaturePython)
  ChamferSize = 0
  Closed = false
  End = (231.547,208.5,0)
  FilletRadius = 0
  Length = 42.4998
  MakeFace = false
  Placement = pos=(231.547,208.7,-42.4993) rot=(0,0.707107,0.707107;3.14159rad)
  Points = (2) [(0,0,0),(0,42.4993,-0.199999)]
  Start = (231.547,208.7,-42.4993)
  Subdivisions = 0
FEATURE [App::FeaturePython] Dimension011  # Draft dimension (typed FeaturePython)
  Diameter = false
  Dimline = (294.781,208.5,57.9838)
  Direction = (0,0,0)
  Distance = 84.9533
  End = (297,208.5,0)
  Normal = (0,1,0)
  Start = (212.047,208.5,0)
FEATURE [App::FeaturePython] Dimension012  # Draft dimension (typed FeaturePython)
  Diameter = false
  Dimline = (292.035,208.5,43.3112)
  Direction = (0,0,0)
  Distance = 65.4533
  End = (297,208.5,0)
  Normal = (0,1,0)
  Start = (231.547,208.5,0)
FEATURE [Part::Part2DObjectPython] Line014  # Draft 2D object (typed FeaturePython)
  ChamferSize = 0
  Closed = false
  End = (-297,208.5,-12.4993)
  FilletRadius = 0
  Length = 140.647
  MakeFace = false
  Placement = pos=(-156.353,208.9,-12.4993) rot=(0,0.707107,0.707107;3.14159rad)
  Points = (2) [(0,0,0),(140.647,0,-0.4)]
  Start = (-156.353,208.9,-12.4993)
  Subdivisions = 0
FEATURE [Part::Part2DObjectPython] Line015  # Draft 2D object (typed FeaturePython)
  ChamferSize = 0
  Closed = false
  End = (-297,208.5,-32.4993)
  FilletRadius = 0
  Length = 140.647
  MakeFace = false
  Placement = pos=(-156.353,208.9,-32.4993) rot=(0,0.707107,0.707107;3.14159rad)
  Points = (2) [(0,0,0),(140.647,0,-0.4)]
  Start = (-156.353,208.9,-32.4993)
  Subdivisions = 0
FEATURE [Part::Part2DObjectPython] Line016  # Draft 2D object (typed FeaturePython)
  ChamferSize = 0
  Closed = false
  End = (-297,208.5,-22.4993)
  FilletRadius = 0
  Length = 160.147
  MakeFace = false
  Placement = pos=(-136.853,208.9,-22.4993) rot=(0,0.707107,0.707107;3.14159rad)
  Points = (2) [(0,0,0),(160.147,0,-0.4)]
  Start = (-136.853,208.9,-22.4993)
  Subdivisions = 0
FEATURE [Part::Part2DObjectPython] Line017  # Draft 2D object (typed FeaturePython)
  ChamferSize = 0
  Closed = false
  End = (-297,208.5,-42.4993)
  FilletRadius = 0
  Length = 160.147
  MakeFace = false
  Placement = pos=(-136.853,208.9,-42.4993) rot=(0,0.707107,0.707107;3.14159rad)
  Points = (2) [(0,0,0),(160.147,7.10543e-15,-0.4)]
  Start = (-136.853,208.9,-42.4993)
  Subdivisions = 0
FEATURE [Part::Part2DObjectPython] Line018  # Draft 2D object (typed FeaturePython)
  ChamferSize = 0
  Closed = false
  End = (-156.353,208.5,0)
  FilletRadius = 0
  Length = 32.5018
  MakeFace = false
  Placement = pos=(-156.353,208.9,-32.4993) rot=(0,0.707107,0.707107;3.14159rad)
  Points = (2) [(0,0,0),(-5.68434e-14,32.4993,-0.4)]
  Start = (-156.353,208.9,-32.4993)
  Subdivisions = 0
FEATURE [Part::Part2DObjectPython] Line019  # Draft 2D object (typed FeaturePython)
  ChamferSize = 0
  Closed = false
  End = (-136.853,208.5,2.84e-14)
  FilletRadius = 0
  Length = 42.5012
  MakeFace = false
  Placement = pos=(-136.853,208.9,-42.4993) rot=(-1,0,0;1.5708rad)
  Points = (2) [(0,0,0),(1.78902e-08,-42.4993,-0.4)]
  Start = (-136.853,208.9,-42.4993)
  Subdivisions = 0
FEATURE [App::FeaturePython] Dimension013  # Draft dimension (typed FeaturePython)
  Diameter = false
  Dimline = (-309.628,208.5,-1.46745)
  Direction = (0,0,0)
  Distance = 12.4993
  End = (-297,208.5,0)
  Normal = (0,1,0)
  Start = (-297,208.5,-12.4993)
FEATURE [App::FeaturePython] Dimension014  # Draft dimension (typed FeaturePython)
  Diameter = false
  Dimline = (-324.851,208.5,-2.53067)
  Direction = (0,0,0)
  Distance = 22.4993
  End = (-297,208.5,0)
  Normal = (0,1,0)
  Start = (-297,208.5,-22.4993)
FEATURE [App::FeaturePython] Dimension015  # Draft dimension (typed FeaturePython)
  Diameter = false
  Dimline = (-339.904,208.5,-2.12397)
  Direction = (0,0,0)
  Distance = 32.4993
  End = (-297,208.5,0)
  Normal = (0,1,0)
  Start = (-297,208.5,-32.4993)
FEATURE [App::FeaturePython] Dimension016  # Draft dimension (typed FeaturePython)
  Diameter = false
  Dimline = (-353.821,208.5,-5.37716)
  Direction = (0,0,0)
  Distance = 42.4993
  End = (-297,208.5,0)
  Normal = (0,1,0)
  Start = (-297,208.5,-42.4993)
FEATURE [App::FeaturePython] Dimension017  # Draft dimension (typed FeaturePython)
  Diameter = false
  Dimline = (-290.033,208.5,26.3173)
  Direction = (0,0,0)
  Distance = 140.647
  End = (-297,208.5,0)
  Normal = (0,1,0)
  Start = (-156.353,208.5,0)
FEATURE [App::FeaturePython] Dimension018  # Draft dimension (typed FeaturePython)
  Diameter = false
  Dimline = (-296.786,208.5,41.4864)
  Direction = (0,0,0)
  Distance = 160.147
  End = (-297,208.5,0)
  Normal = (0,1,0)
  Start = (-136.853,208.5,1.42e-14)
FEATURE [Part::Part2DObjectPython] Line020  # Draft 2D object (typed FeaturePython)
  ChamferSize = 0
  Closed = false
  End = (-297,-208.5,-46.8006)
  FilletRadius = 0
  Length = 140.647
  MakeFace = false
  Placement = pos=(-156.353,-208.7,-46.8006) rot=(0,0.707107,0.707107;3.14159rad)
  Points = (2) [(0,0,0),(140.647,0,0.199991)]
  Start = (-156.353,-208.7,-46.8006)
  Subdivisions = 0
FEATURE [Part::Part2DObjectPython] Line021  # Draft 2D object (typed FeaturePython)
  ChamferSize = 0
  Closed = false
  End = (-297,-208.5,-26.8006)
  FilletRadius = 0
  Length = 140.647
  MakeFace = false
  Placement = pos=(-156.353,-208.7,-26.8006) rot=(0,0.707107,0.707107;3.14159rad)
  Points = (2) [(0,0,0),(140.647,0,0.199991)]
  Start = (-156.353,-208.7,-26.8006)
  Subdivisions = 0
FEATURE [Part::Part2DObjectPython] Line022  # Draft 2D object (typed FeaturePython)
  ChamferSize = 0
  Closed = false
  End = (-297,-208.5,-36.8006)
  FilletRadius = 0
  Length = 160.147
  MakeFace = false
  Placement = pos=(-136.853,-208.7,-36.8006) rot=(0,0.707107,0.707107;3.14159rad)
  Points = (2) [(0,0,0),(160.147,0,0.199992)]
  Start = (-136.853,-208.7,-36.8006)
  Subdivisions = 0
FEATURE [Part::Part2DObjectPython] Line023  # Draft 2D object (typed FeaturePython)
  ChamferSize = 0
  Closed = false
  End = (-297,-208.5,-16.8006)
  FilletRadius = 0
  Length = 160.147
  MakeFace = false
  Placement = pos=(-136.853,-208.7,-16.8006) rot=(0,0.707107,0.707107;3.14159rad)
  Points = (2) [(0,0,0),(160.147,0,0.199992)]
  Start = (-136.853,-208.7,-16.8006)
  Subdivisions = 0
FEATURE [Part::Part2DObjectPython] Line024  # Draft 2D object (typed FeaturePython)
  ChamferSize = 0
  Closed = false
  End = (-156.353,-208.5,0)
  FilletRadius = 0
  Length = 46.801
  MakeFace = false
  Placement = pos=(-156.353,-208.7,-46.8006) rot=(0,0.707107,0.707107;3.14159rad)
  Points = (2) [(0,0,0),(0,46.8006,0.199991)]
  Start = (-156.353,-208.7,-46.8006)
  Subdivisions = 0
FEATURE [Part::Part2DObjectPython] Line025  # Draft 2D object (typed FeaturePython)
  ChamferSize = 0
  Closed = false
  End = (-136.853,-208.5,0)
  FilletRadius = 0
  Length = 36.8011
  MakeFace = false
  Placement = pos=(-136.853,-208.7,-36.8006) rot=(0,0.707107,0.707107;3.14159rad)
  Points = (2) [(0,0,0),(2.84217e-14,36.8006,0.199992)]
  Start = (-136.853,-208.7,-36.8006)
  Subdivisions = 0
FEATURE [App::FeaturePython] Dimension019  # Draft dimension (typed FeaturePython)
  Diameter = false
  Dimline = (-330.679,-208.5,-3.47938)
  Direction = (0,0,0)
  Distance = 16.8006
  End = (-297,-208.5,0)
  Normal = (0,-1,0)
  Start = (-297,-208.5,-16.8006)
FEATURE [App::FeaturePython] Dimension020  # Draft dimension (typed FeaturePython)
  Diameter = false
  Dimline = (-347.495,-208.5,1.17652)
  Direction = (0,0,0)
  Distance = 26.8006
  End = (-297,-208.5,0)
  Normal = (0,-1,0)
  Start = (-297,-208.5,-26.8006)
FEATURE [App::FeaturePython] Dimension021  # Draft dimension (typed FeaturePython)
  Diameter = false
  Dimline = (-371.058,-208.5,2.12191)
  Direction = (0,0,0)
  Distance = 36.8006
  End = (-297,-208.5,0)
  Normal = (0,-1,0)
  Start = (-297,-208.5,-36.8006)
FEATURE [App::FeaturePython] Dimension022  # Draft dimension (typed FeaturePython)
  Diameter = false
  Dimline = (-389.405,-208.5,-43.2861)
  Direction = (0,0,0)
  Distance = 46.8006
  End = (-297,-208.5,-46.8006)
  Normal = (0,-1,0)
  Start = (-297,-208.5,0)
FEATURE [App::FeaturePython] Dimension023  # Draft dimension (typed FeaturePython)
  Diameter = false
  Dimline = (-167.489,-208.5,22.2844)
  Direction = (0,0,0)
  Distance = 140.647
  End = (-156.353,-208.5,0)
  Normal = (0,-1,0)
  Start = (-297,-208.5,0)
FEATURE [App::FeaturePython] Dimension024  # Draft dimension (typed FeaturePython)
  Diameter = false
  Dimline = (-291.612,-208.5,38.3615)
  Direction = (0,0,0)
  Distance = 160.147
  End = (-297,-208.5,0)
  Normal = (0,-1,0)
  Start = (-136.853,-208.5,0)
FEATURE [Part::Part2DObjectPython] Line026  # Draft 2D object (typed FeaturePython)
  ChamferSize = 0
  Closed = false
  End = (297,-208.5,-16.8006)
  FilletRadius = 0
  Length = 58.4547
  MakeFace = false
  Placement = pos=(238.547,-208.9,-16.8006) rot=(1,0,0;1.5708rad)
  Points = (2) [(0,0,0),(58.4533,0,-0.400007)]
  Start = (238.547,-208.9,-16.8006)
  Subdivisions = 0
FEATURE [Part::Part2DObjectPython] Line027  # Draft 2D object (typed FeaturePython)
  ChamferSize = 0
  Closed = false
  End = (297,-208.5,-46.8006)
  FilletRadius = 0
  Length = 77.9543
  MakeFace = true
  Placement = pos=(219.047,-208.9,-46.8006) rot=(1,0,0;1.5708rad)
  Points = (2) [(0,0,0),(77.9533,0,-0.400006)]
  Start = (219.047,-208.9,-46.8006)
  Subdivisions = 0
FEATURE [App::FeaturePython] Dimension025  # Draft dimension (typed FeaturePython)
  Diameter = false
  Dimline = (328.35,-208.5,-5.22785)
  Direction = (0,0,0)
  Distance = 16.8006
  End = (297,-208.5,0)
  Normal = (0,-1,0)
  Start = (297,-208.5,-16.8006)
FEATURE [App::FeaturePython] Dimension026  # Draft dimension (typed FeaturePython)
  Diameter = false
  Dimline = (350.224,-208.5,-6.01736)
  Direction = (0,0,0)
  Distance = 46.8006
  End = (297,-208.5,0)
  Normal = (0,-1,0)
  Start = (297,-208.5,-46.8006)
FEATURE [Part::Part2DObjectPython] Line028  # Draft 2D object (typed FeaturePython)
  ChamferSize = 0
  Closed = false
  End = (218.697,-208.5,0)
  FilletRadius = 0
  Length = 46.726
  MakeFace = true
  Placement = pos=(218.697,-208.5,-46.726) rot=(1,0,0;1.5708rad)
  Points = (2) [(0,0,0),(5.68434e-14,46.726,-2.84217e-14)]
  Start = (218.697,-208.5,-46.726)
  Subdivisions = 0
FEATURE [Part::Part2DObjectPython] Line029  # Draft 2D object (typed FeaturePython)
  ChamferSize = 0
  Closed = false
  End = (238.547,-208.5,9.95e-14)
  FilletRadius = 0
  Length = 36.8028
  MakeFace = true
  Placement = pos=(238.547,-208.9,-36.8006) rot=(1,0,0;1.5708rad)
  Points = (2) [(0,0,0),(-9.93401e-09,36.8006,-0.400007)]
  Start = (238.547,-208.9,-36.8006)
  Subdivisions = 0
FEATURE [App::FeaturePython] Dimension027  # Draft dimension (typed FeaturePython)
  Diameter = false
  Dimline = (297.792,-208.5,64.7413)
  Direction = (0,0,0)
  Distance = 78.3029
  End = (297,-208.5,0)
  Normal = (0,-1,0)
  Start = (218.697,-208.5,-7.1e-15)
FEATURE [App::FeaturePython] Dimension028  # Draft dimension (typed FeaturePython)
  Diameter = false
  Dimline = (294.206,-208.5,31.2582)
  Direction = (0,0,0)
  Distance = 58.4533
  End = (297,-208.5,0)
  Normal = (0,-1,0)
  Start = (238.547,-208.5,4.97e-14)
FEATURE [App::FeaturePython] Dimension029  # Draft dimension (typed FeaturePython)
  Diameter = false
  Dimline = (7.98593,-171.5,6.4994)
  Direction = (0,0,0)
  Distance = 343.092
  End = (7.98593,-171.5,6.4994)
  Normal = (-2.91219e-06,2.08077e-07,1)
  Start = (7.9861,171.592,6.49985)
